FCSTD DOCUMENT  (FreeCAD 0.16R6707 (Git))
Label: Z4
License: All rights reserved
LicenseURL: http://en.wikipedia.org/wiki/All_rights_reserved
objects: Part::FeaturePython×70, Sketcher::SketchObject×60, App::DocumentObjectGroup×43, PartDesign::Pad×34, Part::Feature×24, PartDesign::Pocket×18, Part::Mirroring×11, PartDesign::PolarPattern×8, Part::MultiFuse×6, PartDesign::Revolution×2, Part::Fillet×2, Part::Chamfer×2, PartDesign::Fillet×2, Part::MultiCommon×1, Part::Sphere×1
note: 295 computed .brp shape members not serialized (recipe doc carries the construction recipe); baked Part::Feature solids carry a one-line shape summary decoded from their .brp

FEATURE [Part::Feature] Part__Feature001  label="MoteurD"
  Placement = pos=(-2.4,0,8.5) rot=(-0.57735,-0.57735,0.57735;2.0944rad)
  shape: bbox 27.5 x 17 x 17 mm, 28 faces (baked)
FEATURE [Part::FeaturePython] Clone001  label="MoteurG"  # Draft clone (typed FeaturePython)
  Objects = -> [Part__Feature001]
  Placement = pos=(2.4,0,8.5) rot=(0.57735,-0.57735,0.57735;4.18879rad)
  Scale = (1,1,1)
FEATURE [Part::Feature] Part__Feature014  label="Axe"
  Placement = pos=(0,0,5.5) rot=(0,0,1;0rad)
  shape: bbox 4.5 x 4 x 15.2 mm, 12 faces (baked)
FEATURE [Part::Feature] Part__Feature020  label="Pignon1"
  Placement = pos=(-26.2,0,8.5) rot=(-0.55834,0.613607,-0.55834;2.04087rad)
  shape: bbox 4 x 6.752 x 6.785 mm, 485 faces (baked)
FEATURE [Part::Feature] Part__Feature022  label="Couronne"
  Placement = pos=(0,0,11.5) rot=(0,1,0;3.14159rad)
  shape: bbox 20.79 x 20.8 x 4 mm, 805 faces (baked)
FEATURE [Sketcher::SketchObject] Sketch001  label="JanteBaseA"
  sketch-geometry (6):
    g0: Circle [constr] CenterX=0 CenterY=0 CenterZ=0 NormalX=0 NormalY=0 NormalZ=1 Radius=10
    g1: Circle [constr] CenterX=0 CenterY=0 CenterZ=0 NormalX=0 NormalY=0 NormalZ=1 Radius=9
    g2: Circle [constr] CenterX=0 CenterY=0 CenterZ=0 NormalX=0 NormalY=0 NormalZ=1 Radius=3
    g3: Circle [constr] CenterX=0 CenterY=0 CenterZ=0 NormalX=0 NormalY=0 NormalZ=1 Radius=2.75
    g4: Circle [constr] CenterX=0 CenterY=0 CenterZ=0 NormalX=0 NormalY=0 NormalZ=1 Radius=4
    g5: Circle CenterX=0 CenterY=0 CenterZ=0 NormalX=0 NormalY=0 NormalZ=1 Radius=10.4
  constraints (14):
    c: Coincident(g0,g-1)
    c: Coincident(g1,g-1)
    c: Radius(g1) = 9
    c: Radius(g0) = 10
    c: Coincident(g2,g-1)
    c: Radius(g2) = 3
    c: Coincident(g3,g-1)
    c: Radius(g3) = 2.75
    c: PointOnObject(g4,g-1)
    c: Radius(g4) = 4
    c: PointOnObject(g5,g-1)
    c: Radius(g5) = 10.4
    c: Coincident(g5,g-1)
    c: Coincident(g4,g-1)
FEATURE [PartDesign::Pad] Pad003  label="Extrusion1A"
  Length = 8.5
  Length2 = 100
  Sketch = -> Sketch001
  Type = 0
FEATURE [Sketcher::SketchObject] Sketch018  label="JanteEvidageA"
  Placement = pos=(0,0,0) rot=(1,0,0;3.14159rad)
  Support = -> Pad003 [Face2]
  sketch-geometry (6):
    g0: Circle [constr] CenterX=0 CenterY=0 CenterZ=0 NormalX=0 NormalY=0 NormalZ=1 Radius=10
    g1: Circle CenterX=0 CenterY=0 CenterZ=0 NormalX=0 NormalY=0 NormalZ=1 Radius=9
    g2: Circle [constr] CenterX=0 CenterY=0 CenterZ=0 NormalX=0 NormalY=0 NormalZ=1 Radius=3
    g3: Circle [constr] CenterX=0 CenterY=0 CenterZ=0 NormalX=0 NormalY=0 NormalZ=1 Radius=2.75
    g4: Circle [constr] CenterX=0 CenterY=0 CenterZ=0 NormalX=0 NormalY=0 NormalZ=1 Radius=4
    g5: Circle [constr] CenterX=0 CenterY=0 CenterZ=0 NormalX=0 NormalY=0 NormalZ=1 Radius=10.4
  constraints (14):
    c: Coincident(g0,g-1)
    c: Coincident(g1,g-1)
    c: Radius(g1) = 9
    c: Radius(g0) = 10
    c: Coincident(g2,g-1)
    c: Radius(g2) = 3
    c: Coincident(g3,g-1)
    c: Radius(g3) = 2.75
    c: PointOnObject(g4,g-1)
    c: Radius(g4) = 4
    c: PointOnObject(g5,g-1)
    c: Radius(g5) = 10.4
    c: Coincident(g5,g-1)
    c: Coincident(g4,g-1)
FEATURE [PartDesign::Pocket] Pocket006  label="Evidage1A"
  Length = 7.5
  Sketch = -> Sketch018
  Type = 0
FEATURE [Sketcher::SketchObject] Sketch019  label="JantePercageA"
  Placement = pos=(0,0,7.5) rot=(1,0,0;3.14159rad)
  Support = -> Pocket006 [Face5]
  sketch-geometry (6):
    g0: Circle [constr] CenterX=0 CenterY=0 CenterZ=0 NormalX=0 NormalY=0 NormalZ=1 Radius=10
    g1: Circle [constr] CenterX=0 CenterY=0 CenterZ=0 NormalX=0 NormalY=0 NormalZ=1 Radius=9
    g2: Circle [constr] CenterX=0 CenterY=0 CenterZ=0 NormalX=0 NormalY=0 NormalZ=1 Radius=3
    g3: Circle [constr] CenterX=0 CenterY=0 CenterZ=0 NormalX=0 NormalY=0 NormalZ=1 Radius=2.75
    g4: Circle CenterX=0 CenterY=0 CenterZ=0 NormalX=0 NormalY=0 NormalZ=1 Radius=6
    g5: Circle [constr] CenterX=0 CenterY=0 CenterZ=0 NormalX=0 NormalY=0 NormalZ=1 Radius=10.4
  constraints (14):
    c: Coincident(g0,g-1)
    c: Coincident(g1,g-1)
    c: Radius(g1) = 9
    c: Radius(g0) = 10
    c: Coincident(g2,g-1)
    c: Radius(g2) = 3
    c: Coincident(g3,g-1)
    c: Radius(g3) = 2.75
    c: PointOnObject(g4,g-1)
    c: Radius(g4) = 6
    c: PointOnObject(g5,g-1)
    c: Radius(g5) = 10.4
    c: Coincident(g5,g-1)
    c: Coincident(g4,g-1)
FEATURE [PartDesign::Pocket] Pocket007  label="Percage1A"
  Length = 5
  Sketch = -> Sketch019
  Type = 1
FEATURE [Sketcher::SketchObject] Sketch020  label="JanteBaseB"
  sketch-geometry (6):
    g0: Circle [constr] CenterX=0 CenterY=0 CenterZ=0 NormalX=0 NormalY=0 NormalZ=1 Radius=10
    g1: Circle CenterX=0 CenterY=0 CenterZ=0 NormalX=0 NormalY=0 NormalZ=1 Radius=9
    g2: Circle CenterX=0 CenterY=0 CenterZ=0 NormalX=0 NormalY=0 NormalZ=1 Radius=3.1
    g3: Circle [constr] CenterX=0 CenterY=0 CenterZ=0 NormalX=0 NormalY=0 NormalZ=1 Radius=2.75
    g4: Circle [constr] CenterX=0 CenterY=0 CenterZ=0 NormalX=0 NormalY=0 NormalZ=1 Radius=4
    g5: Circle [constr] CenterX=0 CenterY=0 CenterZ=0 NormalX=0 NormalY=0 NormalZ=1 Radius=10.4
  constraints (14):
    c: Coincident(g0,g-1)
    c: Coincident(g1,g-1)
    c: Radius(g1) = 9
    c: Radius(g0) = 10
    c: Coincident(g2,g-1)
    c: Radius(g2) = 3.1
    c: Coincident(g3,g-1)
    c: Radius(g3) = 2.75
    c: PointOnObject(g4,g-1)
    c: Radius(g4) = 4
    c: PointOnObject(g5,g-1)
    c: Radius(g5) = 10.4
    c: Coincident(g5,g-1)
    c: Coincident(g4,g-1)
FEATURE [PartDesign::Pad] Pad004  label="Extrusion1B"
  Length = 6
  Length2 = 100
  Sketch = -> Sketch020
  Type = 0
FEATURE [Sketcher::SketchObject] Sketch005  label="JanteEvidageB"
  Placement = pos=(0,0,6) rot=(0,0,1;0rad)
  Support = -> Pad004 [Face4]
  sketch-geometry (6):
    g0: Circle [constr] CenterX=0 CenterY=0 CenterZ=0 NormalX=0 NormalY=0 NormalZ=1 Radius=10
    g1: Circle CenterX=0 CenterY=0 CenterZ=0 NormalX=0 NormalY=0 NormalZ=1 Radius=9
    g2: Circle [constr] CenterX=0 CenterY=0 CenterZ=0 NormalX=0 NormalY=0 NormalZ=1 Radius=3
    g3: Circle [constr] CenterX=0 CenterY=0 CenterZ=0 NormalX=0 NormalY=0 NormalZ=1 Radius=2.75
    g4: Circle CenterX=0 CenterY=0 CenterZ=0 NormalX=0 NormalY=0 NormalZ=1 Radius=4.5
    g5: Circle [constr] CenterX=0 CenterY=0 CenterZ=0 NormalX=0 NormalY=0 NormalZ=1 Radius=10.4
  constraints (14):
    c: Coincident(g0,g-1)
    c: Coincident(g1,g-1)
    c: Radius(g1) = 9
    c: Radius(g0) = 10
    c: Coincident(g2,g-1)
    c: Radius(g2) = 3
    c: Coincident(g3,g-1)
    c: Radius(g3) = 2.75
    c: PointOnObject(g4,g-1)
    c: Radius(g4) = 4.5
    c: PointOnObject(g5,g-1)
    c: Radius(g5) = 10.4
    c: Coincident(g5,g-1)
    c: Coincident(g4,g-1)
FEATURE [PartDesign::Pocket] Pocket008  label="Evidage1B"
  Length = 4
  Sketch = -> Sketch005
  Type = 0
FEATURE [Sketcher::SketchObject] Sketch007  label="JanteAjouragesA"
  Placement = pos=(0,0,0) rot=(1,0,0;3.14159rad)
  Support = -> Pocket007 [Face2]
  sketch-geometry (6):
    g0: ArcOfCircle CenterX=0 CenterY=0 CenterZ=0 NormalX=0 NormalY=0 NormalZ=1 Radius=9 StartAngle=1.0472 EndAngle=2.0944
    g1: ArcOfCircle CenterX=-1e-12 CenterY=-1.4e-11 CenterZ=0 NormalX=0 NormalY=0 NormalZ=1 Radius=4.7e-10 StartAngle=1.6983 EndAngle=1.76808
    g2: ArcOfCircle CenterX=-9e-12 CenterY=0 CenterZ=0 NormalX=0 NormalY=0 NormalZ=1 Radius=4.5 StartAngle=0.698132 EndAngle=2.44346
    g3: LineSegment StartX=-4.5 StartY=7.79423 StartZ=0 EndX=-3.4472 EndY=2.89254 EndZ=0
    g4: LineSegment StartX=4.5 StartY=7.79423 StartZ=0 EndX=3.4472 EndY=2.89254 EndZ=0
    g5: LineSegment [constr] StartX=0 StartY=0 StartZ=0 EndX=3.4472 EndY=2.89254 EndZ=0
  constraints (13):
    c: Coincident(g4,g2)
    c: Coincident(g3,g2)
    c: Coincident(g0,g4)
    c: Coincident(g0,g3)
    c: Symmetric(g2,g2,g-2)
    c: Coincident(g5,g-1)
    c: Coincident(g5,g2)
    c: Angle(g5,g-2) = 0.872665
    c: Symmetric(g0,g0,g-2)
    c: Coincident(g2,g-1)
    c: Coincident(g0,g-1)
    c: Radius(g2) = 4.5
    c: Radius(g0) = 9
FEATURE [PartDesign::Pocket] Pocket010  label="Ajourage1A"
  Length = 5
  Sketch = -> Sketch007
  Type = 1
FEATURE [PartDesign::PolarPattern] PolarPattern002  label="Ajourages1A"
  Angle = 360
  Axis = -> Sketch007 [N_Axis]
  Occurrences = 3
  Originals = -> [Pocket010]
FEATURE [Sketcher::SketchObject] Sketch009  label="JanteExtrusionB"
  Placement = pos=(0,0,2) rot=(0,0,1;0rad)
  Support = -> Pocket008 [Face3]
  sketch-geometry (3):
    g0: ArcOfCircle CenterX=-1e-12 CenterY=-1.4e-11 CenterZ=0 NormalX=0 NormalY=0 NormalZ=1 Radius=4.7e-10 StartAngle=1.6983 EndAngle=1.76808
    g1: Circle CenterX=0 CenterY=7.5 CenterZ=0 NormalX=0 NormalY=0 NormalZ=1 Radius=1
    g2: LineSegment [constr] StartX=0 StartY=0 StartZ=0 EndX=0 EndY=7.5 EndZ=0
  constraints (5):
    c: Coincident(g2,g-1)
    c: Coincident(g1,g2)
    c: Distance(g2) = 7.5
    c: Radius(g1) = 1
    c: PointOnObject(g1,g-2)
FEATURE [Sketcher::SketchObject] Sketch022  label="JanteEvidage2A"
  Placement = pos=(0,0,0) rot=(1,0,0;3.14159rad)
  Support = -> PolarPattern002 [Face2]
  sketch-geometry (6):
    g0: Circle CenterX=0 CenterY=0 CenterZ=0 NormalX=0 NormalY=0 NormalZ=1 Radius=10
    g1: Circle [constr] CenterX=0 CenterY=0 CenterZ=0 NormalX=0 NormalY=0 NormalZ=1 Radius=9
    g2: Circle [constr] CenterX=0 CenterY=0 CenterZ=0 NormalX=0 NormalY=0 NormalZ=1 Radius=3
    g3: Circle [constr] CenterX=0 CenterY=0 CenterZ=0 NormalX=0 NormalY=0 NormalZ=1 Radius=2.75
    g4: Circle [constr] CenterX=0 CenterY=0 CenterZ=0 NormalX=0 NormalY=0 NormalZ=1 Radius=4
    g5: Circle CenterX=0 CenterY=0 CenterZ=0 NormalX=0 NormalY=0 NormalZ=1 Radius=10.4
  constraints (14):
    c: Coincident(g0,g-1)
    c: Coincident(g1,g-1)
    c: Radius(g1) = 9
    c: Radius(g0) = 10
    c: Coincident(g2,g-1)
    c: Radius(g2) = 3
    c: Coincident(g3,g-1)
    c: Radius(g3) = 2.75
    c: PointOnObject(g4,g-1)
    c: Radius(g4) = 4
    c: PointOnObject(g5,g-1)
    c: Radius(g5) = 10.4
    c: Coincident(g5,g-1)
    c: Coincident(g4,g-1)
FEATURE [PartDesign::Pocket] Pocket014  label="Evidage2A"
  Length = 7.5
  Sketch = -> Sketch022
  Type = 0
FEATURE [Sketcher::SketchObject] Sketch021  label="JantePercage2A"
  Placement = pos=(0,0,7.5) rot=(1,0,0;3.14159rad)
  Support = -> Pocket014 [Face18]
  sketch-geometry (3):
    g0: ArcOfCircle CenterX=-1e-12 CenterY=-1.4e-11 CenterZ=0 NormalX=0 NormalY=0 NormalZ=1 Radius=4.7e-10 StartAngle=1.6983 EndAngle=1.76808
    g1: Circle CenterX=-6.49519 CenterY=3.75 CenterZ=0 NormalX=0 NormalY=0 NormalZ=1 Radius=1
    g2: LineSegment [constr] StartX=0 StartY=0 StartZ=0 EndX=-6.49519 EndY=3.75 EndZ=0
  constraints (5):
    c: Coincident(g2,g-1)
    c: Angle(g-2,g2) = 1.0472
    c: Coincident(g1,g2)
    c: Distance(g2) = 7.5
    c: Radius(g1) = 1
FEATURE [PartDesign::Pocket] Pocket013  label="Percage2A"
  Length = 5
  Sketch = -> Sketch021
  Type = 1
FEATURE [PartDesign::PolarPattern] PolarPattern005  label="Percages2A"
  Angle = 360
  Axis = -> Sketch021 [N_Axis]
  Occurrences = 3
  Originals = -> [Pocket013]
FEATURE [PartDesign::Pad] Pad005  label="Extrusion2B"
  Length = 1
  Length2 = 100
  Sketch = -> Sketch009
  Type = 0
FEATURE [PartDesign::PolarPattern] PolarPattern006  label="Extrusions2B"
  Angle = 360
  Axis = -> Sketch009 [N_Axis]
  Occurrences = 3
  Originals = -> [Pad005]
FEATURE [Part::MultiCommon] Common  label="UnionA"
  Shapes = -> [Pocket014,PolarPattern005]
FEATURE [App::DocumentObjectGroup] Groupe008  label="JantePartA"
  Group = -> [Pad003,Pocket006,Pocket007,Pocket010,Pocket013,PolarPattern002,Common]
FEATURE [Sketcher::SketchObject] Sketch023  label="JanteEvidage2B"
  Placement = pos=(0,0,11.5) rot=(0,0,1;2.0944rad)
  Support = -> PolarPattern006 [Face23]
  sketch-geometry (1):
    g0: Circle CenterX=0 CenterY=2.6 CenterZ=0 NormalX=0 NormalY=0 NormalZ=1 Radius=0.8
  constraints (3):
    c: Radius(g0) = 0.8
    c: PointOnObject(g0,g-2)
    c: DistanceY(g-1,g0) = 2.6
FEATURE [PartDesign::Pocket] Pocket015  label="Evidage2B"
  Length = 4
  Sketch = -> Sketch023
  Type = 0
FEATURE [PartDesign::PolarPattern] PolarPattern007  label="Evidages2B"
  Angle = 360
  Axis = -> Sketch023 [N_Axis]
  Occurrences = 3
  Originals = -> [Pocket015]
FEATURE [Sketcher::SketchObject] Sketch008  label="JanteAjouragesB"
  Placement = pos=(0,0,0) rot=(1,0,0;3.14159rad)
  Support = -> PolarPattern007 [Face2]
  sketch-geometry (7):
    g0: ArcOfCircle CenterX=0 CenterY=0 CenterZ=0 NormalX=0 NormalY=0 NormalZ=1 Radius=9.5 StartAngle=0.872665 EndAngle=2.26893
    g1: ArcOfCircle CenterX=-1e-12 CenterY=-1.4e-11 CenterZ=0 NormalX=0 NormalY=0 NormalZ=1 Radius=4.7e-10 StartAngle=1.6983 EndAngle=1.76808
    g2: ArcOfCircle CenterX=0 CenterY=0 CenterZ=0 NormalX=0 NormalY=0 NormalZ=1 Radius=4.5 StartAngle=0.872665 EndAngle=2.26893
    g3: LineSegment StartX=-6.10648 StartY=7.27742 StartZ=0 EndX=-2.89254 EndY=3.4472 EndZ=0
    g4: LineSegment StartX=6.10648 StartY=7.27742 StartZ=0 EndX=2.89254 EndY=3.4472 EndZ=0
    g5: LineSegment [constr] StartX=0 StartY=0 StartZ=0 EndX=6.10648 EndY=7.27742 EndZ=0
    g6: LineSegment [constr] StartX=0 StartY=0 StartZ=0 EndX=-6.10648 EndY=7.27742 EndZ=0
  constraints (16):
    c: Coincident(g3,g2)
    c: Coincident(g0,g4)
    c: Coincident(g0,g3)
    c: Symmetric(g0,g0,g-2)
    c: Coincident(g2,g-1)
    c: Coincident(g5,g-1)
    c: Coincident(g5,g0)
    c: Coincident(g0,g-1)
    c: Coincident(g2,g4)
    c: PointOnObject(g2,g5)
    c: Angle(g5,g-2) = 0.698132
    c: Coincident(g6,g-1)
    c: Coincident(g6,g0)
    c: PointOnObject(g2,g6)
    c: Radius(g0) = 9.5
    c: Radius(g2) = 4.5
FEATURE [PartDesign::Pocket] Pocket011  label="Ajourage1B"
  Length = 5
  Sketch = -> Sketch008
  Type = 1
FEATURE [PartDesign::PolarPattern] PolarPattern003  label="Ajourages1B"
  Angle = 360
  Axis = -> Sketch008 [N_Axis]
  Occurrences = 3
  Originals = -> [Pocket011]
FEATURE [App::DocumentObjectGroup] Groupe009  label="JantePartB"
  Group = -> [Pad004,Pocket008,Pad005,PolarPattern006,Pocket015,PolarPattern007,Pocket011,PolarPattern003]
FEATURE [Part::Feature] Part__Feature004  label="Pneu"
  Placement = pos=(0,0,8.5) rot=(0,1,0;3.14159rad)
  shape: bbox 26.52 x 26.52 x 8.5 mm, 8 faces (baked)
FEATURE [Part::FeaturePython] Clone015  label="Pignon2"  # Draft clone (typed FeaturePython)
  Objects = -> [Part__Feature020]
  Placement = pos=(26.2,0,8.5) rot=(-0.594651,-0.541093,0.594651;2.14963rad)
  Scale = (1,1,1)
FEATURE [App::DocumentObjectGroup] Groupe006  label="Pignons"
  Group = -> [Part__Feature020,Clone015]
FEATURE [Part::FeaturePython] Clone016  label="Couronne001"  # Draft clone (typed FeaturePython)
  Objects = -> [Part__Feature022]
  Placement = pos=(-23.5,-12.915,10.15) rot=(0,-1,0;1.5708rad)
  Scale = (1,1,1)
FEATURE [Part::FeaturePython] Clone017  label="Axe001"  # Draft clone (typed FeaturePython)
  Objects = -> [Part__Feature014]
  Placement = pos=(-29.5,-12.915,10.15) rot=(0,1,0;1.5708rad)
  Scale = (1,1,1)
FEATURE [Part::FeaturePython] Clone020  label="Pneu001"  # Draft clone (typed FeaturePython)
  Objects = -> [Part__Feature004]
  Placement = pos=(-26.5,-12.915,10.15) rot=(0,-1,0;1.5708rad)
  Scale = (1,1,1)
FEATURE [Part::FeaturePython] Clone021  label="JantePartA001"  # Draft clone (typed FeaturePython)
  Objects = -> [Common]
  Placement = pos=(-35,-12.915,10.15) rot=(0,1,0;1.5708rad)
  Scale = (1,1,1)
FEATURE [Sketcher::SketchObject] Sketch024
  Placement = pos=(0,0,0) rot=(1,0,0;1.5708rad)
  sketch-geometry (21):
    g0: ArcOfCircle CenterX=-1.21 CenterY=2.96 CenterZ=0 NormalX=0 NormalY=0 NormalZ=1 Radius=0.04 StartAngle=1.5708 EndAngle=3.14159
    g1: LineSegment StartX=-1.25 StartY=2.96 StartZ=0 EndX=-1.25 EndY=2.74 EndZ=0
    g2: LineSegment StartX=-1.21 StartY=2.7 StartZ=0 EndX=-0.993029 EndY=2.7 EndZ=0
    g3: LineSegment [constr] StartX=3 StartY=2.25 StartZ=0 EndX=-3 EndY=2.25 EndZ=0
    g4: ArcOfCircle CenterX=-1.21 CenterY=2.74 CenterZ=0 NormalX=0 NormalY=0 NormalZ=1 Radius=0.04 StartAngle=3.14159 EndAngle=4.71239
    g5: ArcOfCircle CenterX=1.21 CenterY=2.96 CenterZ=0 NormalX=0 NormalY=0 NormalZ=1 Radius=0.04 StartAngle=6.28319 EndAngle=7.85398
    g6: LineSegment StartX=1.25 StartY=2.96 StartZ=0 EndX=1.25 EndY=2.74 EndZ=0
    g7: LineSegment StartX=1.21 StartY=2.7 StartZ=0 EndX=0.993029 EndY=2.7 EndZ=0
    g8: ArcOfCircle CenterX=1.21 CenterY=2.74 CenterZ=0 NormalX=0 NormalY=0 NormalZ=1 Radius=0.04 StartAngle=4.71239 EndAngle=6.28319
    g9: ArcOfCircle CenterX=-1.21 CenterY=1.54 CenterZ=0 NormalX=0 NormalY=0 NormalZ=1 Radius=0.04 StartAngle=3.14159 EndAngle=4.71238
    g10: LineSegment StartX=-1.25 StartY=1.54 StartZ=0 EndX=-1.25 EndY=1.76 EndZ=0
    g11: LineSegment StartX=-1.21 StartY=1.8 StartZ=0 EndX=-0.993029 EndY=1.8 EndZ=0
    g12: ArcOfCircle CenterX=-1.21 CenterY=1.76 CenterZ=0 NormalX=0 NormalY=0 NormalZ=1 Radius=0.04 StartAngle=1.5708 EndAngle=3.14159
    g13: ArcOfCircle CenterX=1.21 CenterY=1.54 CenterZ=0 NormalX=0 NormalY=0 NormalZ=1 Radius=0.04 StartAngle=4.71243 EndAngle=6.28319
    g14: LineSegment StartX=1.25 StartY=1.54 StartZ=0 EndX=1.25 EndY=1.76 EndZ=0
    g15: LineSegment StartX=1.21 StartY=1.8 StartZ=0 EndX=0.993029 EndY=1.8 EndZ=0
    g16: ArcOfCircle CenterX=1.21 CenterY=1.76 CenterZ=0 NormalX=0 NormalY=0 NormalZ=1 Radius=0.04 StartAngle=0 EndAngle=1.5708
    g17: ArcOfCircle CenterX=-0.1 CenterY=2.25 CenterZ=0 NormalX=0 NormalY=0 NormalZ=1 Radius=1 StartAngle=2.67483 EndAngle=3.60836
    g18: ArcOfCircle CenterX=0.1 CenterY=2.25 CenterZ=0 NormalX=0 NormalY=0 NormalZ=1 Radius=1 StartAngle=5.81642 EndAngle=6.74995
    g19: LineSegment StartX=-1.21 StartY=3 StartZ=0 EndX=1.21 EndY=3 EndZ=0
    g20: LineSegment StartX=-1.21 StartY=1.5 StartZ=0 EndX=1.21 EndY=1.5 EndZ=0
  constraints (61):
    c: Radius(g0) = 0.04
    c: Coincident(g1,g0)
    c: Vertical(g1)
    c: Horizontal(g2)
    c: Horizontal(g3)
    c: Tangent(g1,g0)
    c: Tangent(g1,g4) = -1.5708
    c: Tangent(g2,g4) = -1.5708
    c: Radius(g4) = 0.04
    c: Radius(g5) = 0.04
    c: Coincident(g6,g5)
    c: Vertical(g6)
    c: Horizontal(g7)
    c: Tangent(g6,g8) = 1.5708
    c: Tangent(g7,g8) = 1.5708
    c: Radius(g8) = 0.04
    c: Radius(g9) = 0.04
    c: Coincident(g10,g9)
    c: Vertical(g10)
    c: Horizontal(g11)
    c: Tangent(g10,g9)
    c: Tangent(g10,g12) = 1.5708
    c: Tangent(g11,g12) = 1.5708
    c: Radius(g12) = 0.04
    c: Radius(g13) = 0.04
    c: Coincident(g14,g13)
    c: Vertical(g14)
    c: Horizontal(g15)
    c: Tangent(g14,g13)
    c: Tangent(g14,g16) = -1.5708
    c: Tangent(g15,g16) = -1.5708
    c: Radius(g16) = 0.04
    c: DistanceX(g3,g3) = 6
    c: DistanceX(g9,g13) = 2.5
    c: Symmetric(g15,g7,g3)
    c: Symmetric(g11,g2,g3)
    c: Tangent(g5,g6)
    c: Symmetric(g5,g0,g-2)
    c: Symmetric(g13,g9,g-2)
    c: Symmetric(g9,g0,g3)
    c: Symmetric(g3,g3,g-2)
    c: DistanceY(g-1,g9) = 1.5
    c: DistanceY(g-1,g0) = 3
    c: Equal(g1,g6)
    c: Equal(g2,g7)
    c: DistanceY(g7,g5) = 0.3
    c: Coincident(g11,g17)
    c: Coincident(g2,g17)
    c: Coincident(g15,g18)
    c: Coincident(g7,g18)
    c: Radius(g17) = 1
    c: Equal(g18,g17)
    c: DistanceX(g17,g18) = 0.2
    c: Coincident(g19,g0)
    c: Coincident(g19,g5)
    c: Horizontal(g19)
    c: Coincident(g20,g9)
    c: Coincident(g20,g13)
    c: Horizontal(g20)
    c: Tangent(g20,g13)
    c: Tangent(g20,g9)
FEATURE [PartDesign::Revolution] Revolution
  Angle = 360
  Axis = (1,0,0)
  Base = (0,0,0)
  Placement = pos=(0,0,0) rot=(1,0,0;1.5708rad)
  ReferenceAxis = -> Sketch024 [H_Axis]
  Sketch = -> Sketch024
FEATURE [App::DocumentObjectGroup] Groupe021  label="Roulements6x2.5-3"
  Group = -> [Revolution]
FEATURE [Part::FeaturePython] Clone026  label="Roulement1"  # Draft clone (typed FeaturePython)
  Objects = -> [Revolution]
  Placement = pos=(-24.75,-12.915,10.15) rot=(0,0,1;0rad)
  Scale = (1,1,1)
FEATURE [Part::FeaturePython] Clone027  label="Roulement2"  # Draft clone (typed FeaturePython)
  Objects = -> [Revolution]
  Placement = pos=(-28.25,-12.915,10.15) rot=(0,0,1;0rad)
  Scale = (1,1,1)
FEATURE [Part::FeaturePython] Clone028  label="JantePartB001"  # Draft clone (typed FeaturePython)
  Objects = -> [PolarPattern003]
  Placement = pos=(-29.5,-12.915,10.15) rot=(0,1,0;1.5708rad)
  Scale = (1,1,1)
FEATURE [Sketcher::SketchObject] Sketch025
  sketch-geometry (7):
    g0: Circle CenterX=0 CenterY=0 CenterZ=0 NormalX=0 NormalY=0 NormalZ=1 Radius=6.95
    g1: Circle [constr] CenterX=0 CenterY=0 CenterZ=0 NormalX=0 NormalY=0 NormalZ=1 Radius=2
    g2: ArcOfCircle [constr] CenterX=0 CenterY=0 CenterZ=0 NormalX=0 NormalY=0 NormalZ=1 Radius=5.5 StartAngle=0.872667 EndAngle=2.26893
    g3: ArcOfCircle [constr] CenterX=0 CenterY=0 CenterZ=0 NormalX=0 NormalY=0 NormalZ=1 Radius=3 StartAngle=0.872665 EndAngle=2.26893
    g4: LineSegment [constr] StartX=0 StartY=0 StartZ=0 EndX=-6.72606 EndY=8.0158 EndZ=0
    g5: ArcOfCircle [constr] CenterX=-2.73185 CenterY=3.25569 CenterZ=0 NormalX=0 NormalY=0 NormalZ=1 Radius=1.25 StartAngle=2.26893 EndAngle=5.41052
    g6: ArcOfCircle [constr] CenterX=2.73185 CenterY=3.25569 CenterZ=0 NormalX=0 NormalY=0 NormalZ=1 Radius=1.25 StartAngle=4.01426 EndAngle=7.15586
  constraints (19):
    c: Coincident(g0,g-1)
    c: Radius(g0) = 6.95
    c: Coincident(g1,g-1)
    c: Radius(g1) = 2
    c: Coincident(g2,g-1)
    c: Coincident(g3,g-1)
    c: Radius(g3) = 3
    c: Radius(g2) = 5.5
    c: Coincident(g4,g-1)
    c: Angle(g-2,g4) = 0.698132
    c: PointOnObject(g5,g4)
    c: Coincident(g2,g5)
    c: Coincident(g3,g5)
    c: Tangent(g3,g5)
    c: Tangent(g5,g2)
    c: Equal(g6,g5)
    c: Symmetric(g6,g5,g-2)
    c: Coincident(g2,g6)
    c: Coincident(g6,g3)
FEATURE [PartDesign::Pad] Pad006
  Length = 6.4
  Length2 = 100
  Sketch = -> Sketch025
  Type = 0
FEATURE [Sketcher::SketchObject] Sketch027
  Placement = pos=(0,0,6.4) rot=(0,0,1;0rad)
  Support = -> Pad006 [Face3]
  sketch-geometry (1):
    g0: Circle CenterX=0 CenterY=0 CenterZ=0 NormalX=0 NormalY=0 NormalZ=1 Radius=2
  constraints (2):
    c: Coincident(g0,g-1)
    c: Radius(g0) = 2
FEATURE [PartDesign::Pad] Pad007
  Length = 1.5
  Length2 = 100
  Sketch = -> Sketch027
  Type = 0
FEATURE [Sketcher::SketchObject] Sketch028
  Placement = pos=(0,0,0) rot=(1,0,0;3.14159rad)
  Support = -> Pad007 [Face2]
  sketch-geometry (1):
    g0: Circle CenterX=0 CenterY=0 CenterZ=0 NormalX=0 NormalY=0 NormalZ=1 Radius=6.5
  constraints (2):
    c: Coincident(g0,g-1)
    c: Radius(g0) = 6.5
FEATURE [PartDesign::Pocket] Pocket016
  Length = 6
  Sketch = -> Sketch028
  Type = 0
FEATURE [Sketcher::SketchObject] Sketch026
  Placement = pos=(0,0,6.4) rot=(0,0,1;0rad)
  Support = -> Pocket016 [Face3]
  sketch-geometry (7):
    g0: Circle [constr] CenterX=0 CenterY=0 CenterZ=0 NormalX=0 NormalY=0 NormalZ=1 Radius=6.95
    g1: Circle [constr] CenterX=0 CenterY=0 CenterZ=0 NormalX=0 NormalY=0 NormalZ=1 Radius=2
    g2: ArcOfCircle CenterX=0 CenterY=0 CenterZ=0 NormalX=0 NormalY=0 NormalZ=1 Radius=5.5 StartAngle=1.0472 EndAngle=2.0944
    g3: ArcOfCircle CenterX=0 CenterY=0 CenterZ=0 NormalX=0 NormalY=0 NormalZ=1 Radius=3 StartAngle=1.0472 EndAngle=2.0944
    g4: LineSegment [constr] StartX=0 StartY=0 StartZ=0 EndX=-4.6491 EndY=8.05248 EndZ=0
    g5: ArcOfCircle CenterX=-2.125 CenterY=3.68061 CenterZ=0 NormalX=0 NormalY=0 NormalZ=1 Radius=1.25 StartAngle=2.0944 EndAngle=5.23599
    g6: ArcOfCircle CenterX=2.125 CenterY=3.68061 CenterZ=0 NormalX=0 NormalY=0 NormalZ=1 Radius=1.25 StartAngle=4.18878 EndAngle=7.33039
  constraints (19):
    c: Coincident(g0,g-1)
    c: Radius(g0) = 6.95
    c: Coincident(g1,g-1)
    c: Radius(g1) = 2
    c: Coincident(g2,g-1)
    c: Coincident(g3,g-1)
    c: Radius(g3) = 3
    c: Radius(g2) = 5.5
    c: Coincident(g4,g-1)
    c: Angle(g-2,g4) = 0.523599
    c: PointOnObject(g5,g4)
    c: Coincident(g2,g5)
    c: Coincident(g3,g5)
    c: Tangent(g3,g5)
    c: Tangent(g5,g2)
    c: Equal(g6,g5)
    c: Symmetric(g6,g5,g-2)
    c: Coincident(g2,g6)
    c: Coincident(g6,g3)
FEATURE [PartDesign::Pocket] Pocket017
  Length = 5
  Sketch = -> Sketch026
  Type = 1
FEATURE [PartDesign::PolarPattern] PolarPattern008
  Angle = 360
  Axis = -> Sketch026 [N_Axis]
  Occurrences = 3
  Originals = -> [Pocket017]
FEATURE [Sketcher::SketchObject] Sketch029
  Placement = pos=(0,0,7.9) rot=(0,0,1;0rad)
  Support = -> PolarPattern008 [Face19]
  sketch-geometry (1):
    g0: Circle CenterX=0 CenterY=0 CenterZ=0 NormalX=0 NormalY=0 NormalZ=1 Radius=0.75
  constraints (1):
    c: Radius(g0) = 0.75
FEATURE [PartDesign::Pocket] Pocket018
  Length = 5
  Sketch = -> Sketch029
  Type = 1
FEATURE [Sketcher::SketchObject] Sketch006
  sketch-geometry (5):
    g0: Circle [constr] CenterX=0 CenterY=0 CenterZ=0 NormalX=0 NormalY=0 NormalZ=1 Radius=6.5
    g1: LineSegment StartX=0.5 StartY=2.44949 StartZ=0 EndX=0.5 EndY=5.24949 EndZ=0
    g2: LineSegment StartX=0.5 StartY=5.24949 StartZ=0 EndX=-0.5 EndY=5.24949 EndZ=0
    g3: LineSegment StartX=-0.5 StartY=5.24949 StartZ=0 EndX=-0.5 EndY=2.44949 EndZ=0
    g4: ArcOfCircle CenterX=0 CenterY=0 CenterZ=0 NormalX=0 NormalY=0 NormalZ=1 Radius=2.5 StartAngle=1.36944 EndAngle=1.77215
  constraints (14):
    c: Coincident(g0,g-1)
    c: Radius(g0) = 6.5
    c: Coincident(g1,g2)
    c: Coincident(g2,g3)
    c: Horizontal(g2)
    c: Vertical(g1)
    c: Vertical(g3)
    c: Coincident(g4,g-1)
    c: Radius(g4) = 2.5
    c: Symmetric(g4,g4,g-2)
    c: DistanceX(g4,g4) = 1
    c: Coincident(g1,g4)
    c: Coincident(g3,g4)
    c: DistanceY(g1,g1) = 2.8
FEATURE [PartDesign::Pad] Pad008
  Length = 3.5
  Length2 = 100
  Sketch = -> Sketch006
  Type = 0
FEATURE [Sketcher::SketchObject] Sketch030
  sketch-geometry (8):
    g0: Circle [constr] CenterX=0 CenterY=0 CenterZ=0 NormalX=0 NormalY=0 NormalZ=1 Radius=6.5
    g1: LineSegment [constr] StartX=1.25 StartY=2.16506 StartZ=0 EndX=1.25 EndY=5.26506 EndZ=0
    g2: LineSegment StartX=1.25 StartY=5.26506 StartZ=0 EndX=-1.25 EndY=5.26506 EndZ=0
    g3: LineSegment [constr] StartX=-1.25 StartY=5.26506 StartZ=0 EndX=-1.25 EndY=2.16506 EndZ=0
    g4: ArcOfCircle [constr] CenterX=0 CenterY=0 CenterZ=0 NormalX=0 NormalY=0 NormalZ=1 Radius=2.5 StartAngle=1.0472 EndAngle=2.0944
    g5: ArcOfCircle CenterX=0 CenterY=0 CenterZ=0 NormalX=0 NormalY=0 NormalZ=1 Radius=6 StartAngle=1.36093 EndAngle=1.78067
    g6: LineSegment StartX=-1.25 StartY=5.86835 StartZ=0 EndX=-1.25 EndY=5.26506 EndZ=0
    g7: LineSegment StartX=1.25 StartY=5.86835 StartZ=0 EndX=1.25 EndY=5.26506 EndZ=0
  constraints (24):
    c: Coincident(g0,g-1)
    c: Radius(g0) = 6.5
    c: Coincident(g1,g2)
    c: Coincident(g2,g3)
    c: Horizontal(g2)
    c: Vertical(g1)
    c: Vertical(g3)
    c: Coincident(g4,g-1)
    c: Radius(g4) = 2.5
    c: Symmetric(g4,g4,g-2)
    c: DistanceX(g4,g4) = 2.5
    c: Coincident(g1,g4)
    c: Coincident(g3,g4)
    c: DistanceY(g1,g1) = 3.1
    c: Coincident(g5,g-1)
    c: Radius(g5) = 6
    c: Symmetric(g5,g5,g-2)
    c: DistanceX(g5,g5) = 2.5
    c: Coincident(g6,g5)
    c: Coincident(g6,g2)
    c: Vertical(g6)
    c: Coincident(g7,g5)
    c: Coincident(g7,g1)
    c: Vertical(g7)
FEATURE [PartDesign::Pad] Pad009
  Length = 4
  Length2 = 0.5
  Sketch = -> Sketch030
  Type = 4
FEATURE [Part::MultiFuse] Fusion001
  Shapes = -> [Pad008,Pad009]
FEATURE [Part::FeaturePython] Array  # Draft array (typed FeaturePython)
  Angle = 360
  ArrayType = 1
  Axis = (0,0,1)
  Base = -> Fusion001
  Center = (0,0,0)
  Fuse = false
  IntervalAxis = (0,0,0)
  IntervalX = (1,0,0)
  IntervalY = (0,1,0)
  IntervalZ = (0,0,0)
  NumberPolar = 9
  NumberX = 0
  NumberY = 0
  NumberZ = 0
  Placement = pos=(0,0,1) rot=(0,0,1;0rad)
FEATURE [Sketcher::SketchObject] Sketch031
  sketch-geometry (1):
    g0: Circle CenterX=0 CenterY=0 CenterZ=0 NormalX=0 NormalY=0 NormalZ=1 Radius=0.75
  constraints (2):
    c: Coincident(g0,g-1)
    c: Radius(g0) = 0.75
FEATURE [PartDesign::Pad] Pad010
  Length = 8.5
  Length2 = 4.5
  Sketch = -> Sketch031
  Type = 4
FEATURE [Sketcher::SketchObject] Sketch032
  sketch-geometry (2):
    g0: Circle CenterX=0 CenterY=0 CenterZ=0 NormalX=0 NormalY=0 NormalZ=1 Radius=2.5
    g1: Circle CenterX=0 CenterY=0 CenterZ=0 NormalX=0 NormalY=0 NormalZ=1 Radius=1.75
  constraints (4):
    c: Coincident(g0,g-1)
    c: Coincident(g1,g-1)
    c: Radius(g0) = 2.5
    c: Radius(g1) = 1.75
FEATURE [PartDesign::Pad] Pad011
  Length = 5.5
  Length2 = 3.6
  Sketch = -> Sketch032
  Type = 4
FEATURE [Sketcher::SketchObject] Sketch033
  Placement = pos=(0,0,0) rot=(1,0,0;1.5708rad)
  sketch-geometry (25):
    g0: ArcOfCircle CenterX=-0.46 CenterY=1.71 CenterZ=0 NormalX=0 NormalY=0 NormalZ=1 Radius=0.04 StartAngle=1.5708 EndAngle=3.14159
    g1: LineSegment StartX=-0.5 StartY=1.71 StartZ=0 EndX=-0.5 EndY=1.54 EndZ=0
    g2: LineSegment StartX=-0.46 StartY=1.5 StartZ=0 EndX=-0.383013 EndY=1.5 EndZ=0
    g3: ArcOfCircle CenterX=0.05 CenterY=1.25 CenterZ=0 NormalX=0 NormalY=0 NormalZ=1 Radius=0.5 StartAngle=2.61799 EndAngle=3.14159
    g4: LineSegment [constr] StartX=1 StartY=1.25 StartZ=0 EndX=-1 EndY=1.25 EndZ=0
    g5: ArcOfCircle CenterX=-0.46 CenterY=1.54 CenterZ=0 NormalX=0 NormalY=0 NormalZ=1 Radius=0.04 StartAngle=3.14159 EndAngle=4.71239
    g6: LineSegment StartX=-0.46 StartY=1.75 StartZ=0 EndX=0 EndY=1.75 EndZ=0
    g7: ArcOfCircle CenterX=0.46 CenterY=1.71 CenterZ=0 NormalX=0 NormalY=0 NormalZ=1 Radius=0.04 StartAngle=1.25767e-07 EndAngle=1.5708
    g8: LineSegment StartX=0.5 StartY=1.71 StartZ=0 EndX=0.5 EndY=1.54 EndZ=0
    g9: LineSegment StartX=0.46 StartY=1.5 StartZ=0 EndX=0.383013 EndY=1.5 EndZ=0
    g10: ArcOfCircle CenterX=-0.05 CenterY=1.25 CenterZ=0 NormalX=0 NormalY=0 NormalZ=1 Radius=0.5 StartAngle=6e-12 EndAngle=0.523599
    g11: ArcOfCircle CenterX=0.46 CenterY=1.54 CenterZ=0 NormalX=0 NormalY=0 NormalZ=1 Radius=0.04 StartAngle=4.71239 EndAngle=6.28319
    g12: LineSegment StartX=0.46 StartY=1.75 StartZ=0 EndX=0 EndY=1.75 EndZ=0
    g13: ArcOfCircle CenterX=-0.46 CenterY=0.79 CenterZ=0 NormalX=0 NormalY=0 NormalZ=1 Radius=0.04 StartAngle=3.14159 EndAngle=4.71239
    g14: LineSegment StartX=-0.5 StartY=0.79 StartZ=0 EndX=-0.5 EndY=0.96 EndZ=0
    g15: LineSegment StartX=-0.46 StartY=1 StartZ=0 EndX=-0.383013 EndY=1 EndZ=0
    g16: ArcOfCircle CenterX=0.05 CenterY=1.25 CenterZ=0 NormalX=0 NormalY=0 NormalZ=1 Radius=0.5 StartAngle=3.14159 EndAngle=3.66519
    g17: ArcOfCircle CenterX=-0.46 CenterY=0.96 CenterZ=0 NormalX=0 NormalY=0 NormalZ=1 Radius=0.04 StartAngle=1.5708 EndAngle=3.14159
    g18: LineSegment StartX=-0.46 StartY=0.75 StartZ=0 EndX=0 EndY=0.75 EndZ=0
    g19: ArcOfCircle CenterX=0.46 CenterY=0.79 CenterZ=0 NormalX=0 NormalY=0 NormalZ=1 Radius=0.04 StartAngle=4.71239 EndAngle=6.28319
    g20: LineSegment StartX=0.5 StartY=0.79 StartZ=0 EndX=0.5 EndY=0.96 EndZ=0
    g21: LineSegment StartX=0.46 StartY=1 StartZ=0 EndX=0.383013 EndY=1 EndZ=0
    g22: ArcOfCircle CenterX=-0.05 CenterY=1.25 CenterZ=0 NormalX=0 NormalY=0 NormalZ=1 Radius=0.5 StartAngle=5.75959 EndAngle=6.28319
    g23: ArcOfCircle CenterX=0.46 CenterY=0.96 CenterZ=0 NormalX=0 NormalY=0 NormalZ=1 Radius=0.04 StartAngle=0 EndAngle=1.5708
    g24: LineSegment StartX=0.46 StartY=0.75 StartZ=0 EndX=0 EndY=0.75 EndZ=0
  constraints (75):
    c: Radius(g0) = 0.04
    c: Coincident(g1,g0)
    c: Vertical(g1)
    c: Horizontal(g2)
    c: Horizontal(g4)
    c: DistanceY(g-1,g4) = 1.25
    c: Tangent(g1,g0)
    c: Tangent(g1,g5) = -1.5708
    c: Tangent(g2,g5) = -1.5708
    c: Radius(g5) = 0.04
    c: Coincident(g6,g0)
    c: Horizontal(g6)
    c: PointOnObject(g6,g-2)
    c: Tangent(g0,g6)
    c: DistanceX(g0,g6) = 0.5
    c: Radius(g3) = 0.5
    c: Coincident(g2,g3)
    c: PointOnObject(g3,g4)
    c: Perpendicular(g3,g4)
    c: Radius(g7) = 0.04
    c: Coincident(g8,g7)
    c: Vertical(g8)
    c: Horizontal(g9)
    c: Tangent(g8,g11) = 1.5708
    c: Tangent(g9,g11) = 1.5708
    c: Radius(g11) = 0.04
    c: Coincident(g12,g7)
    c: Horizontal(g12)
    c: Tangent(g7,g12)
    c: Radius(g10) = 0.5
    c: Coincident(g9,g10)
    c: Radius(g13) = 0.04
    c: Coincident(g14,g13)
    c: Vertical(g14)
    c: Horizontal(g15)
    c: Tangent(g14,g13)
    c: Tangent(g14,g17) = 1.5708
    c: Tangent(g15,g17) = 1.5708
    c: Radius(g17) = 0.04
    c: Coincident(g18,g13)
    c: Horizontal(g18)
    c: Radius(g16) = 0.5
    c: Coincident(g15,g16)
    c: Radius(g19) = 0.04
    c: Coincident(g20,g19)
    c: Vertical(g20)
    c: Horizontal(g21)
    c: Tangent(g20,g19)
    c: Tangent(g20,g23) = -1.5708
    c: Tangent(g21,g23) = -1.5708
    c: Radius(g23) = 0.04
    c: Coincident(g24,g19)
    c: Horizontal(g24)
    c: Radius(g22) = 0.5
    c: Coincident(g21,g22)
    c: Coincident(g3,g16)
    c: Coincident(g10,g22)
    c: Coincident(g6,g12)
    c: Coincident(g18,g24)
    c: PointOnObject(g10,g4)
    c: DistanceX(g4,g4) = 2
    c: DistanceX(g4,g-1) = 1
    c: DistanceY(g18,g6) = 1
    c: DistanceX(g13,g19) = 1
    c: Symmetric(g21,g9,g4)
    c: Symmetric(g15,g2,g4)
    c: Symmetric(g10,g3,g-2)
    c: DistanceX(g10,g3) = 0.1
    c: DistanceY(g15,g2) = 0.5
    c: DistanceY(g21,g9) = 0.5
    c: DistanceX(g13,g18) = 0.5
    c: PointOnObject(g18,g-2)
    c: DistanceY(g4,g0) = 0.5
    c: DistanceX(g6,g7) = 0.5
    c: Tangent(g7,g8)
FEATURE [PartDesign::Revolution] Revolution001
  Angle = 360
  Axis = (1,0,0)
  Base = (0,0,0)
  Placement = pos=(0,0,0) rot=(1,0,0;1.5708rad)
  ReferenceAxis = -> Sketch033 [H_Axis]
  Sketch = -> Sketch033
FEATURE [Part::FeaturePython] Clone032  label="Roulement003"  # Draft clone (typed FeaturePython)
  Objects = -> [Revolution001]
  Placement = pos=(0,0,-3.7) rot=(0,1,0;1.5708rad)
  Scale = (1,1,1)
FEATURE [Part::FeaturePython] Clone033  label="Roulement004"  # Draft clone (typed FeaturePython)
  Objects = -> [Revolution001]
  Placement = pos=(0,0,5) rot=(0,1,0;1.5708rad)
  Scale = (1,1,1)
FEATURE [App::DocumentObjectGroup] Groupe024  label="Roulements"
  Group = -> [Revolution001,Clone032,Clone033]
FEATURE [Part::Fillet] Fillet
  Base = -> Pad010
  Edges = 2 edges r=0.1: [Edge2,Edge3]
FEATURE [Part::Chamfer] Chamfer
  Base = -> Pocket018
  Edges = 1 edges r=0.4: [Edge3]
FEATURE [App::DocumentObjectGroup] Groupe022  label="Rotor"
  Group = -> [Pad006,Pad007,Pocket016,Pocket017,PolarPattern008,Pocket018,Chamfer]
FEATURE [Sketcher::SketchObject] Sketch012
  Placement = pos=(0,0,-3.6) rot=(1,0,0;3.14159rad)
  Support = -> Pad011 [Face3]
  sketch-geometry (5):
    g0: Circle CenterX=0 CenterY=0 CenterZ=0 NormalX=0 NormalY=0 NormalZ=1 Radius=1.75
    g1: ArcOfCircle CenterX=0 CenterY=0 CenterZ=0 NormalX=0 NormalY=0 NormalZ=1 Radius=5.75 StartAngle=2.08727 EndAngle=4.19591
    g2: ArcOfCircle CenterX=0 CenterY=0 CenterZ=0 NormalX=0 NormalY=0 NormalZ=1 Radius=5.75 StartAngle=5.22886 EndAngle=7.33751
    g3: LineSegment StartX=-2.83945 StartY=5 StartZ=0 EndX=2.83945 EndY=5 EndZ=0
    g4: LineSegment StartX=-2.83945 StartY=-5 StartZ=0 EndX=2.83945 EndY=-5 EndZ=0
  constraints (14):
    c: Coincident(g0,g-1)
    c: Radius(g0) = 1.75
    c: Coincident(g2,g-1)
    c: Coincident(g1,g-1)
    c: Radius(g2) = 5.75
    c: Radius(g1) = 5.75
    c: Horizontal(g3)
    c: Coincident(g2,g3)
    c: Coincident(g1,g3)
    c: Horizontal(g4)
    c: Coincident(g2,g4)
    c: Coincident(g1,g4)
    c: DistanceY(g2,g-1) = 5
    c: DistanceY(g-1,g1) = 5
FEATURE [PartDesign::Pad] Pad012
  Length = 1
  Length2 = 100
  Sketch = -> Sketch012
  Type = 0
FEATURE [Sketcher::SketchObject] Sketch013
  Placement = pos=(0,0,-4.6) rot=(1,0,0;3.14159rad)
  Support = -> Pad012 [Face10]
  sketch-geometry (6):
    g0: Circle [constr] CenterX=-4.25 CenterY=0 CenterZ=0 NormalX=0 NormalY=0 NormalZ=1 Radius=0.7
    g1: ArcOfCircle CenterX=0 CenterY=0 CenterZ=0 NormalX=0 NormalY=0 NormalZ=1 Radius=5 StartAngle=2.15484 EndAngle=2.55755
    g2: ArcOfCircle CenterX=0 CenterY=0 CenterZ=0 NormalX=0 NormalY=0 NormalZ=1 Radius=3 StartAngle=2.15484 EndAngle=2.55755
    g3: ArcOfCircle CenterX=-3.33697 CenterY=2.20559 CenterZ=0 NormalX=0 NormalY=0 NormalZ=1 Radius=1 StartAngle=2.55755 EndAngle=5.69915
    g4: ArcOfCircle CenterX=-2.20559 CenterY=3.33697 CenterZ=0 NormalX=0 NormalY=0 NormalZ=1 Radius=1 StartAngle=5.29643 EndAngle=8.43803
    g5: LineSegment [constr] StartX=0 StartY=0 StartZ=0 EndX=-9.0054 EndY=9.0054 EndZ=0
  constraints (20):
    c: DistanceX(g0,g-1) = 4.25
    c: PointOnObject(g0,g-1)
    c: Radius(g0) = 0.7
    c: Coincident(g1,g-1)
    c: Coincident(g2,g-1)
    c: Radius(g1) = 5
    c: Radius(g2) = 3
    c: Coincident(g5,g-1)
    c: Angle(g-2,g5) = 0.785398
    c: Symmetric(g1,g1,g5)
    c: Symmetric(g2,g2,g5)
    c: Coincident(g4,g1)
    c: Coincident(g2,g4)
    c: Coincident(g1,g3)
    c: Coincident(g2,g3)
    c: Tangent(g1,g4)
    c: Tangent(g4,g2)
    c: Tangent(g2,g3)
    c: Tangent(g3,g1)
    c: Distance(g1,g1) = 2
FEATURE [PartDesign::Pocket] Pocket019
  Length = 5
  Sketch = -> Sketch013
  Type = 1
FEATURE [PartDesign::PolarPattern] PolarPattern009
  Angle = 360
  Axis = -> Sketch013 [N_Axis]
  Occurrences = 4
  Originals = -> [Pocket019]
FEATURE [Sketcher::SketchObject] Sketch034
  Placement = pos=(0,0,-4.6) rot=(1,0,0;3.14159rad)
  Support = -> PolarPattern009 [Face26]
  sketch-geometry (4):
    g0: Circle CenterX=-4.25 CenterY=0 CenterZ=0 NormalX=0 NormalY=0 NormalZ=1 Radius=0.8
    g1: Circle CenterX=4.25 CenterY=0 CenterZ=0 NormalX=0 NormalY=0 NormalZ=1 Radius=0.8
    g2: Circle CenterX=0 CenterY=3.5 CenterZ=0 NormalX=0 NormalY=0 NormalZ=1 Radius=0.8
    g3: Circle CenterX=0 CenterY=-3.5 CenterZ=0 NormalX=0 NormalY=0 NormalZ=1 Radius=0.8
  constraints (10):
    c: DistanceX(g0,g-1) = 4.25
    c: PointOnObject(g0,g-1)
    c: Symmetric(g1,g0,g-2)
    c: PointOnObject(g2,g-2)
    c: Radius(g2) = 0.8
    c: DistanceY(g-1,g2) = 3.5
    c: Symmetric(g3,g2,g-1)
    c: Equal(g3,g2)
    c: Equal(g0,g2)
    c: Equal(g1,g2)
FEATURE [PartDesign::Pocket] Pocket020
  Length = 5
  Sketch = -> Sketch034
  Type = 1
FEATURE [Part::Chamfer] Chamfer001
  Base = -> Pocket020
  Edges = 1 edges r=0.4: [Edge32]
FEATURE [App::DocumentObjectGroup] Groupe023  label="Stator"
  Group = -> [Fusion001,Array,Pad011,Fillet,Pad012,Pocket019,Pocket020,Chamfer001,PolarPattern009]
FEATURE [Part::Fillet] Fillet001
  Base = -> Pad010
  Edges = 2 edges r=0.1: [Edge2,Edge3]
FEATURE [App::DocumentObjectGroup] Groupe025  label="Axe002"
  Group = -> [Pad010,Fillet001]
FEATURE [Part::FeaturePython] Clone002  label="Rotor001"  # Draft clone (typed FeaturePython)
  Objects = -> [Chamfer]
  Placement = pos=(0,-25,7.9) rot=(0,1,0;3.14159rad)
  Scale = (1,1,1)
FEATURE [Part::FeaturePython] Clone003  label="StatorBobine"  # Draft clone (typed FeaturePython)
  Objects = -> [Array]
  Placement = pos=(0,-25,6.9) rot=(0,1,0;3.14159rad)
  Scale = (1,1,1)
FEATURE [Part::FeaturePython] Clone004  label="Stator001"  # Draft clone (typed FeaturePython)
  Objects = -> [Chamfer001]
  Placement = pos=(0,-25,7.9) rot=(0,1,0;3.14159rad)
  Scale = (1,1,1)
FEATURE [Part::FeaturePython] Clone005  label="Roulement001"  # Draft clone (typed FeaturePython)
  Objects = -> [Clone032]
  Placement = pos=(0,-25,11.6) rot=(0,-1,0;1.5708rad)
  Scale = (1,1,1)
FEATURE [Part::FeaturePython] Clone006  label="Roulement002"  # Draft clone (typed FeaturePython)
  Objects = -> [Clone033]
  Placement = pos=(0,-25,2.9) rot=(0,-1,0;1.5708rad)
  Scale = (1,1,1)
FEATURE [Part::FeaturePython] Clone007  label="Axe003"  # Draft clone (typed FeaturePython)
  Objects = -> [Fillet001]
  Placement = pos=(0,-25,7.9) rot=(0,1,0;3.14159rad)
  Scale = (1,1,1)
FEATURE [Sketcher::SketchObject] Sketch038
  sketch-geometry (1):
    g0: Circle CenterX=0 CenterY=0 CenterZ=0 NormalX=0 NormalY=0 NormalZ=1 Radius=16
  constraints (1):
    c: Radius(g0) = 16
FEATURE [PartDesign::Pad] Pad013
  Length = 6
  Length2 = 100
  Sketch = -> Sketch038
  Type = 0
FEATURE [Sketcher::SketchObject] Sketch036
  Placement = pos=(0,0,6) rot=(0,0,1;0rad)
  Support = -> Pad013 [Face3]
  sketch-geometry (1):
    g0: Circle CenterX=0 CenterY=0 CenterZ=0 NormalX=0 NormalY=0 NormalZ=1 Radius=6.875
FEATURE [PartDesign::Pocket] Pocket021
  Length = 5
  Sketch = -> Sketch036
  Type = 1
FEATURE [Sketcher::SketchObject] Sketch037
  Placement = pos=(0,0,6) rot=(0,0,1;0rad)
  Support = -> Pocket021 [Face3]
  sketch-geometry (2):
    g0: Circle CenterX=0 CenterY=0 CenterZ=0 NormalX=0 NormalY=0 NormalZ=1 Radius=7.6
    g1: Circle CenterX=0 CenterY=0 CenterZ=0 NormalX=0 NormalY=0 NormalZ=1 Radius=16
  constraints (2):
    c: Radius(g0) = 7.6
    c: Radius(g1) = 16
FEATURE [PartDesign::Pocket] Pocket022
  Length = 5
  Sketch = -> Sketch037
  Type = 0
FEATURE [Sketcher::SketchObject] Sketch035
  Placement = pos=(0,0,1) rot=(0,0,1;0rad)
  Support = -> Pocket022 [Face3]
  sketch-geometry (7):
    g0: ArcOfCircle CenterX=-4.14536 CenterY=10.2306 CenterZ=0 NormalX=0 NormalY=0 NormalZ=1 Radius=0.239272 StartAngle=2.53685 EndAngle=4.11953
    g1: ArcOfCircle CenterX=-4.11804 CenterY=10.5222 CenterZ=0 NormalX=0 NormalY=0 NormalZ=1 Radius=0.515814 StartAngle=4.39494 EndAngle=5.60571
    g2: ArcOfCircle CenterX=9.58061 CenterY=-0.0553145 CenterZ=0 NormalX=0 NormalY=0 NormalZ=1 Radius=16.7914 StartAngle=1.96626 EndAngle=2.48468
    g3: ArcOfCircle CenterX=9.58058 CenterY=-0.055346 CenterZ=0 NormalX=0 NormalY=0 NormalZ=1 Radius=16.7914 StartAngle=1.93967 EndAngle=1.96626
    g4: ArcOfCircle CenterX=-1.3403e-05 CenterY=-1.54298e-05 CenterZ=0 NormalX=0 NormalY=0 NormalZ=1 Radius=16 StartAngle=1.34858 EndAngle=1.38241
    g5: ArcOfCircle CenterX=1.79587e-05 CenterY=-4.76448e-06 CenterZ=0 NormalX=0 NormalY=0 NormalZ=1 Radius=16 StartAngle=1.38241 EndAngle=1.41662
    g6: ArcOfCircle CenterX=9.58061 CenterY=-0.0553169 CenterZ=0 NormalX=0 NormalY=0 NormalZ=1 Radius=17.3914 StartAngle=1.99282 EndAngle=2.49902
FEATURE [PartDesign::Pad] Pad014
  Length = 7
  Length2 = 100
  Sketch = -> Sketch035
  Type = 0
FEATURE [PartDesign::PolarPattern] PolarPattern010
  Angle = 360
  Axis = -> Sketch035 [N_Axis]
  Occurrences = 10
  Originals = -> [Pad014]
FEATURE [Part::FeaturePython] Clone034  label="ImpellerCW"  # Draft clone (typed FeaturePython)
  Objects = -> [PolarPattern010]
  Placement = pos=(0,-25,9.2) rot=(0,1,0;3.14159rad)
  Scale = (1,1,1)
FEATURE [Part::Mirroring] Part__Mirroring001  label="ImpellerCCW"
  Base = (0,0,0)
  Normal = (0,0,1)
  Placement = pos=(0,50,0) rot=(0,1,0;3.14159rad)
  Source = -> Clone034
FEATURE [Part::FeaturePython] Clone036  label="StatorBobine002"  # Draft clone (typed FeaturePython)
  Objects = -> [Clone003]
  Placement = pos=(0,25,6.9) rot=(0,1,0;3.14159rad)
  Scale = (1,1,1)
FEATURE [Part::FeaturePython] Clone037  label="Roulement005"  # Draft clone (typed FeaturePython)
  Objects = -> [Clone006]
  Placement = pos=(0,25,2.9) rot=(0,-1,0;1.5708rad)
  Scale = (1,1,1)
FEATURE [Part::FeaturePython] Clone038  label="Stator002"  # Draft clone (typed FeaturePython)
  Objects = -> [Clone004]
  Placement = pos=(0,25,7.9) rot=(0,1,0;3.14159rad)
  Scale = (1,1,1)
FEATURE [Part::FeaturePython] Clone039  label="Roulement006"  # Draft clone (typed FeaturePython)
  Objects = -> [Clone005]
  Placement = pos=(0,25,11.6) rot=(0,-1,0;1.5708rad)
  Scale = (1,1,1)
FEATURE [Part::FeaturePython] Clone040  label="Rotor002"  # Draft clone (typed FeaturePython)
  Objects = -> [Clone002]
  Placement = pos=(0,25,7.9) rot=(0,1,0;3.14159rad)
  Scale = (1,1,1)
FEATURE [Part::FeaturePython] Clone041  label="Axe004"  # Draft clone (typed FeaturePython)
  Objects = -> [Clone007]
  Placement = pos=(0,25,7.9) rot=(0,1,0;3.14159rad)
  Scale = (1,1,1)
FEATURE [App::DocumentObjectGroup] Groupe027  label="BrushlessMotor001"
  Group = -> [Clone036,Clone037,Clone038,Clone039,Clone041,Clone040]
FEATURE [App::DocumentObjectGroup] Groupe028  label="BrushlessMotor002"
  Group = -> [Clone007,Clone002,Clone005,Clone004,Clone006,Clone003]
FEATURE [App::DocumentObjectGroup] Groupe026  label="BrushlessMotors"
  Group = -> [Groupe023,Groupe025,Groupe024,Groupe022,Groupe027,Groupe028]
FEATURE [App::DocumentObjectGroup] Groupe029  label="Roue001"
  Group = -> [Clone028,Clone017,Clone021,Clone026,Clone016,Clone027,Clone020]
FEATURE [Part::FeaturePython] Clone049  label="JantePartB003"  # Draft clone (typed FeaturePython)
  Objects = -> [Clone028]
  Placement = pos=(29.5,-12.915,10.15) rot=(0,-1,0;1.5708rad)
  Scale = (1,1,1)
FEATURE [Part::FeaturePython] Clone050  label="Axe006"  # Draft clone (typed FeaturePython)
  Objects = -> [Clone017]
  Placement = pos=(29.5,-12.915,10.15) rot=(0,-1,0;1.5708rad)
  Scale = (1,1,1)
FEATURE [Part::FeaturePython] Clone051  label="JantePartA002"  # Draft clone (typed FeaturePython)
  Objects = -> [Clone021]
  Placement = pos=(35,-12.915,10.15) rot=(0,-1,0;1.5708rad)
  Scale = (1,1,1)
FEATURE [Part::FeaturePython] Clone052  label="Roulement009"  # Draft clone (typed FeaturePython)
  Objects = -> [Clone026]
  Placement = pos=(24.75,-12.915,10.15) rot=(0,1,0;3.14159rad)
  Scale = (1,1,1)
FEATURE [Part::FeaturePython] Clone053  label="Couronne003"  # Draft clone (typed FeaturePython)
  Objects = -> [Clone016]
  Placement = pos=(23.5,-12.915,10.15) rot=(0,1,0;1.5708rad)
  Scale = (1,1,1)
FEATURE [Part::FeaturePython] Clone054  label="Roulement010"  # Draft clone (typed FeaturePython)
  Objects = -> [Clone027]
  Placement = pos=(28.25,-12.915,10.15) rot=(0,1,0;3.14159rad)
  Scale = (1,1,1)
FEATURE [Part::FeaturePython] Clone055  label="Pneu003"  # Draft clone (typed FeaturePython)
  Objects = -> [Clone020]
  Placement = pos=(26.5,-12.915,10.15) rot=(0,1,0;1.5708rad)
  Scale = (1,1,1)
FEATURE [App::DocumentObjectGroup] Groupe031  label="Roue003"
  Group = -> [Clone049,Clone050,Clone051,Clone052,Clone053,Clone054,Clone055]
FEATURE [Part::FeaturePython] Clone056  label="JantePartB004"  # Draft clone (typed FeaturePython)
  Objects = -> [Clone028]
  Placement = pos=(29.5,12.915,10.15) rot=(0,-1,0;1.5708rad)
  Scale = (1,1,1)
FEATURE [Part::FeaturePython] Clone057  label="Axe007"  # Draft clone (typed FeaturePython)
  Objects = -> [Clone017]
  Placement = pos=(29.5,12.915,10.15) rot=(0,-1,0;1.5708rad)
  Scale = (1,1,1)
FEATURE [Part::FeaturePython] Clone058  label="JantePartA003"  # Draft clone (typed FeaturePython)
  Objects = -> [Clone021]
  Placement = pos=(35,12.915,10.15) rot=(0,-1,0;1.5708rad)
  Scale = (1,1,1)
FEATURE [Part::FeaturePython] Clone059  label="Roulement011"  # Draft clone (typed FeaturePython)
  Objects = -> [Clone026]
  Placement = pos=(24.75,12.915,10.15) rot=(0,1,0;3.14159rad)
  Scale = (1,1,1)
FEATURE [Part::FeaturePython] Clone060  label="Couronne004"  # Draft clone (typed FeaturePython)
  Objects = -> [Clone016]
  Placement = pos=(23.5,12.915,10.15) rot=(0,1,0;1.5708rad)
  Scale = (1,1,1)
FEATURE [Part::FeaturePython] Clone061  label="Roulement012"  # Draft clone (typed FeaturePython)
  Objects = -> [Clone027]
  Placement = pos=(28.25,12.915,10.15) rot=(0,1,0;3.14159rad)
  Scale = (1,1,1)
FEATURE [Part::FeaturePython] Clone062  label="Pneu004"  # Draft clone (typed FeaturePython)
  Objects = -> [Clone020]
  Placement = pos=(26.5,12.915,10.15) rot=(0,1,0;1.5708rad)
  Scale = (1,1,1)
FEATURE [App::DocumentObjectGroup] Groupe032  label="Roue004"
  Group = -> [Clone056,Clone057,Clone058,Clone059,Clone060,Clone061,Clone062]
FEATURE [Part::FeaturePython] Clone063  label="JantePartB005"  # Draft clone (typed FeaturePython)
  Objects = -> [Clone028]
  Placement = pos=(-29.5,12.915,10.15) rot=(0,1,0;1.5708rad)
  Scale = (1,1,1)
FEATURE [Part::FeaturePython] Clone064  label="Axe008"  # Draft clone (typed FeaturePython)
  Objects = -> [Clone017]
  Placement = pos=(-29.5,12.915,10.15) rot=(0,1,0;1.5708rad)
  Scale = (1,1,1)
FEATURE [Part::FeaturePython] Clone065  label="JantePartA004"  # Draft clone (typed FeaturePython)
  Objects = -> [Clone021]
  Placement = pos=(-35,12.915,10.15) rot=(0,1,0;1.5708rad)
  Scale = (1,1,1)
FEATURE [Part::FeaturePython] Clone066  label="Roulement013"  # Draft clone (typed FeaturePython)
  Objects = -> [Clone026]
  Placement = pos=(-24.75,12.915,10.15) rot=(0,0,1;0rad)
  Scale = (1,1,1)
FEATURE [Part::FeaturePython] Clone067  label="Couronne005"  # Draft clone (typed FeaturePython)
  Objects = -> [Clone016]
  Placement = pos=(-23.5,12.915,10.15) rot=(0,-1,0;1.5708rad)
  Scale = (1,1,1)
FEATURE [Part::FeaturePython] Clone068  label="Roulement014"  # Draft clone (typed FeaturePython)
  Objects = -> [Clone027]
  Placement = pos=(-28.25,12.915,10.15) rot=(0,0,1;0rad)
  Scale = (1,1,1)
FEATURE [Part::FeaturePython] Clone069  label="Pneu005"  # Draft clone (typed FeaturePython)
  Objects = -> [Clone020]
  Placement = pos=(-26.5,12.915,10.15) rot=(0,-1,0;1.5708rad)
  Scale = (1,1,1)
FEATURE [App::DocumentObjectGroup] Groupe033  label="Roue002"
  Group = -> [Clone063,Clone064,Clone065,Clone066,Clone067,Clone068,Clone069]
FEATURE [App::DocumentObjectGroup] Groupe019  label="Roues"
  Group = -> [Groupe029,Groupe031,Groupe032,Groupe033,Part__Feature022,Groupe008,Groupe009,Part__Feature014,Part__Feature004,Groupe021]
FEATURE [Sketcher::SketchObject] Sketch048
  sketch-geometry (13):
    g0: LineSegment [constr] StartX=-6 StartY=3 StartZ=0 EndX=6 EndY=3 EndZ=0
    g1: LineSegment StartX=-6 StartY=-3 StartZ=0 EndX=-5.97292 EndY=2.3104 EndZ=0
    g2: LineSegment StartX=-5.77208 StartY=2.3104 StartZ=0 EndX=-5.77208 EndY=-2.80435 EndZ=0
    g3: LineSegment StartX=-5.77208 StartY=-2.80435 StartZ=0 EndX=-5.60812 EndY=2.67649 EndZ=0
    g4: ArcOfCircle CenterX=0 CenterY=-45.7703 CenterZ=0 NormalX=0 NormalY=0 NormalZ=1 Radius=48.7703 StartAngle=1.5708 EndAngle=1.68604
    g5: LineSegment StartX=-5.97292 StartY=2.3104 StartZ=0 EndX=-5.77208 EndY=2.3104 EndZ=0
    g6: LineSegment StartX=-6 StartY=-3 StartZ=0 EndX=0 EndY=-3 EndZ=0
    g7: LineSegment StartX=6 StartY=-3 StartZ=0 EndX=5.97292 EndY=2.33656 EndZ=0
    g8: LineSegment StartX=5.82667 StartY=2.33656 StartZ=0 EndX=5.82667 EndY=-2.80435 EndZ=0
    g9: LineSegment StartX=5.82667 StartY=-2.80435 StartZ=0 EndX=5.60812 EndY=2.67649 EndZ=0
    g10: ArcOfCircle CenterX=0 CenterY=-45.7703 CenterZ=0 NormalX=0 NormalY=0 NormalZ=1 Radius=48.7703 StartAngle=1.45555 EndAngle=1.5708
    g11: LineSegment StartX=5.97292 StartY=2.33656 StartZ=0 EndX=5.82667 EndY=2.33656 EndZ=0
    g12: LineSegment StartX=6 StartY=-3 StartZ=0 EndX=0 EndY=-3 EndZ=0
  constraints (24):
    c: Horizontal(g0)
    c: Symmetric(g0,g1,g-1)
    c: DistanceX(g0,g0) = 12
    c: Vertical(g2)
    c: Coincident(g2,g3)
    c: Coincident(g3,g4)
    c: PointOnObject(g4,g-2)
    c: PointOnObject(g4,g0)
    c: Coincident(g5,g1)
    c: Coincident(g5,g2)
    c: Horizontal(g5)
    c: Coincident(g6,g1)
    c: PointOnObject(g6,g-2)
    c: Horizontal(g6)
    c: Vertical(g8)
    c: Coincident(g8,g9)
    c: Coincident(g9,g10)
    c: Coincident(g11,g7)
    c: Coincident(g11,g8)
    c: Horizontal(g11)
    c: Coincident(g12,g7)
    c: Horizontal(g12)
    c: Coincident(g6,g12)
    c: Coincident(g4,g10)
FEATURE [PartDesign::Pad] Pad019
  Length = 36
  Length2 = 100
  Sketch = -> Sketch048
  Type = 0
FEATURE [PartDesign::Fillet] Fillet002
  Base = -> Pad019 [Edge11]
  Radius = 2
FEATURE [PartDesign::Fillet] Fillet003
  Base = -> Fillet002 [Edge33]
  Radius = 1
FEATURE [Sketcher::SketchObject] Sketch049
  Placement = pos=(0,-3,0) rot=(1,0,0;1.5708rad)
  Support = -> Fillet003 [Face15]
  sketch-geometry (2):
    g0: ArcOfCircle CenterX=0 CenterY=61.6009 CenterZ=0 NormalX=0 NormalY=0 NormalZ=1 Radius=26.1277 StartAngle=4.44815 EndAngle=4.97662
    g1: LineSegment StartX=-6.82378 StartY=36.3801 StartZ=0 EndX=6.82378 EndY=36.3801 EndZ=0
  constraints (4):
    c: PointOnObject(g0,g-2)
    c: Coincident(g1,g0)
    c: Coincident(g1,g0)
    c: Horizontal(g1)
FEATURE [PartDesign::Pocket] Pocket028
  Length = 5
  Sketch = -> Sketch049
  Type = 1
FEATURE [Sketcher::SketchObject] Sketch050
  ExternalGeometry = -> [Pocket028]
  Placement = pos=(0,0,0) rot=(1,0,0;3.14159rad)
  Support = -> Pocket028 [Face1]
  sketch-geometry (4):
    g0: LineSegment StartX=-6 StartY=3 StartZ=0 EndX=-5.46926 EndY=2.66404 EndZ=0
    g1: LineSegment StartX=-5.46926 StartY=2.66404 StartZ=0 EndX=5.56052 EndY=2.66404 EndZ=0
    g2: LineSegment StartX=5.56052 StartY=2.66404 StartZ=0 EndX=6 EndY=3 EndZ=0
    g3: LineSegment StartX=-6 StartY=3 StartZ=0 EndX=6 EndY=3 EndZ=0
  constraints (7):
    c: Coincident(g1,g0)
    c: Horizontal(g1)
    c: Coincident(g2,g1)
    c: Coincident(g2,g-4)
    c: Coincident(g0,g-3)
    c: Coincident(g3,g0)
    c: Coincident(g3,g2)
FEATURE [PartDesign::Pad] Pad020
  Length = 4
  Length2 = 100
  Sketch = -> Sketch050
  Type = 0
FEATURE [Sketcher::SketchObject] Sketch051
  Placement = pos=(0,0,-4) rot=(1,0,0;3.14159rad)
  Support = -> Pad020 [Face23]
  sketch-geometry (8):
    g0: LineSegment StartX=-4 StartY=2.66427 StartZ=0 EndX=-2 EndY=2.66427 EndZ=0
    g1: LineSegment StartX=-2 StartY=2.66427 StartZ=0 EndX=-2 EndY=2.56427 EndZ=0
    g2: LineSegment StartX=-2 StartY=2.56427 StartZ=0 EndX=-4 EndY=2.56427 EndZ=0
    g3: LineSegment StartX=-4 StartY=2.56427 StartZ=0 EndX=-4 EndY=2.66427 EndZ=0
    g4: LineSegment StartX=2 StartY=2.66427 StartZ=0 EndX=4 EndY=2.66427 EndZ=0
    g5: LineSegment StartX=4 StartY=2.66427 StartZ=0 EndX=4 EndY=2.56427 EndZ=0
    g6: LineSegment StartX=4 StartY=2.56427 StartZ=0 EndX=2 EndY=2.56427 EndZ=0
    g7: LineSegment StartX=2 StartY=2.56427 StartZ=0 EndX=2 EndY=2.66427 EndZ=0
  constraints (22):
    c: Coincident(g0,g1)
    c: Coincident(g1,g2)
    c: Coincident(g2,g3)
    c: Coincident(g3,g0)
    c: Horizontal(g0)
    c: Horizontal(g2)
    c: Vertical(g1)
    c: Vertical(g3)
    c: Coincident(g4,g5)
    c: Coincident(g5,g6)
    c: Coincident(g6,g7)
    c: Coincident(g7,g4)
    c: Horizontal(g4)
    c: Horizontal(g6)
    c: Vertical(g5)
    c: Vertical(g7)
    c: DistanceX(g4,g4) = 2
    c: DistanceX(g0,g0) = 2
    c: DistanceY(g1,g1) = 0.1
    c: DistanceY(g7,g7) = 0.1
    c: DistanceX(g0,g4) = 4
    c: Symmetric(g0,g4,g-2)
FEATURE [PartDesign::Pad] Pad021
  Length = 3
  Length2 = 100
  Sketch = -> Sketch051
  Type = 0
FEATURE [Part::FeaturePython] Clone080  label="Batt1"  # Draft clone (typed FeaturePython)
  Objects = -> [Pad021]
  Placement = pos=(-15,-24.5,17) rot=(0.57735,-0.57735,0.57735;4.18879rad)
  Scale = (1,1,1)
FEATURE [Part::FeaturePython] Clone081  label="Batt2"  # Draft clone (typed FeaturePython)
  Objects = -> [Pad021]
  Placement = pos=(-15,-12.4,17) rot=(0.57735,-0.57735,0.57735;4.18879rad)
  Scale = (1,1,1)
FEATURE [Part::FeaturePython] Clone082  label="Batt3"  # Draft clone (typed FeaturePython)
  Objects = -> [Pad021]
  Placement = pos=(-15,21.9,17) rot=(0.57735,-0.57735,0.57735;4.18879rad)
  Scale = (1,1,1)
FEATURE [App::DocumentObjectGroup] Groupe038  label="Batteries"
  Group = -> [Pad019,Fillet002,Fillet003,Pocket028,Pad020,Pad021,Clone080,Clone081,Clone082]
FEATURE [Sketcher::SketchObject] Sketch076
  sketch-geometry (10):
    g0: ArcOfCircle CenterX=-21.0607 CenterY=36.4393 CenterZ=0 NormalX=0 NormalY=0 NormalZ=1 Radius=0.5 StartAngle=5.49779 EndAngle=7.06858
    g1: LineSegment StartX=-20.7071 StartY=36.7929 StartZ=0 EndX=-23.5355 EndY=39.6213 EndZ=0
    g2: ArcOfCircle CenterX=-23.182 CenterY=39.9749 CenterZ=0 NormalX=0 NormalY=0 NormalZ=1 Radius=0.5 StartAngle=2.35619 EndAngle=3.92699
    g3: ArcOfCircle CenterX=-21.0391 CenterY=40.6604 CenterZ=0 NormalX=0 NormalY=0 NormalZ=1 Radius=2.5184 StartAngle=1.43858 EndAngle=3.27381
    g4: ArcOfCircle CenterX=-20.3536 CenterY=42.8033 CenterZ=0 NormalX=0 NormalY=0 NormalZ=1 Radius=0.5 StartAngle=0.785398 EndAngle=2.35619
    g5: LineSegment StartX=-20 StartY=43.1569 StartZ=0 EndX=-17.1716 EndY=40.3284 EndZ=0
    g6: ArcOfCircle CenterX=-16.818 CenterY=40.682 CenterZ=0 NormalX=0 NormalY=0 NormalZ=1 Radius=0.5 StartAngle=3.92699 EndAngle=5.49779
    g7: LineSegment StartX=-16.4645 StartY=40.3284 StartZ=0 EndX=-16.1109 EndY=39.9749 EndZ=0
    g8: LineSegment StartX=-16.1109 StartY=39.9749 StartZ=0 EndX=-20.3536 EndY=35.7322 EndZ=0
    g9: LineSegment StartX=-20.3536 StartY=35.7322 StartZ=0 EndX=-20.7071 EndY=36.0858 EndZ=0
FEATURE [Sketcher::SketchObject] Sketch074
  sketch-geometry (10):
    g0: LineSegment StartX=-6.96447 StartY=49.8284 StartZ=0 EndX=-6.61091 EndY=49.4749 EndZ=0
    g1: LineSegment StartX=-6.61091 StartY=49.4749 StartZ=0 EndX=-10.8536 EndY=45.2322 EndZ=0
    g2: LineSegment StartX=-10.8536 StartY=45.2322 StartZ=0 EndX=-11.2071 EndY=45.5858 EndZ=0
    g3: ArcOfCircle CenterX=-11.5607 CenterY=45.9393 CenterZ=0 NormalX=0 NormalY=0 NormalZ=1 Radius=0.5 StartAngle=5.49779 EndAngle=7.06858
    g4: LineSegment StartX=-11.2071 StartY=46.2929 StartZ=0 EndX=-14.0355 EndY=49.1213 EndZ=0
    g5: ArcOfCircle CenterX=-13.682 CenterY=49.4749 CenterZ=0 NormalX=0 NormalY=0 NormalZ=1 Radius=0.5 StartAngle=2.35619 EndAngle=3.92699
    g6: ArcOfCircle CenterX=-11.5391 CenterY=50.1604 CenterZ=0 NormalX=0 NormalY=0 NormalZ=1 Radius=2.5184 StartAngle=1.43858 EndAngle=3.27381
    g7: ArcOfCircle CenterX=-10.8536 CenterY=52.3033 CenterZ=0 NormalX=0 NormalY=0 NormalZ=1 Radius=0.5 StartAngle=0.785398 EndAngle=2.35619
    g8: LineSegment StartX=-10.5 StartY=52.6569 StartZ=0 EndX=-7.67157 EndY=49.8284 EndZ=0
    g9: ArcOfCircle CenterX=-7.31802 CenterY=50.182 CenterZ=0 NormalX=0 NormalY=0 NormalZ=1 Radius=0.5 StartAngle=3.92699 EndAngle=5.49779
FEATURE [Sketcher::SketchObject] Sketch073
  sketch-geometry (10):
    g0: LineSegment StartX=-26.9387 StartY=30.8567 StartZ=0 EndX=-26.8864 EndY=30.3594 EndZ=0
    g1: LineSegment StartX=-26.8864 StartY=30.3594 StartZ=0 EndX=-32.8536 EndY=29.7322 EndZ=0
    g2: LineSegment StartX=-32.8536 StartY=29.7322 StartZ=0 EndX=-32.9058 EndY=30.2295 EndZ=0
    g3: ArcOfCircle CenterX=-32.9581 CenterY=30.7268 CenterZ=0 NormalX=0 NormalY=0 NormalZ=1 Radius=0.5 StartAngle=4.81711 EndAngle=6.3879
    g4: LineSegment StartX=-32.4608 StartY=30.779 StartZ=0 EndX=-32.8789 EndY=34.7571 EndZ=0
    g5: ArcOfCircle CenterX=-32.3817 CenterY=34.8094 CenterZ=0 NormalX=0 NormalY=0 NormalZ=1 Radius=0.5 StartAngle=1.67552 EndAngle=3.24631
    g6: ArcOfCircle CenterX=-30.2849 CenterY=33.9936 CenterZ=0 NormalX=0 NormalY=0 NormalZ=1 Radius=2.5184 StartAngle=0.757899 EndAngle=2.59313
    g7: ArcOfCircle CenterX=-28.4036 CenterY=35.2275 CenterZ=0 NormalX=0 NormalY=0 NormalZ=1 Radius=0.5 StartAngle=0.104719 EndAngle=1.67552
    g8: LineSegment StartX=-27.9063 StartY=35.2797 StartZ=0 EndX=-27.4882 EndY=31.3017 EndZ=0
    g9: ArcOfCircle CenterX=-26.991 CenterY=31.3539 CenterZ=0 NormalX=0 NormalY=0 NormalZ=1 Radius=0.5 StartAngle=3.24631 EndAngle=4.81711
FEATURE [Sketcher::SketchObject] Sketch077
  sketch-geometry (10):
    g0: ArcOfCircle CenterX=-15.3317 CenterY=41.9401 CenterZ=0 NormalX=0 NormalY=0 NormalZ=1 Radius=0.5 StartAngle=6.07375 EndAngle=7.64454
    g1: LineSegment StartX=-15.2277 StartY=42.4292 StartZ=0 EndX=-19.1403 EndY=43.2609 EndZ=0
    g2: ArcOfCircle CenterX=-19.0364 CenterY=43.7499 CenterZ=0 NormalX=0 NormalY=0 NormalZ=1 Radius=0.5 StartAngle=2.93215 EndAngle=4.50295
    g3: ArcOfCircle CenterX=-17.6126 CenterY=45.492 CenterZ=0 NormalX=0 NormalY=0 NormalZ=1 Radius=2.5184 StartAngle=2.01454 EndAngle=3.84977
    g4: ArcOfCircle CenterX=-18.2047 CenterY=47.6625 CenterZ=0 NormalX=0 NormalY=0 NormalZ=1 Radius=0.5 StartAngle=1.36136 EndAngle=2.93215
    g5: LineSegment StartX=-18.1008 StartY=48.1516 StartZ=0 EndX=-14.1882 EndY=47.32 EndZ=0
    g6: ArcOfCircle CenterX=-14.0842 CenterY=47.809 CenterZ=0 NormalX=0 NormalY=0 NormalZ=1 Radius=0.5 StartAngle=4.50295 EndAngle=6.07374
    g7: LineSegment StartX=-13.5952 StartY=47.7051 StartZ=0 EndX=-13.1061 EndY=47.6011 EndZ=0
    g8: LineSegment StartX=-13.1061 StartY=47.6011 StartZ=0 EndX=-14.3536 EndY=41.7322 EndZ=0
    g9: LineSegment StartX=-14.3536 StartY=41.7322 StartZ=0 EndX=-14.8426 EndY=41.8362 EndZ=0
FEATURE [App::DocumentObjectGroup] Z4_V1_2  label="Plan_orientation"
  Group = -> [Sketch076,Sketch074,Sketch073,Sketch077]
FEATURE [Sketcher::SketchObject] Sketch078  label="PCB45_plan"
  Placement = pos=(0,0,1) rot=(0,0,1;0rad)
  sketch-geometry (8):
    g0: LineSegment StartX=-20.1421 StartY=35.3579 StartZ=0 EndX=-6 EndY=49.5 EndZ=0
    g1: LineSegment StartX=-6 StartY=49.5 StartZ=0 EndX=-5.29289 EndY=48.7929 EndZ=0
    g2: LineSegment StartX=-5.29289 StartY=48.7929 StartZ=0 EndX=-19.435 EndY=34.6508 EndZ=0
    g3: LineSegment StartX=-19.435 StartY=34.6508 StartZ=0 EndX=-20.1421 EndY=35.3579 EndZ=0
    g4: LineSegment [constr] StartX=-33.8407 StartY=27.9602 StartZ=0 EndX=-23.8955 EndY=29.0055 EndZ=0
    g5: LineSegment [constr] StartX=-24 StartY=30 StartZ=0 EndX=-23.8955 EndY=29.0055 EndZ=0
    g6: LineSegment [constr] StartX=-24 StartY=30 StartZ=0 EndX=-33.9452 EndY=28.9547 EndZ=0
    g7: LineSegment [constr] StartX=-33.9452 StartY=28.9547 StartZ=0 EndX=-33.8407 EndY=27.9602 EndZ=0
  constraints (24):
    c: Angle(g-2,g0) = 2.35619
    c: Coincident(g0,g1)
    c: Perpendicular(g0,g1)
    c: Coincident(g1,g2)
    c: Parallel(g2,g0)
    c: Distance(g1) = 1
    c: Distance(g2) = 20
    c: Coincident(g2,g3)
    c: Coincident(g0,g3)
    c: Perpendicular(g0,g3)
    c: DistanceX(g0,g-1) = 6
    c: DistanceY(g-1,g0) = 49.5
    c: Angle(g4,g-2) = 1.46608
    c: Coincident(g4,g5)
    c: Coincident(g5,g6)
    c: Parallel(g6,g4)
    c: Perpendicular(g4,g5)
    c: Distance(g5) = 1
    c: Coincident(g6,g7)
    c: Coincident(g4,g7)
    c: Perpendicular(g4,g7)
    c: Distance(g4) = 10
    c: DistanceX(g5,g-1) = 24
    c: DistanceY(g-1,g5) = 30
FEATURE [Sketcher::SketchObject] Sketch079
  sketch-geometry (1):
    g0: Circle CenterX=0 CenterY=0 CenterZ=0 NormalX=0 NormalY=0 NormalZ=1 Radius=2.38
  constraints (2):
    c: Radius(g0) = 2.38
    c: Coincident(g0,g-1)
FEATURE [PartDesign::Pad] Pad023
  Length = 4.85
  Length2 = 100
  Sketch = -> Sketch079
  Type = 0
FEATURE [Sketcher::SketchObject] Sketch080
  Placement = pos=(0,0,0) rot=(1,0,0;3.14159rad)
  sketch-geometry (1):
    g0: Circle CenterX=0 CenterY=0 CenterZ=0 NormalX=0 NormalY=0 NormalZ=1 Radius=2.92
  constraints (2):
    c: Coincident(g0,g-1)
    c: Radius(g0) = 2.92
FEATURE [PartDesign::Pad] Pad024
  Length = 0.5
  Length2 = 0.26
  Placement = pos=(0,0,0) rot=(1,0,0;3.14159rad)
  Sketch = -> Sketch080
  Type = 4
FEATURE [Part::Sphere] Sphere  label="Sphère"
  Angle1 = -90
  Angle2 = 90
  Angle3 = 360
  Placement = pos=(0,0,3.86) rot=(0,0,1;0rad)
  Radius = 2.25
FEATURE [Part::MultiFuse] Fusion002
  Shapes = -> [Pad023,Pad024]
FEATURE [Part::MultiFuse] Fusion003
  Shapes = -> [Fusion002,Sphere]
FEATURE [Part::FeaturePython] Clone085  label="Clone of Fusion003"  # Draft clone (typed FeaturePython)
  Objects = -> [Fusion003]
  Placement = pos=(-9,47.6,12.38) rot=(-0.678598,0.281085,0.678598;2.59356rad)
  Scale = (1,1,1)
FEATURE [Part::FeaturePython] Clone086  label="Clone of Fusion004"  # Draft clone (typed FeaturePython)
  Objects = -> [Fusion003]
  Placement = pos=(-18.5,38.1,12.38) rot=(-0.357407,-0.862856,-0.357407;1.71777rad)
  Scale = (1,1,1)
FEATURE [Part::FeaturePython] Clone087  label="Clone of Fusion005"  # Draft clone (typed FeaturePython)
  Objects = -> [Fusion003]
  Placement = pos=(-13.9,44.6,12.38) rot=(-0.112485,-0.987266,-0.112485;1.58361rad)
  Scale = (1,1,1)
FEATURE [Part::FeaturePython] Clone088  label="Clone of Fusion006"  # Draft clone (typed FeaturePython)
  Objects = -> [Fusion003]
  Placement = pos=(-29.9,30.2,12.38) rot=(-0.556117,-0.617631,-0.556117;2.03504rad)
  Scale = (1,1,1)
FEATURE [Sketcher::SketchObject] Sketch082  label="PCB6_plan"
  Placement = pos=(0,0,1) rot=(0,0,1;0rad)
  sketch-geometry (8):
    g0: LineSegment [constr] StartX=-20.1421 StartY=35.3579 StartZ=0 EndX=-6 EndY=49.5 EndZ=0
    g1: LineSegment [constr] StartX=-6 StartY=49.5 StartZ=0 EndX=-5.29289 EndY=48.7929 EndZ=0
    g2: LineSegment [constr] StartX=-5.29289 StartY=48.7929 StartZ=0 EndX=-19.435 EndY=34.6508 EndZ=0
    g3: LineSegment [constr] StartX=-19.435 StartY=34.6508 StartZ=0 EndX=-20.1421 EndY=35.3579 EndZ=0
    g4: LineSegment StartX=-33.8407 StartY=27.9602 StartZ=0 EndX=-23.8955 EndY=29.0055 EndZ=0
    g5: LineSegment StartX=-24 StartY=30 StartZ=0 EndX=-23.8955 EndY=29.0055 EndZ=0
    g6: LineSegment StartX=-24 StartY=30 StartZ=0 EndX=-33.9452 EndY=28.9547 EndZ=0
    g7: LineSegment StartX=-33.9452 StartY=28.9547 StartZ=0 EndX=-33.8407 EndY=27.9602 EndZ=0
  constraints (24):
    c: Angle(g-2,g0) = 2.35619
    c: Coincident(g0,g1)
    c: Perpendicular(g0,g1)
    c: Coincident(g1,g2)
    c: Parallel(g2,g0)
    c: Distance(g1) = 1
    c: Distance(g2) = 20
    c: Coincident(g2,g3)
    c: Coincident(g0,g3)
    c: Perpendicular(g0,g3)
    c: DistanceX(g0,g-1) = 6
    c: DistanceY(g-1,g0) = 49.5
    c: Angle(g4,g-2) = 1.46608
    c: Coincident(g4,g5)
    c: Coincident(g5,g6)
    c: Parallel(g6,g4)
    c: Perpendicular(g4,g5)
    c: Distance(g5) = 1
    c: Coincident(g6,g7)
    c: Coincident(g4,g7)
    c: Perpendicular(g4,g7)
    c: Distance(g4) = 10
    c: DistanceX(g5,g-1) = 24
    c: DistanceY(g-1,g5) = 30
FEATURE [Part::Mirroring] Part__Mirroring002  label="Clone of Fusion003 (Mirror #3)"
  Base = (0,0,0)
  Normal = (1,0,0)
  Source = -> Clone085
FEATURE [Part::Mirroring] Part__Mirroring003  label="Clone of Fusion004 (Mirror #4)"
  Base = (0,0,0)
  Normal = (1,0,0)
  Source = -> Clone086
FEATURE [Part::Mirroring] Part__Mirroring004  label="Clone of Fusion005 (Mirror #5)"
  Base = (0,0,0)
  Normal = (1,0,0)
  Source = -> Clone087
FEATURE [Part::Mirroring] Part__Mirroring005  label="Clone of Fusion006 (Mirror #6)"
  Base = (0,0,0)
  Normal = (1,0,0)
  Source = -> Clone088
FEATURE [App::DocumentObjectGroup] Groupe039  label="DiodesLazer"
  Group = -> [Fusion003,Clone085,Clone086,Clone087,Clone088,Part__Mirroring002,Part__Mirroring003,Part__Mirroring004,Part__Mirroring005,Z4_V1_2]
FEATURE [Sketcher::SketchObject] Sketch132
  Placement = pos=(0,-28,21.1) rot=(0,0,1;3.14159rad)
  sketch-geometry (4):
    g0: LineSegment StartX=-16.9 StartY=9.5 StartZ=0 EndX=16.9 EndY=9.5 EndZ=0
    g1: LineSegment StartX=16.9 StartY=9.5 StartZ=0 EndX=16.9 EndY=-24.5 EndZ=0
    g2: LineSegment StartX=16.9 StartY=-24.5 StartZ=0 EndX=-16.9 EndY=-24.5 EndZ=0
    g3: LineSegment StartX=-16.9 StartY=-24.5 StartZ=0 EndX=-16.9 EndY=9.5 EndZ=0
  constraints (12):
    c: Coincident(g0,g1)
    c: Coincident(g1,g2)
    c: Coincident(g2,g3)
    c: Coincident(g3,g0)
    c: Horizontal(g0)
    c: Horizontal(g2)
    c: Vertical(g1)
    c: Vertical(g3)
    c: Symmetric(g0,g0,g-2)
    c: DistanceX(g0,g0) = 33.8
    c: DistanceY(g3,g3) = 34
    c: DistanceY(g-1,g0) = 9.5
FEATURE [PartDesign::Pad] Pad031
  Length = 1.6
  Length2 = 100
  Placement = pos=(0,-28,21.1) rot=(0,0,1;3.14159rad)
  Sketch = -> Sketch132
  Type = 0
FEATURE [Sketcher::SketchObject] Sketch133
  Placement = pos=(0,-28,22.7) rot=(0,0,1;3.14159rad)
  Support = -> Pad031 [Face6]
  sketch-geometry (4):
    g0: LineSegment StartX=-16.5 StartY=7 StartZ=0 EndX=16.5 EndY=7 EndZ=0
    g1: LineSegment StartX=16.5 StartY=7 StartZ=0 EndX=16.5 EndY=-24 EndZ=0
    g2: LineSegment StartX=16.5 StartY=-24 StartZ=0 EndX=-16.5 EndY=-24 EndZ=0
    g3: LineSegment StartX=-16.5 StartY=-24 StartZ=0 EndX=-16.5 EndY=7 EndZ=0
  constraints (12):
    c: Coincident(g0,g1)
    c: Coincident(g1,g2)
    c: Coincident(g2,g3)
    c: Coincident(g3,g0)
    c: Horizontal(g0)
    c: Horizontal(g2)
    c: Vertical(g1)
    c: Vertical(g3)
    c: Symmetric(g0,g0,g-2)
    c: DistanceX(g2,g2) = 33
    c: DistanceY(g1,g1) = 31
    c: DistanceY(g-1,g0) = 7
FEATURE [PartDesign::Pad] Pad001  label="Pad003"
  Length = 0.2
  Length2 = 100
  Placement = pos=(0,-28,21.1) rot=(0,0,1;3.14159rad)
  Sketch = -> Sketch133
  Type = 0
FEATURE [Sketcher::SketchObject] Sketch002
  ExternalGeometry = -> [Pad001]
  Placement = pos=(-16.9,-28,21.1) rot=(-0.57735,0.57735,0.57735;4.18879rad)
  Support = -> Pad001 [Face3]
  sketch-geometry (4):
    g0: LineSegment StartX=9.5 StartY=0 StartZ=0 EndX=7.5 EndY=0 EndZ=0
    g1: LineSegment StartX=7.5 StartY=0 StartZ=0 EndX=7.5 EndY=0.5 EndZ=0
    g2: LineSegment StartX=7.5 StartY=0.5 StartZ=0 EndX=9.5 EndY=0.5 EndZ=0
    g3: LineSegment StartX=9.5 StartY=0.5 StartZ=0 EndX=9.5 EndY=0 EndZ=0
  constraints (11):
    c: Coincident(g0,g1)
    c: Coincident(g1,g2)
    c: Coincident(g2,g3)
    c: Coincident(g3,g0)
    c: Horizontal(g0)
    c: Horizontal(g2)
    c: Vertical(g1)
    c: Vertical(g3)
    c: Coincident(g0,g-4)
    c: DistanceX(g2,g2) = 2
    c: DistanceY(g1,g1) = 0.5
FEATURE [PartDesign::Pocket] Pocket034
  Length = 5
  Placement = pos=(0,-28,21.1) rot=(0,0,1;3.14159rad)
  Sketch = -> Sketch002
  Type = 1
FEATURE [Sketcher::SketchObject] Sketch003
  Placement = pos=(0,-28,21) rot=(-0.707107,0,0.707107;3.14159rad)
  sketch-geometry (8):
    g0: LineSegment StartX=-0.44 StartY=7.5 StartZ=0 EndX=-0.44 EndY=10.5 EndZ=0
    g1: LineSegment StartX=-0.44 StartY=7.5 StartZ=0 EndX=-0.5 EndY=7.5 EndZ=0
    g2: LineSegment StartX=-0.5 StartY=7.5 StartZ=0 EndX=-0.5 EndY=10.5 EndZ=0
    g3: ArcOfCircle CenterX=1.03 CenterY=10.5 CenterZ=0 NormalX=0 NormalY=0 NormalZ=1 Radius=1.47 StartAngle=1.05758e-05 EndAngle=3.14159
    g4: ArcOfCircle CenterX=1.03 CenterY=10.5 CenterZ=0 NormalX=0 NormalY=0 NormalZ=1 Radius=1.53 StartAngle=6.28318 EndAngle=9.42478
    g5: LineSegment StartX=2.5 StartY=10.5 StartZ=0 EndX=2.5 EndY=2.50002 EndZ=0
    g6: LineSegment StartX=2.56 StartY=10.5 StartZ=0 EndX=2.56 EndY=2.50002 EndZ=0
    g7: LineSegment StartX=2.5 StartY=2.50002 StartZ=0 EndX=2.56 EndY=2.50002 EndZ=0
  constraints (25):
    c: Vertical(g0)
    c: DistanceY(g-1,g0) = 7.5
    c: Coincident(g1,g0)
    c: Vertical(g2)
    c: Coincident(g1,g2)
    c: Horizontal(g1)
    c: DistanceX(g0) = -0.44
    c: DistanceX(g1,g1) = 0.06
    c: Equal(g2,g0)
    c: DistanceY(g2,g2) = 3
    c: Coincident(g4,g3)
    c: Coincident(g3,g0)
    c: Tangent(g3,g0)
    c: Coincident(g4,g2)
    c: DistanceX(g0,g3) = 2.94
    c: Coincident(g5,g3)
    c: Vertical(g5)
    c: DistanceY(g5,g5) = 8
    c: Tangent(g5,g3)
    c: Vertical(g6)
    c: Coincident(g4,g6)
    c: Tangent(g4,g6)
    c: Coincident(g7,g5)
    c: Horizontal(g7)
    c: Coincident(g6,g7)
FEATURE [PartDesign::Pad] Pad032  label="Pad004"
  Length = 14
  Length2 = 14
  Placement = pos=(0,-28,21) rot=(-0.707107,0,0.707107;3.14159rad)
  Sketch = -> Sketch003
  Type = 4
FEATURE [Sketcher::SketchObject] Sketch004
  ExternalGeometry = -> [Pad032]
  Placement = pos=(0,-28,18.44) rot=(-0.707107,0.707107,0;3.14159rad)
  Support = -> Pad032 [Face5]
  sketch-geometry (8):
    g0: LineSegment StartX=2.50002 StartY=7.75 StartZ=0 EndX=4.50002 EndY=7.75 EndZ=0
    g1: LineSegment StartX=4.50002 StartY=-7.75 StartZ=0 EndX=2.50002 EndY=-7.75 EndZ=0
    g2: LineSegment StartX=4.50002 StartY=7.75 StartZ=0 EndX=7.50002 EndY=14 EndZ=0
    g3: LineSegment StartX=2.50002 StartY=14 StartZ=0 EndX=2.50002 EndY=7.75 EndZ=0
    g4: LineSegment StartX=2.50002 StartY=14 StartZ=0 EndX=7.50002 EndY=14 EndZ=0
    g5: LineSegment StartX=2.50002 StartY=-7.75 StartZ=0 EndX=2.50002 EndY=-14 EndZ=0
    g6: LineSegment StartX=4.50002 StartY=-7.75 StartZ=0 EndX=7.50002 EndY=-14 EndZ=0
    g7: LineSegment StartX=7.50002 StartY=-14 StartZ=0 EndX=2.50002 EndY=-14 EndZ=0
  constraints (20):
    c: Horizontal(g0)
    c: Horizontal(g1)
    c: Symmetric(g1,g0,g-1)
    c: Equal(g0,g1)
    c: DistanceX(g0,g0) = 2
    c: DistanceY(g1,g0) = 15.5
    c: Coincident(g3,g0)
    c: Coincident(g4,g2)
    c: Horizontal(g4)
    c: Coincident(g5,g1)
    c: Coincident(g6,g1)
    c: Coincident(g7,g6)
    c: Coincident(g7,g5)
    c: Coincident(g0,g2)
    c: Coincident(g3,g4)
    c: Coincident(g5,g-3)
    c: PointOnObject(g1,g-3)
    c: DistanceX(g7,g7) = 5
    c: Coincident(g3,g-3)
    c: Equal(g4,g7)
FEATURE [PartDesign::Pocket] Pocket001
  Length = 0
  Placement = pos=(0,-28,21) rot=(-0.707107,0,0.707107;3.14159rad)
  Sketch = -> Sketch004
  Type = 2
FEATURE [Part::Feature] Part__Feature024  label="Conn"
  Placement = pos=(0,-4,20) rot=(-1,0,0;1.5708rad)
  shape: bbox 21.6 x 6.6 x 2.05 mm, 1015 faces (baked)
FEATURE [App::DocumentObjectGroup] Groupe  label="Ecran"
  Group = -> [Pad031,Pad001,Pad032,Part__Feature024,Pocket034,Pocket001]
FEATURE [Part::Feature] Part__Feature  label="690157000672"
  shape: bbox 10.65 x 5 x 7 mm, 128 faces (baked)
FEATURE [Part::Feature] Part__Feature025  label="690157000672_Cover"
  Placement = pos=(0,0,-1.55) rot=(0,0,1;0rad)
  shape: bbox 11.05 x 5 x 5.15 mm, 84 faces (baked)
FEATURE [Part::Feature] Part__Feature026  label="Pin"
  Placement = pos=(-3.175,-0.75,0.4) rot=(0,0,1;0rad)
  shape: bbox 2 x 0.4 x 4.95 mm, 36 faces (baked)
FEATURE [Part::Feature] Part__Feature027  label="Pin001"
  Placement = pos=(-1.905,0.75,0.4) rot=(0,0,1;0rad)
  shape: bbox 2 x 0.4 x 4.95 mm, 36 faces (baked)
FEATURE [Part::Feature] Part__Feature028  label="Pin002"
  Placement = pos=(-0.635,-0.75,0.4) rot=(0,0,1;0rad)
  shape: bbox 2 x 0.4 x 4.95 mm, 36 faces (baked)
FEATURE [Part::Feature] Part__Feature029  label="Pin003"
  Placement = pos=(0.635,0.75,0.4) rot=(0,0,1;0rad)
  shape: bbox 2 x 0.4 x 4.95 mm, 36 faces (baked)
FEATURE [Part::Feature] Part__Feature030  label="Pin004"
  Placement = pos=(1.905,-0.75,0.4) rot=(0,0,1;0rad)
  shape: bbox 2 x 0.4 x 4.95 mm, 36 faces (baked)
FEATURE [Part::Feature] Part__Feature031  label="Pin005"
  Placement = pos=(3.175,0.75,0.4) rot=(0,0,1;0rad)
  shape: bbox 2 x 0.4 x 4.95 mm, 36 faces (baked)
FEATURE [Part::MultiFuse] Fusion004
  Placement = pos=(0,0,0) rot=(0,0.707107,0.707107;3.14159rad)
  Shapes = -> [Part__Feature,Part__Feature029,Part__Feature028,Part__Feature031,Part__Feature026,Part__Feature025,Part__Feature030,Part__Feature027]
FEATURE [Part::Feature] Part__Feature032  label="Geh\X2\00E4\X0\use"
  shape: bbox 9.62 x 5 x 5 mm, 208 faces (baked)
FEATURE [Part::Feature] Part__Feature033  label="Pin006"
  Placement = pos=(-3.175,0,1) rot=(0,0,1;3.14159rad)
  shape: bbox 0.55 x 7.9 x 5 mm, 56 faces (baked)
FEATURE [Part::Feature] Part__Feature034  label="Pin007"
  Placement = pos=(-0.635,0,1) rot=(0,0,1;3.14159rad)
  shape: bbox 0.55 x 7.9 x 5 mm, 56 faces (baked)
FEATURE [Part::Feature] Part__Feature035  label="Pin008"
  Placement = pos=(1.905,0,1) rot=(0,0,1;3.14159rad)
  shape: bbox 0.55 x 7.9 x 5 mm, 56 faces (baked)
FEATURE [Part::Feature] Part__Feature036  label="Pin_2"
  Placement = pos=(3.175,0,1) rot=(0,0,1;0rad)
  shape: bbox 0.55 x 7.9 x 5 mm, 61 faces (baked)
FEATURE [Part::Feature] Part__Feature037  label="Pin_003"
  Placement = pos=(0.635,0,1) rot=(0,0,1;0rad)
  shape: bbox 0.55 x 7.9 x 5 mm, 61 faces (baked)
FEATURE [Part::Feature] Part__Feature038  label="Pin_004"
  Placement = pos=(-1.905,0,1) rot=(0,0,1;0rad)
  shape: bbox 0.55 x 7.9 x 5 mm, 61 faces (baked)
FEATURE [Part::MultiFuse] Fusion005
  Placement = pos=(0,5.2,0) rot=(1,0,0;1.5708rad)
  Shapes = -> [Part__Feature032,Part__Feature038,Part__Feature037,Part__Feature036,Part__Feature035,Part__Feature034,Part__Feature033]
FEATURE [Part::FeaturePython] Clone094  label="WurthMaleG"  # Draft clone (typed FeaturePython)
  Objects = -> [Fusion004]
  Placement = pos=(-13.5,8,16.7) rot=(0,0.707107,0.707107;3.14159rad)
  Scale = (1,1,1)
FEATURE [Part::FeaturePython] Clone095  label="WurthEmbG"  # Draft clone (typed FeaturePython)
  Objects = -> [Fusion005]
  Placement = pos=(-13.5,13.2,16.7) rot=(1,0,0;1.5708rad)
  Scale = (1,1,1)
FEATURE [App::DocumentObjectGroup] Groupe045  label="Moteurs"
  Group = -> [Part__Feature001,Clone001]
FEATURE [App::DocumentObjectGroup] Groupe003  label="Motorisation"
  Group = -> [Groupe006,Groupe045]
FEATURE [Part::FeaturePython] Clone096  label="WurthEmbD"  # Draft clone (typed FeaturePython)
  Objects = -> [Clone095]
  Placement = pos=(13.5,13.2,16.7) rot=(1,0,0;1.5708rad)
  Scale = (1,1,1)
FEATURE [Part::FeaturePython] Clone097  label="WurthMaleD"  # Draft clone (typed FeaturePython)
  Objects = -> [Clone094]
  Placement = pos=(13.5,8,16.7) rot=(0,0.707107,0.707107;3.14159rad)
  Scale = (1,1,1)
FEATURE [Part::Feature] BBL_103_G_E
  Placement = pos=(-14.04,31.5,15.27) rot=(0,-0.707107,0.707107;3.14159rad)
  shape: bbox 7.62 x 2.438 x 7.62 mm, 52 faces, 0 solids (baked)
FEATURE [Part::Feature] SL_103_G_11
  Placement = pos=(-14.04,31.5,17.7592) rot=(0,-0.707107,0.707107;3.14159rad)
  shape: bbox 7.849 x 2.54 x 6.096 mm, 76 faces, 0 solids (baked)
FEATURE [Part::MultiFuse] Fusion  label="STM"
  Placement = pos=(2.97056,29.0294,21) rot=(-0.281085,0.678598,0.678598;3.68962rad)
FEATURE [Part::FeaturePython] Clone099  label="Clone of SL_103_G_11"  # Draft clone (typed FeaturePython)
  Objects = -> [SL_103_G_11]
  Placement = pos=(-14,-35.5,17.7592) rot=(0,-0.707107,0.707107;3.14159rad)
  Scale = (1,1,1)
FEATURE [Part::FeaturePython] Clone100  label="Clone of BBL_103_G_E"  # Draft clone (typed FeaturePython)
  Objects = -> [BBL_103_G_E]
  Placement = pos=(-14,-35.5,15.27) rot=(0,-0.707107,0.707107;3.14159rad)
  Scale = (1,1,1)
FEATURE [App::DocumentObjectGroup] Groupe046  label="Samtec"
  Group = -> [BBL_103_G_E,SL_103_G_11,Clone099,Clone100]
FEATURE [App::DocumentObjectGroup] Groupe049  label="STM32"
  Group = -> [Fusion]
FEATURE [App::DocumentObjectGroup] Groupe048  label="Composants"
  Group = -> [Groupe,Groupe049]
FEATURE [Part::Feature] Part__Feature040  label="User Library-Vis FS"
  shape: bbox 3.5 x 3 x 3.5 mm, 16 faces (baked)
FEATURE [Part::FeaturePython] Clone109  label="Clone of User Library-Vis FS001"  # Draft clone (typed FeaturePython)
  Objects = -> [Part__Feature040]
  Placement = pos=(0,21.5,13.9766) rot=(-1,0,0;1.5708rad)
  Scale = (1,1,1)
FEATURE [Part::FeaturePython] Clone110  label="Clone of User Library-Vis FS002"  # Draft clone (typed FeaturePython)
  Objects = -> [Part__Feature040]
  Placement = pos=(-4.25,25,13.9766) rot=(-1,0,0;1.5708rad)
  Scale = (1,1,1)
FEATURE [Part::FeaturePython] Clone111  label="Clone of User Library-Vis FS003"  # Draft clone (typed FeaturePython)
  Objects = -> [Part__Feature040]
  Placement = pos=(4.25,25,13.9766) rot=(-1,0,0;1.5708rad)
  Scale = (1,1,1)
FEATURE [Part::FeaturePython] Clone112  label="Clone of User Library-Vis FS004"  # Draft clone (typed FeaturePython)
  Objects = -> [Part__Feature040]
  Placement = pos=(0,28.5,13.9766) rot=(-1,0,0;1.5708rad)
  Scale = (1,1,1)
FEATURE [Part::FeaturePython] Clone119  label="Clone of Fusion009"  # WARN: FeaturePython — macro-defined, semantics opaque (R4)
  Placement = pos=(-4.25,-25,-10.1) rot=(0,0,1;0rad)
  Scale = (1,1,1)
FEATURE [App::DocumentObjectGroup] Impeller_5  label="Impeller_5.0.0"
  Group = -> [Pad013,Pocket021,Pocket022,Pad014,PolarPattern010,Clone034,Part__Mirroring001,Clone119]
FEATURE [Part::Mirroring] Part__Mirroring  label="Clone of User Library-Vis FS001 (Mirror #8)"
  Base = (0,0,0)
  Normal = (0,1,0)
  Source = -> Clone109
FEATURE [Part::Mirroring] Part__Mirroring008  label="Clone of User Library-Vis FS002 (Mirror #9)"
  Base = (0,0,0)
  Normal = (0,1,0)
  Source = -> Clone110
FEATURE [Part::Mirroring] Part__Mirroring009  label="Clone of User Library-Vis FS003 (Mirror #10)"
  Base = (0,0,0)
  Normal = (0,1,0)
  Source = -> Clone111
FEATURE [Part::Mirroring] Part__Mirroring010  label="Clone of User Library-Vis FS004 (Mirror #11)"
  Base = (0,0,0)
  Normal = (0,1,0)
  Source = -> Clone112
FEATURE [App::DocumentObjectGroup] Groupe051  label="Vis001"
  Group = -> [Part__Feature040,Clone109,Clone110,Clone111,Clone112,Part__Mirroring,Part__Mirroring008,Part__Mirroring009,Part__Mirroring010]
FEATURE [Sketcher::SketchObject] Sketch246
  Placement = pos=(0,0,9) rot=(0,0,1;0rad)
  sketch-geometry (48):
    g0: LineSegment StartX=0 StartY=54 StartZ=0 EndX=-10 EndY=54 EndZ=0
    g1: ArcOfCircle CenterX=-10 CenterY=44 CenterZ=0 NormalX=0 NormalY=0 NormalZ=1 Radius=10 StartAngle=1.5708 EndAngle=1.91693
    g2: ArcOfCircle CenterX=-10 CenterY=44 CenterZ=0 NormalX=0 NormalY=0 NormalZ=1 Radius=10 StartAngle=1.91693 EndAngle=2.12897
    g3: ArcOfCircle CenterX=-10 CenterY=44 CenterZ=0 NormalX=0 NormalY=0 NormalZ=1 Radius=10 StartAngle=2.12897 EndAngle=2.35619
    g4: LineSegment StartX=-17.0711 StartY=51.0711 StartZ=0 EndX=-20.8998 EndY=47.2423 EndZ=0
    g5: LineSegment StartX=-20.8998 StartY=47.2423 StartZ=0 EndX=-22.5674 EndY=45.5747 EndZ=0
    g6: LineSegment StartX=-22.5674 StartY=45.5747 StartZ=0 EndX=-23.564 EndY=44.5782 EndZ=0
    g7: LineSegment StartX=-23.564 StartY=44.5782 StartZ=0 EndX=-24.9782 EndY=43.164 EndZ=0
    g8: LineSegment StartX=-24.9782 StartY=43.164 StartZ=0 EndX=-29.755 EndY=38.3872 EndZ=0
    g9: LineSegment StartX=-29.755 StartY=38.3872 StartZ=0 EndX=-31.5747 EndY=36.5674 EndZ=0
    g10: LineSegment StartX=-31.5747 StartY=36.5674 StartZ=0 EndX=-33.8388 EndY=34.3033 EndZ=0
    g11: ArcOfCircle CenterX=-31.0355 CenterY=31.5 CenterZ=0 NormalX=0 NormalY=0 NormalZ=1 Radius=3.96447 StartAngle=2.35619 EndAngle=3.14159
    g12: LineSegment StartX=-35 StartY=31.5 StartZ=0 EndX=-35 EndY=30 EndZ=0
    g13: ArcOfCircle CenterX=-31 CenterY=30 CenterZ=0 NormalX=0 NormalY=0 NormalZ=1 Radius=4 StartAngle=3.14159 EndAngle=3.43027
    g14: LineSegment StartX=-34.8345 StartY=28.8612 StartZ=0 EndX=-33.9452 EndY=28.9547 EndZ=0
    g15: LineSegment StartX=-33.9452 StartY=28.9547 StartZ=0 EndX=-32.3011 EndY=29.1275 EndZ=0
    g16: LineSegment StartX=-32.3011 StartY=29.1275 StartZ=0 EndX=-27.3284 EndY=29.6502 EndZ=0
    g17: LineSegment StartX=-27.3284 StartY=29.6502 StartZ=0 EndX=-25.6762 EndY=29.8238 EndZ=0
    g18: LineSegment StartX=-25.6762 StartY=29.8238 StartZ=0 EndX=-20.1421 EndY=35.3579 EndZ=0
    g19: LineSegment StartX=-20.1421 StartY=35.3579 StartZ=0 EndX=-19.7178 EndY=35.7822 EndZ=0
    g20: LineSegment StartX=-19.7178 StartY=35.7822 StartZ=0 EndX=-16.1822 EndY=39.3178 EndZ=0
    g21: LineSegment StartX=-16.1822 StartY=39.3178 StartZ=0 EndX=-6.68224 EndY=48.8178 EndZ=0
    g22: LineSegment StartX=-6.68224 StartY=48.8178 StartZ=0 EndX=-6 EndY=49.5 EndZ=0
    g23: LineSegment StartX=-6 StartY=49.5 StartZ=0 EndX=0 EndY=49.5 EndZ=0
    g24: LineSegment StartX=0 StartY=49.5 StartZ=0 EndX=6 EndY=49.5 EndZ=0
    g25: LineSegment StartX=6 StartY=49.5 StartZ=0 EndX=6.68224 EndY=48.8178 EndZ=0
    g26: LineSegment StartX=6.68224 StartY=48.8178 StartZ=0 EndX=16.1822 EndY=39.3178 EndZ=0
    g27: LineSegment StartX=16.1822 StartY=39.3178 StartZ=0 EndX=19.7178 EndY=35.7822 EndZ=0
    g28: LineSegment StartX=19.7178 StartY=35.7822 StartZ=0 EndX=20.1421 EndY=35.3579 EndZ=0
    g29: LineSegment StartX=20.1421 StartY=35.3579 StartZ=0 EndX=25.6762 EndY=29.8238 EndZ=0
    g30: LineSegment StartX=25.6762 StartY=29.8238 StartZ=0 EndX=27.3284 EndY=29.6502 EndZ=0
    g31: LineSegment StartX=27.3284 StartY=29.6502 StartZ=0 EndX=32.3011 EndY=29.1275 EndZ=0
    g32: LineSegment StartX=32.3011 StartY=29.1275 StartZ=0 EndX=33.9452 EndY=28.9547 EndZ=0
    g33: LineSegment StartX=33.9452 StartY=28.9547 StartZ=0 EndX=34.8345 EndY=28.8612 EndZ=0
    g34: ArcOfCircle CenterX=31 CenterY=30 CenterZ=0 NormalX=0 NormalY=0 NormalZ=1 Radius=4 StartAngle=5.9945 EndAngle=6.28318
    g35: LineSegment StartX=35 StartY=30 StartZ=0 EndX=35 EndY=31.5 EndZ=0
    g36: ArcOfCircle CenterX=31.0355 CenterY=31.5 CenterZ=0 NormalX=0 NormalY=0 NormalZ=1 Radius=3.96447 StartAngle=2.02129e-07 EndAngle=0.785398
    g37: LineSegment StartX=33.8388 StartY=34.3033 StartZ=0 EndX=31.5747 EndY=36.5674 EndZ=0
    g38: LineSegment StartX=31.5747 StartY=36.5674 StartZ=0 EndX=29.755 EndY=38.3872 EndZ=0
    g39: LineSegment StartX=29.755 StartY=38.3872 StartZ=0 EndX=24.9782 EndY=43.164 EndZ=0
    g40: LineSegment StartX=24.9782 StartY=43.164 StartZ=0 EndX=23.564 EndY=44.5782 EndZ=0
    g41: LineSegment StartX=23.564 StartY=44.5782 StartZ=0 EndX=22.5674 EndY=45.5747 EndZ=0
    g42: LineSegment StartX=22.5674 StartY=45.5747 StartZ=0 EndX=20.8998 EndY=47.2423 EndZ=0
    g43: LineSegment StartX=20.8998 StartY=47.2423 StartZ=0 EndX=17.0711 EndY=51.0711 EndZ=0
    g44: ArcOfCircle CenterX=10 CenterY=44 CenterZ=0 NormalX=0 NormalY=0 NormalZ=1 Radius=10 StartAngle=0.785398 EndAngle=1.01262
    g45: ArcOfCircle CenterX=10 CenterY=44 CenterZ=0 NormalX=0 NormalY=0 NormalZ=1 Radius=10 StartAngle=1.01262 EndAngle=1.22466
    g46: ArcOfCircle CenterX=10 CenterY=44 CenterZ=0 NormalX=0 NormalY=0 NormalZ=1 Radius=10 StartAngle=1.22466 EndAngle=1.5708
    g47: LineSegment StartX=10 StartY=54 StartZ=0 EndX=0 EndY=54 EndZ=0
FEATURE [PartDesign::Pad] Pad
  Length = 1
  Length2 = 100
  Placement = pos=(0,0,9) rot=(0,0,1;0rad)
  Sketch = -> Sketch246
  Type = 0
FEATURE [Sketcher::SketchObject] Sketch249
  Placement = pos=(0,0,10) rot=(0,0,1;0rad)
  Support = -> Pad [Face50]
  sketch-geometry (171):
    g0: LineSegment StartX=-14.4624 StartY=42.1641 StartZ=0 EndX=-14.4174 EndY=42.3589 EndZ=0
    g1: LineSegment StartX=-14.4174 StartY=42.3589 StartZ=0 EndX=-19.2892 EndY=43.4837 EndZ=0
    g2: LineSegment StartX=-19.2892 StartY=43.4837 StartZ=0 EndX=-19.2253 EndY=43.7609 EndZ=0
    g3: ArcOfCircle CenterX=-17.7975 CenterY=45.4998 CenterZ=0 NormalX=0 NormalY=0 NormalZ=1 Radius=2.25 StartAngle=3.37526 EndAngle=4.02494
    g4: LineSegment StartX=-19.9863 StartY=44.9788 StartZ=0 EndX=-22.5674 EndY=45.5747 EndZ=0
    g5: LineSegment StartX=-22.5674 StartY=45.5747 StartZ=0 EndX=-23.564 EndY=44.5782 EndZ=0
    g6: LineSegment StartX=-23.564 StartY=44.5782 StartZ=0 EndX=-22.0465 EndY=43.0608 EndZ=0
    g7: ArcOfCircle CenterX=-21.3284 CenterY=40.9284 CenterZ=0 NormalX=0 NormalY=0 NormalZ=1 Radius=2.25 StartAngle=1.24595 EndAngle=1.89564
    g8: LineSegment StartX=-20.6103 StartY=43.0608 StartZ=0 EndX=-20.4092 EndY=43.2619 EndZ=0
    g9: LineSegment StartX=-20.4092 StartY=43.2619 StartZ=0 EndX=-16.8737 EndY=39.7263 EndZ=0
    g10: LineSegment StartX=-16.8737 StartY=39.7263 StartZ=0 EndX=-16.7322 EndY=39.8678 EndZ=0
    g11: LineSegment StartX=-16.7322 StartY=39.8678 StartZ=0 EndX=-16.3787 EndY=39.5142 EndZ=0
    g12: LineSegment StartX=-16.3787 StartY=39.5142 StartZ=0 EndX=-16.1822 EndY=39.3178 EndZ=0
    g13: LineSegment StartX=-16.1822 StartY=39.3178 StartZ=0 EndX=-13.5472 EndY=41.9528 EndZ=0
    g14: LineSegment StartX=-13.5472 StartY=41.9528 StartZ=0 EndX=-13.9752 EndY=42.0516 EndZ=0
    g15: LineSegment StartX=-13.9752 StartY=42.0516 StartZ=0 EndX=-14.4624 EndY=42.1641 EndZ=0
    g16: LineSegment StartX=-23.6619 StartY=40.0092 StartZ=0 EndX=-23.4608 EndY=40.2103 EndZ=0
    g17: ArcOfCircle CenterX=-21.3284 CenterY=40.9284 CenterZ=0 NormalX=0 NormalY=0 NormalZ=1 Radius=2.25 StartAngle=2.81675 EndAngle=3.46643
    g18: LineSegment StartX=-23.4608 StartY=41.6465 StartZ=0 EndX=-24.9782 EndY=43.164 EndZ=0
    g19: LineSegment StartX=-24.9782 StartY=43.164 StartZ=0 EndX=-29.755 EndY=38.3872 EndZ=0
    g20: LineSegment StartX=-29.755 StartY=38.3872 StartZ=0 EndX=-29.5343 EndY=36.2871 EndZ=0
    g21: ArcOfCircle CenterX=-30.3181 CenterY=34.1781 CenterZ=0 NormalX=0 NormalY=0 NormalZ=1 Radius=2.25 StartAngle=0.56527 EndAngle=1.21496
    g22: LineSegment StartX=-28.4181 StartY=35.3833 StartZ=0 EndX=-28.1352 EndY=35.413 EndZ=0
    g23: LineSegment StartX=-28.1352 StartY=35.413 StartZ=0 EndX=-27.6126 EndY=30.4404 EndZ=0
    g24: LineSegment StartX=-27.6126 StartY=30.4404 StartZ=0 EndX=-27.4137 EndY=30.4613 EndZ=0
    g25: LineSegment StartX=-27.4137 StartY=30.4613 StartZ=0 EndX=-27.3614 EndY=29.964 EndZ=0
    g26: LineSegment StartX=-27.3614 StartY=29.964 StartZ=0 EndX=-27.3284 EndY=29.6502 EndZ=0
    g27: LineSegment StartX=-27.3284 StartY=29.6502 StartZ=0 EndX=-25.6762 EndY=29.8238 EndZ=0
    g28: LineSegment StartX=-25.6762 StartY=29.8238 StartZ=0 EndX=-20.1421 EndY=35.3579 EndZ=0
    g29: LineSegment StartX=-20.1421 StartY=35.3579 StartZ=0 EndX=-19.7178 EndY=35.7822 EndZ=0
    g30: LineSegment StartX=-19.7178 StartY=35.7822 StartZ=0 EndX=-19.9142 EndY=35.9787 EndZ=0
    g31: LineSegment StartX=-19.9142 StartY=35.9787 StartZ=0 EndX=-20.2678 EndY=36.3322 EndZ=0
    g32: LineSegment StartX=-20.2678 StartY=36.3322 StartZ=0 EndX=-20.1263 EndY=36.4737 EndZ=0
    g33: LineSegment StartX=-20.1263 StartY=36.4737 StartZ=0 EndX=-23.6619 EndY=40.0092 EndZ=0
    g34: LineSegment StartX=-12.8504 StartY=46.9234 StartZ=0 EndX=-13.3376 EndY=47.0359 EndZ=0
    g35: LineSegment StartX=-13.3376 StartY=47.0359 StartZ=0 EndX=-13.3826 EndY=46.8411 EndZ=0
    g36: LineSegment StartX=-13.3826 StartY=46.8411 StartZ=0 EndX=-18.2545 EndY=47.9658 EndZ=0
    g37: LineSegment StartX=-18.2545 StartY=47.9658 StartZ=0 EndX=-18.3184 EndY=47.6887 EndZ=0
    g38: ArcOfCircle CenterX=-17.7975 CenterY=45.4998 CenterZ=0 NormalX=0 NormalY=0 NormalZ=1 Radius=2.25 StartAngle=1.80446 EndAngle=2.45415
    g39: LineSegment StartX=-19.5364 StartY=46.9276 StartZ=0 EndX=-20.8998 EndY=47.2423 EndZ=0
    g40: LineSegment StartX=-20.8998 StartY=47.2423 StartZ=0 EndX=-17.0711 EndY=51.0711 EndZ=0
    g41: ArcOfCircle CenterX=-10 CenterY=44 CenterZ=0 NormalX=0 NormalY=0 NormalZ=1 Radius=10 StartAngle=2.12897 EndAngle=2.35619
    g42: LineSegment StartX=-15.2964 StartY=52.4822 StartZ=0 EndX=-13.9607 EndY=51.1466 EndZ=0
    g43: ArcOfCircle CenterX=-11.8284 CenterY=50.4284 CenterZ=0 NormalX=0 NormalY=0 NormalZ=1 Radius=2.25 StartAngle=2.81675 EndAngle=3.46643
    g44: LineSegment StartX=-13.9607 StartY=49.7103 StartZ=0 EndX=-14.1619 EndY=49.5092 EndZ=0
    g45: LineSegment StartX=-14.1619 StartY=49.5092 StartZ=0 EndX=-11.1936 EndY=46.5409 EndZ=0
    g46: LineSegment StartX=-11.1936 StartY=46.5409 StartZ=0 EndX=-11.3889 EndY=46.586 EndZ=0
    g47: LineSegment StartX=-11.3889 StartY=46.586 StartZ=0 EndX=-11.8761 EndY=46.6985 EndZ=0
    g48: LineSegment StartX=-11.8761 StartY=46.6985 StartZ=0 EndX=-12.3633 EndY=46.811 EndZ=0
    g49: LineSegment StartX=-12.3633 StartY=46.811 StartZ=0 EndX=-12.8504 EndY=46.9234 EndZ=0
    g50: LineSegment StartX=-32.3863 StartY=29.9387 StartZ=0 EndX=-32.1874 EndY=29.9596 EndZ=0
    g51: LineSegment StartX=-32.1874 StartY=29.9596 StartZ=0 EndX=-32.71 EndY=34.9322 EndZ=0
    g52: LineSegment StartX=-32.71 StartY=34.9322 StartZ=0 EndX=-32.4271 EndY=34.9619 EndZ=0
    g53: ArcOfCircle CenterX=-30.3181 CenterY=34.1781 CenterZ=0 NormalX=0 NormalY=0 NormalZ=1 Radius=2.25 StartAngle=2.13607 EndAngle=2.78575
    g54: LineSegment StartX=-31.5233 StartY=36.0781 StartZ=0 EndX=-31.5747 EndY=36.5674 EndZ=0
    g55: LineSegment StartX=-31.5747 StartY=36.5674 StartZ=0 EndX=-33.8388 EndY=34.3033 EndZ=0
    g56: ArcOfCircle CenterX=-31.0355 CenterY=31.5 CenterZ=0 NormalX=0 NormalY=0 NormalZ=1 Radius=3.96447 StartAngle=2.35619 EndAngle=3.14159
    g57: LineSegment StartX=-35 StartY=31.5 StartZ=0 EndX=-35 EndY=30 EndZ=0
    g58: ArcOfCircle CenterX=-31 CenterY=30 CenterZ=0 NormalX=0 NormalY=0 NormalZ=1 Radius=4 StartAngle=3.14159 EndAngle=3.43027
    g59: LineSegment StartX=-34.8345 StartY=28.8612 StartZ=0 EndX=-33.9452 EndY=28.9547 EndZ=0
    g60: LineSegment StartX=-33.9452 StartY=28.9547 StartZ=0 EndX=-32.3011 EndY=29.1275 EndZ=0
    g61: LineSegment StartX=-32.3011 StartY=29.1275 StartZ=0 EndX=-32.334 EndY=29.4414 EndZ=0
    g62: LineSegment StartX=-32.334 StartY=29.4414 StartZ=0 EndX=-32.3863 EndY=29.9387 EndZ=0
    g63: LineSegment StartX=14.4624 StartY=42.1641 StartZ=0 EndX=14.4174 EndY=42.3589 EndZ=0
    g64: LineSegment StartX=14.4174 StartY=42.3589 StartZ=0 EndX=19.2892 EndY=43.4837 EndZ=0
    g65: LineSegment StartX=19.2892 StartY=43.4837 StartZ=0 EndX=19.2253 EndY=43.7609 EndZ=0
    g66: ArcOfCircle CenterX=17.7975 CenterY=45.4998 CenterZ=0 NormalX=0 NormalY=0 NormalZ=1 Radius=2.25 StartAngle=5.39984 EndAngle=6.04952
    g67: LineSegment StartX=19.9863 StartY=44.9788 StartZ=0 EndX=22.5674 EndY=45.5747 EndZ=0
    g68: LineSegment StartX=22.5674 StartY=45.5747 StartZ=0 EndX=23.564 EndY=44.5782 EndZ=0
    g69: LineSegment StartX=23.564 StartY=44.5782 StartZ=0 EndX=22.0465 EndY=43.0608 EndZ=0
    g70: ArcOfCircle CenterX=21.3284 CenterY=40.9284 CenterZ=0 NormalX=0 NormalY=0 NormalZ=1 Radius=2.25 StartAngle=1.24595 EndAngle=1.89564
    g71: LineSegment StartX=20.6103 StartY=43.0608 StartZ=0 EndX=20.4092 EndY=43.2619 EndZ=0
    g72: LineSegment StartX=20.4092 StartY=43.2619 StartZ=0 EndX=16.8737 EndY=39.7263 EndZ=0
    g73: LineSegment StartX=16.8737 StartY=39.7263 StartZ=0 EndX=16.7322 EndY=39.8678 EndZ=0
    g74: LineSegment StartX=16.7322 StartY=39.8678 StartZ=0 EndX=16.3787 EndY=39.5142 EndZ=0
    g75: LineSegment StartX=16.3787 StartY=39.5142 StartZ=0 EndX=16.1822 EndY=39.3178 EndZ=0
    g76: LineSegment StartX=16.1822 StartY=39.3178 StartZ=0 EndX=13.5472 EndY=41.9528 EndZ=0
    g77: LineSegment StartX=13.5472 StartY=41.9528 StartZ=0 EndX=13.9752 EndY=42.0516 EndZ=0
    g78: LineSegment StartX=13.9752 StartY=42.0516 StartZ=0 EndX=14.4624 EndY=42.1641 EndZ=0
    g79: LineSegment StartX=23.6619 StartY=40.0092 StartZ=0 EndX=23.4608 EndY=40.2103 EndZ=0
    g80: ArcOfCircle CenterX=21.3284 CenterY=40.9284 CenterZ=0 NormalX=0 NormalY=0 NormalZ=1 Radius=2.25 StartAngle=5.95834 EndAngle=6.60803
    g81: LineSegment StartX=23.4608 StartY=41.6465 StartZ=0 EndX=24.9782 EndY=43.164 EndZ=0
    g82: LineSegment StartX=24.9782 StartY=43.164 StartZ=0 EndX=29.755 EndY=38.3872 EndZ=0
    g83: LineSegment StartX=29.755 StartY=38.3872 StartZ=0 EndX=29.5343 EndY=36.2871 EndZ=0
    g84: ArcOfCircle CenterX=30.3181 CenterY=34.1781 CenterZ=0 NormalX=0 NormalY=0 NormalZ=1 Radius=2.25 StartAngle=1.92663 EndAngle=2.57632
    g85: LineSegment StartX=28.4181 StartY=35.3833 StartZ=0 EndX=28.1352 EndY=35.413 EndZ=0
    g86: LineSegment StartX=28.1352 StartY=35.413 StartZ=0 EndX=27.6126 EndY=30.4404 EndZ=0
    g87: LineSegment StartX=27.6126 StartY=30.4404 StartZ=0 EndX=27.4137 EndY=30.4613 EndZ=0
    g88: LineSegment StartX=27.4137 StartY=30.4613 StartZ=0 EndX=27.3614 EndY=29.964 EndZ=0
    g89: LineSegment StartX=27.3614 StartY=29.964 StartZ=0 EndX=27.3284 EndY=29.6502 EndZ=0
    g90: LineSegment StartX=27.3284 StartY=29.6502 StartZ=0 EndX=25.6762 EndY=29.8238 EndZ=0
    g91: LineSegment StartX=25.6762 StartY=29.8238 StartZ=0 EndX=20.1421 EndY=35.3579 EndZ=0
    g92: LineSegment StartX=20.1421 StartY=35.3579 StartZ=0 EndX=19.7178 EndY=35.7822 EndZ=0
    g93: LineSegment StartX=19.7178 StartY=35.7822 StartZ=0 EndX=19.9142 EndY=35.9787 EndZ=0
    g94: LineSegment StartX=19.9142 StartY=35.9787 StartZ=0 EndX=20.2678 EndY=36.3322 EndZ=0
    g95: LineSegment StartX=20.2678 StartY=36.3322 StartZ=0 EndX=20.1263 EndY=36.4737 EndZ=0
    g96: LineSegment StartX=20.1263 StartY=36.4737 StartZ=0 EndX=23.6619 EndY=40.0092 EndZ=0
    g97: LineSegment StartX=12.8504 StartY=46.9234 StartZ=0 EndX=13.3376 EndY=47.0359 EndZ=0
    g98: LineSegment StartX=13.3376 StartY=47.0359 StartZ=0 EndX=13.3826 EndY=46.8411 EndZ=0
    g99: LineSegment StartX=13.3826 StartY=46.8411 StartZ=0 EndX=18.2545 EndY=47.9658 EndZ=0
    g100: LineSegment StartX=18.2545 StartY=47.9658 StartZ=0 EndX=18.3184 EndY=47.6887 EndZ=0
    g101: ArcOfCircle CenterX=17.7975 CenterY=45.4998 CenterZ=0 NormalX=0 NormalY=0 NormalZ=1 Radius=2.25 StartAngle=0.687445 EndAngle=1.33714
    g102: LineSegment StartX=19.5364 StartY=46.9276 StartZ=0 EndX=20.8998 EndY=47.2423 EndZ=0
    g103: LineSegment StartX=20.8998 StartY=47.2423 StartZ=0 EndX=17.0711 EndY=51.0711 EndZ=0
    g104: ArcOfCircle CenterX=10 CenterY=44 CenterZ=0 NormalX=0 NormalY=0 NormalZ=1 Radius=10 StartAngle=0.785398 EndAngle=1.01262
    g105: LineSegment StartX=15.2964 StartY=52.4822 StartZ=0 EndX=13.9607 EndY=51.1466 EndZ=0
    g106: ArcOfCircle CenterX=11.8284 CenterY=50.4284 CenterZ=0 NormalX=0 NormalY=0 NormalZ=1 Radius=2.25 StartAngle=5.95835 EndAngle=6.60803
    g107: LineSegment StartX=13.9607 StartY=49.7103 StartZ=0 EndX=14.1619 EndY=49.5092 EndZ=0
    g108: LineSegment StartX=14.1619 StartY=49.5092 StartZ=0 EndX=11.1936 EndY=46.5409 EndZ=0
    g109: LineSegment StartX=11.1936 StartY=46.5409 StartZ=0 EndX=11.3889 EndY=46.586 EndZ=0
    g110: LineSegment StartX=11.3889 StartY=46.586 StartZ=0 EndX=11.8761 EndY=46.6985 EndZ=0
    g111: LineSegment StartX=11.8761 StartY=46.6985 StartZ=0 EndX=12.3633 EndY=46.811 EndZ=0
    g112: LineSegment StartX=12.3633 StartY=46.811 StartZ=0 EndX=12.8504 EndY=46.9234 EndZ=0
    g113: LineSegment StartX=32.3863 StartY=29.9387 StartZ=0 EndX=32.1874 EndY=29.9596 EndZ=0
    g114: LineSegment StartX=32.1874 StartY=29.9596 StartZ=0 EndX=32.71 EndY=34.9322 EndZ=0
    g115: LineSegment StartX=32.71 StartY=34.9322 StartZ=0 EndX=32.4271 EndY=34.9619 EndZ=0
    g116: ArcOfCircle CenterX=30.3181 CenterY=34.1781 CenterZ=0 NormalX=0 NormalY=0 NormalZ=1 Radius=2.25 StartAngle=0.355838 EndAngle=1.00552
    g117: LineSegment StartX=31.5233 StartY=36.0781 StartZ=0 EndX=31.5747 EndY=36.5674 EndZ=0
    g118: LineSegment StartX=31.5747 StartY=36.5674 StartZ=0 EndX=33.8388 EndY=34.3033 EndZ=0
    g119: ArcOfCircle CenterX=31.0355 CenterY=31.5 CenterZ=0 NormalX=0 NormalY=0 NormalZ=1 Radius=3.96447 StartAngle=2.02129e-07 EndAngle=0.785398
    g120: LineSegment StartX=35 StartY=31.5 StartZ=0 EndX=35 EndY=30 EndZ=0
    g121: ArcOfCircle CenterX=31 CenterY=30 CenterZ=0 NormalX=0 NormalY=0 NormalZ=1 Radius=4 StartAngle=5.9945 EndAngle=6.28318
    g122: LineSegment StartX=34.8345 StartY=28.8612 StartZ=0 EndX=33.9452 EndY=28.9547 EndZ=0
    g123: LineSegment StartX=33.9452 StartY=28.9547 StartZ=0 EndX=32.3011 EndY=29.1275 EndZ=0
    g124: LineSegment StartX=32.3011 StartY=29.1275 StartZ=0 EndX=32.334 EndY=29.4414 EndZ=0
    g125: LineSegment StartX=32.334 StartY=29.4414 StartZ=0 EndX=32.3863 EndY=29.9387 EndZ=0
    g126: ArcOfCircle CenterX=-21.3284 CenterY=40.9284 CenterZ=0 NormalX=0 NormalY=0 NormalZ=1 Radius=3.75 StartAngle=3.13786 EndAngle=3.24174
    g127: LineSegment StartX=-25.0784 StartY=40.9424 StartZ=0 EndX=-28.1884 EndY=37.8324 EndZ=0
    g128: LineSegment StartX=-28.1884 StartY=37.8324 StartZ=0 EndX=-28.124 EndY=37.2192 EndZ=0
    g129: ArcOfCircle CenterX=-30.3181 CenterY=34.1781 CenterZ=0 NormalX=0 NormalY=0 NormalZ=1 Radius=3.75 StartAngle=0.789965 EndAngle=0.945787
    g130: ArcOfCircle CenterX=-28.1352 CenterY=35.413 CenterZ=0 NormalX=0 NormalY=0 NormalZ=1 Radius=1.5 StartAngle=0.104716 EndAngle=1.26146
    g131: LineSegment StartX=-26.6434 StartY=35.5698 StartZ=0 EndX=-26.2067 EndY=31.4146 EndZ=0
    g132: LineSegment StartX=-26.2067 StartY=31.4146 StartZ=0 EndX=-21.7081 EndY=35.9133 EndZ=0
    g133: ArcOfCircle CenterX=-20.2678 CenterY=36.3322 CenterZ=0 NormalX=0 NormalY=0 NormalZ=1 Radius=1.49997 StartAngle=3.40467 EndAngle=3.42467
    g134: LineSegment StartX=-21.7162 StartY=35.9421 StartZ=0 EndX=-24.7225 EndY=38.9485 EndZ=0
    g135: ArcOfCircle CenterX=-23.6619 CenterY=40.0092 CenterZ=0 NormalX=0 NormalY=0 NormalZ=1 Radius=1.5 StartAngle=2.77024 EndAngle=3.92699
    g136: ArcOfCircle CenterX=21.3284 CenterY=40.9284 CenterZ=0 NormalX=0 NormalY=0 NormalZ=1 Radius=3.75 StartAngle=6.18304 EndAngle=6.28691
    g137: LineSegment StartX=25.0784 StartY=40.9424 StartZ=0 EndX=28.1884 EndY=37.8324 EndZ=0
    g138: LineSegment StartX=28.1884 StartY=37.8324 StartZ=0 EndX=28.124 EndY=37.2192 EndZ=0
    g139: ArcOfCircle CenterX=30.3181 CenterY=34.1781 CenterZ=0 NormalX=0 NormalY=0 NormalZ=1 Radius=3.75 StartAngle=2.19581 EndAngle=2.35163
    g140: ArcOfCircle CenterX=28.1352 CenterY=35.413 CenterZ=0 NormalX=0 NormalY=0 NormalZ=1 Radius=1.5 StartAngle=1.88013 EndAngle=3.03688
    g141: LineSegment StartX=26.6434 StartY=35.5698 StartZ=0 EndX=26.2067 EndY=31.4146 EndZ=0
    g142: LineSegment StartX=26.2067 StartY=31.4146 StartZ=0 EndX=21.7081 EndY=35.9133 EndZ=0
    g143: ArcOfCircle CenterX=20.2678 CenterY=36.3322 CenterZ=0 NormalX=0 NormalY=0 NormalZ=1 Radius=1.49997 StartAngle=6.0001 EndAngle=6.02011
    g144: LineSegment StartX=21.7162 StartY=35.9421 StartZ=0 EndX=24.7225 EndY=38.9485 EndZ=0
    g145: ArcOfCircle CenterX=23.6619 CenterY=40.0092 CenterZ=0 NormalX=0 NormalY=0 NormalZ=1 Radius=1.5 StartAngle=5.49779 EndAngle=6.65454
    g146: LineSegment StartX=7.23223 StartY=49.3678 StartZ=0 EndX=6.87867 EndY=49.0142 EndZ=0
    g147: LineSegment StartX=6.87867 StartY=49.0142 StartZ=0 EndX=6.68224 EndY=48.8178 EndZ=0
    g148: LineSegment StartX=6.68224 StartY=48.8178 StartZ=0 EndX=5.64645 EndY=49.8536 EndZ=0
    g149: LineSegment StartX=5.64645 StartY=49.8536 StartZ=0 EndX=8.29289 EndY=52.5 EndZ=0
    g150: LineSegment StartX=8.29289 StartY=52.5 StartZ=0 EndX=-8.29289 EndY=52.5 EndZ=0
    g151: LineSegment StartX=-8.29289 StartY=52.5 StartZ=0 EndX=-5.64645 EndY=49.8536 EndZ=0
    g152: LineSegment StartX=-5.64645 StartY=49.8536 StartZ=0 EndX=-6.68224 EndY=48.8178 EndZ=0
    g153: LineSegment StartX=-6.68224 StartY=48.8178 StartZ=0 EndX=-6.87867 EndY=49.0142 EndZ=0
    g154: LineSegment StartX=-6.87867 StartY=49.0142 StartZ=0 EndX=-7.23223 EndY=49.3678 EndZ=0
    g155: LineSegment StartX=-7.23223 StartY=49.3678 StartZ=0 EndX=-7.37365 EndY=49.2263 EndZ=0
    g156: LineSegment StartX=-7.37365 StartY=49.2263 StartZ=0 EndX=-10.9092 EndY=52.7619 EndZ=0
    g157: LineSegment StartX=-10.9092 StartY=52.7619 StartZ=0 EndX=-11.1103 EndY=52.5608 EndZ=0
    g158: ArcOfCircle CenterX=-11.8284 CenterY=50.4284 CenterZ=0 NormalX=0 NormalY=0 NormalZ=1 Radius=2.25 StartAngle=1.24595 EndAngle=1.89564
    g159: LineSegment StartX=-12.5465 StartY=52.5608 StartZ=0 EndX=-13.3927 EndY=53.4069 EndZ=0
    g160: ArcOfCircle CenterX=-10 CenterY=44 CenterZ=0 NormalX=0 NormalY=0 NormalZ=1 Radius=10 StartAngle=1.5708 EndAngle=1.91693
    g161: LineSegment StartX=-10 StartY=54 StartZ=0 EndX=0 EndY=54 EndZ=0
    g162: LineSegment StartX=0 StartY=54 StartZ=0 EndX=10 EndY=54 EndZ=0
    g163: ArcOfCircle CenterX=10 CenterY=44 CenterZ=0 NormalX=0 NormalY=0 NormalZ=1 Radius=10 StartAngle=1.22466 EndAngle=1.5708
    g164: LineSegment StartX=13.3927 StartY=53.4069 StartZ=0 EndX=12.5465 EndY=52.5608 EndZ=0
    g165: ArcOfCircle CenterX=11.8284 CenterY=50.4284 CenterZ=0 NormalX=0 NormalY=0 NormalZ=1 Radius=2.25 StartAngle=1.24595 EndAngle=1.89564
    g166: LineSegment StartX=11.1103 StartY=52.5608 StartZ=0 EndX=10.9092 EndY=52.7619 EndZ=0
    g167: LineSegment StartX=10.9092 StartY=52.7619 StartZ=0 EndX=7.37365 EndY=49.2263 EndZ=0
    g168: LineSegment StartX=7.37365 StartY=49.2263 StartZ=0 EndX=7.23223 EndY=49.3678 EndZ=0
    g169: Circle CenterX=-16 CenterY=49.5 CenterZ=0 NormalX=0 NormalY=0 NormalZ=1 Radius=0.75
    g170: Circle CenterX=16 CenterY=49.5 CenterZ=0 NormalX=0 NormalY=0 NormalZ=1 Radius=0.75
FEATURE [PartDesign::Pad] Pad039
  Length = 5
  Length2 = 100
  Placement = pos=(0,0,9) rot=(0,0,1;0rad)
  Sketch = -> Sketch249
  Type = 0
FEATURE [Sketcher::SketchObject] Sketch251
  Placement = pos=(0,0,15) rot=(0,0,1;0rad)
  Support = -> Pad039 [Face91]
  sketch-geometry (48):
    g0: LineSegment StartX=0 StartY=54 StartZ=0 EndX=-10 EndY=54 EndZ=0
    g1: ArcOfCircle CenterX=-10 CenterY=44 CenterZ=0 NormalX=0 NormalY=0 NormalZ=1 Radius=10 StartAngle=1.5708 EndAngle=1.91693
    g2: ArcOfCircle CenterX=-10 CenterY=44 CenterZ=0 NormalX=0 NormalY=0 NormalZ=1 Radius=10 StartAngle=1.91693 EndAngle=2.12897
    g3: ArcOfCircle CenterX=-10 CenterY=44 CenterZ=0 NormalX=0 NormalY=0 NormalZ=1 Radius=10 StartAngle=2.12897 EndAngle=2.35619
    g4: LineSegment StartX=-17.0711 StartY=51.0711 StartZ=0 EndX=-20.8998 EndY=47.2423 EndZ=0
    g5: LineSegment StartX=-20.8998 StartY=47.2423 StartZ=0 EndX=-22.5674 EndY=45.5747 EndZ=0
    g6: LineSegment StartX=-22.5674 StartY=45.5747 StartZ=0 EndX=-23.564 EndY=44.5782 EndZ=0
    g7: LineSegment StartX=-23.564 StartY=44.5782 StartZ=0 EndX=-24.9782 EndY=43.164 EndZ=0
    g8: LineSegment StartX=-24.9782 StartY=43.164 StartZ=0 EndX=-29.755 EndY=38.3872 EndZ=0
    g9: LineSegment StartX=-29.755 StartY=38.3872 StartZ=0 EndX=-31.5747 EndY=36.5674 EndZ=0
    g10: LineSegment StartX=-31.5747 StartY=36.5674 StartZ=0 EndX=-33.8388 EndY=34.3033 EndZ=0
    g11: ArcOfCircle CenterX=-31.0355 CenterY=31.5 CenterZ=0 NormalX=0 NormalY=0 NormalZ=1 Radius=3.96447 StartAngle=2.35619 EndAngle=3.14159
    g12: LineSegment StartX=-35 StartY=31.5 StartZ=0 EndX=-35 EndY=30 EndZ=0
    g13: ArcOfCircle CenterX=-31 CenterY=30 CenterZ=0 NormalX=0 NormalY=0 NormalZ=1 Radius=4 StartAngle=3.14159 EndAngle=3.43027
    g14: LineSegment StartX=-34.8345 StartY=28.8612 StartZ=0 EndX=-33.9452 EndY=28.9547 EndZ=0
    g15: LineSegment StartX=-33.9452 StartY=28.9547 StartZ=0 EndX=-32.3011 EndY=29.1275 EndZ=0
    g16: LineSegment StartX=-32.3011 StartY=29.1275 StartZ=0 EndX=-27.3284 EndY=29.6502 EndZ=0
    g17: LineSegment StartX=-27.3284 StartY=29.6502 StartZ=0 EndX=-25.6762 EndY=29.8238 EndZ=0
    g18: LineSegment StartX=-25.6762 StartY=29.8238 StartZ=0 EndX=-20.1421 EndY=35.3579 EndZ=0
    g19: LineSegment StartX=-20.1421 StartY=35.3579 StartZ=0 EndX=-19.7178 EndY=35.7822 EndZ=0
    g20: LineSegment StartX=-19.7178 StartY=35.7822 StartZ=0 EndX=-16.1822 EndY=39.3178 EndZ=0
    g21: LineSegment StartX=-16.1822 StartY=39.3178 StartZ=0 EndX=-6.68224 EndY=48.8178 EndZ=0
    g22: LineSegment StartX=-6.68224 StartY=48.8178 StartZ=0 EndX=-6 EndY=49.5 EndZ=0
    g23: LineSegment StartX=-6 StartY=49.5 StartZ=0 EndX=0 EndY=49.5 EndZ=0
    g24: LineSegment StartX=0 StartY=49.5 StartZ=0 EndX=6 EndY=49.5 EndZ=0
    g25: LineSegment StartX=6 StartY=49.5 StartZ=0 EndX=6.68224 EndY=48.8178 EndZ=0
    g26: LineSegment StartX=6.68224 StartY=48.8178 StartZ=0 EndX=16.1822 EndY=39.3178 EndZ=0
    g27: LineSegment StartX=16.1822 StartY=39.3178 StartZ=0 EndX=19.7178 EndY=35.7822 EndZ=0
    g28: LineSegment StartX=19.7178 StartY=35.7822 StartZ=0 EndX=20.1421 EndY=35.3579 EndZ=0
    g29: LineSegment StartX=20.1421 StartY=35.3579 StartZ=0 EndX=25.6762 EndY=29.8238 EndZ=0
    g30: LineSegment StartX=25.6762 StartY=29.8238 StartZ=0 EndX=27.3284 EndY=29.6502 EndZ=0
    g31: LineSegment StartX=27.3284 StartY=29.6502 StartZ=0 EndX=32.3011 EndY=29.1275 EndZ=0
    g32: LineSegment StartX=32.3011 StartY=29.1275 StartZ=0 EndX=33.9452 EndY=28.9547 EndZ=0
    g33: LineSegment StartX=33.9452 StartY=28.9547 StartZ=0 EndX=34.8345 EndY=28.8612 EndZ=0
    g34: ArcOfCircle CenterX=31 CenterY=30 CenterZ=0 NormalX=0 NormalY=0 NormalZ=1 Radius=4 StartAngle=5.9945 EndAngle=6.28318
    g35: LineSegment StartX=35 StartY=30 StartZ=0 EndX=35 EndY=31.5 EndZ=0
    g36: ArcOfCircle CenterX=31.0355 CenterY=31.5 CenterZ=0 NormalX=0 NormalY=0 NormalZ=1 Radius=3.96447 StartAngle=2.02129e-07 EndAngle=0.785398
    g37: LineSegment StartX=33.8388 StartY=34.3033 StartZ=0 EndX=31.5747 EndY=36.5674 EndZ=0
    g38: LineSegment StartX=31.5747 StartY=36.5674 StartZ=0 EndX=29.755 EndY=38.3872 EndZ=0
    g39: LineSegment StartX=29.755 StartY=38.3872 StartZ=0 EndX=24.9782 EndY=43.164 EndZ=0
    g40: LineSegment StartX=24.9782 StartY=43.164 StartZ=0 EndX=23.564 EndY=44.5782 EndZ=0
    g41: LineSegment StartX=23.564 StartY=44.5782 StartZ=0 EndX=22.5674 EndY=45.5747 EndZ=0
    g42: LineSegment StartX=22.5674 StartY=45.5747 StartZ=0 EndX=20.8998 EndY=47.2423 EndZ=0
    g43: LineSegment StartX=20.8998 StartY=47.2423 StartZ=0 EndX=17.0711 EndY=51.0711 EndZ=0
    g44: ArcOfCircle CenterX=10 CenterY=44 CenterZ=0 NormalX=0 NormalY=0 NormalZ=1 Radius=10 StartAngle=0.785398 EndAngle=1.01262
    g45: ArcOfCircle CenterX=10 CenterY=44 CenterZ=0 NormalX=0 NormalY=0 NormalZ=1 Radius=10 StartAngle=1.01262 EndAngle=1.22466
    g46: ArcOfCircle CenterX=10 CenterY=44 CenterZ=0 NormalX=0 NormalY=0 NormalZ=1 Radius=10 StartAngle=1.22466 EndAngle=1.5708
    g47: LineSegment StartX=10 StartY=54 StartZ=0 EndX=0 EndY=54 EndZ=0
FEATURE [PartDesign::Pad] Pad040
  Length = 1
  Length2 = 100
  Placement = pos=(0,0,9) rot=(0,0,1;0rad)
  Sketch = -> Sketch251
  Type = 0
FEATURE [Sketcher::SketchObject] Sketch250
  Placement = pos=(0,0,16) rot=(0,0,1;0rad)
  Support = -> Pad040 [Face241]
  sketch-geometry (65):
    g0: LineSegment StartX=-27.6126 StartY=30.4404 StartZ=0 EndX=-27.3284 EndY=29.6502 EndZ=0
    g1: LineSegment StartX=-27.3284 StartY=29.6502 StartZ=0 EndX=-26.0356 EndY=29.7861 EndZ=0
    g2: LineSegment StartX=-26.0356 StartY=29.7861 StartZ=0 EndX=-26.1208 EndY=30.5972 EndZ=0
    g3: LineSegment StartX=-26.1208 StartY=30.5972 StartZ=0 EndX=-26.6434 EndY=35.5698 EndZ=0
    g4: LineSegment StartX=-26.6434 StartY=35.5698 StartZ=0 EndX=-27.0056 EndY=39.0153 EndZ=0
    g5: LineSegment StartX=-27.0056 StartY=39.0153 StartZ=0 EndX=-23.9175 EndY=42.1033 EndZ=0
    g6: LineSegment StartX=-23.9175 StartY=42.1033 StartZ=0 EndX=-23.5222 EndY=42.4986 EndZ=0
    g7: LineSegment StartX=-23.5222 StartY=42.4986 StartZ=0 EndX=-15.2247 EndY=40.2753 EndZ=0
    g8: LineSegment StartX=-15.2247 StartY=40.2753 StartZ=0 EndX=-14 EndY=41.5 EndZ=0
    g9: LineSegment StartX=-14 StartY=41.5 StartZ=0 EndX=-23.9705 EndY=44.1716 EndZ=0
    g10: LineSegment StartX=-23.9705 StartY=44.1716 StartZ=0 EndX=-24.9782 EndY=43.164 EndZ=0
    g11: LineSegment StartX=-24.9782 StartY=43.164 StartZ=0 EndX=-28.5721 EndY=39.57 EndZ=0
    g12: LineSegment StartX=-28.5721 StartY=39.57 StartZ=0 EndX=-28.1352 EndY=35.413 EndZ=0
    g13: LineSegment StartX=-28.1352 StartY=35.413 StartZ=0 EndX=-27.6126 EndY=30.4404 EndZ=0
    g14: LineSegment StartX=-32.1021 StartY=29.1484 StartZ=0 EndX=-32.3011 EndY=29.1275 EndZ=0
    g15: LineSegment StartX=-32.3011 StartY=29.1275 StartZ=0 EndX=-33.9452 EndY=28.9547 EndZ=0
    g16: LineSegment StartX=-33.9452 StartY=28.9547 StartZ=0 EndX=-34.8345 EndY=28.8612 EndZ=0
    g17: ArcOfCircle CenterX=-31 CenterY=30 CenterZ=0 NormalX=0 NormalY=0 NormalZ=1 Radius=4 StartAngle=3.14159 EndAngle=3.43027
    g18: LineSegment StartX=-35 StartY=30 StartZ=0 EndX=-35 EndY=31.5 EndZ=0
    g19: ArcOfCircle CenterX=-31.0355 CenterY=31.5 CenterZ=0 NormalX=0 NormalY=0 NormalZ=1 Radius=3.96447 StartAngle=2.35619 EndAngle=3.14159
    g20: LineSegment StartX=-33.8388 StartY=34.3033 StartZ=0 EndX=-32.7576 EndY=35.3846 EndZ=0
    g21: LineSegment StartX=-32.7576 StartY=35.3846 StartZ=0 EndX=-32.71 EndY=34.9322 EndZ=0
    g22: LineSegment StartX=-32.71 StartY=34.9322 StartZ=0 EndX=-32.1874 EndY=29.9596 EndZ=0
    g23: LineSegment StartX=-32.1874 StartY=29.9596 StartZ=0 EndX=-32.1021 EndY=29.1484 EndZ=0
    g24: ArcOfCircle CenterX=10 CenterY=44 CenterZ=0 NormalX=0 NormalY=0 NormalZ=1 Radius=10 StartAngle=1.11654 EndAngle=1.22466
    g25: LineSegment StartX=14.3879 StartY=52.9859 StartZ=0 EndX=11.8787 EndY=43.6213 EndZ=0
    g26: LineSegment StartX=11.8787 StartY=43.6213 StartZ=0 EndX=10.6539 EndY=44.8461 EndZ=0
    g27: LineSegment StartX=10.6539 StartY=44.8461 StartZ=0 EndX=12.596 EndY=52.0939 EndZ=0
    g28: ArcOfCircle CenterX=10 CenterY=44 CenterZ=0 NormalX=0 NormalY=0 NormalZ=1 Radius=8.5 StartAngle=1.26043 EndAngle=1.5708
    g29: LineSegment StartX=10 StartY=52.5 StartZ=0 EndX=0 EndY=52.5 EndZ=0
    g30: LineSegment StartX=0 StartY=52.5 StartZ=0 EndX=-10 EndY=52.5 EndZ=0
    g31: ArcOfCircle CenterX=-10 CenterY=44 CenterZ=0 NormalX=0 NormalY=0 NormalZ=1 Radius=8.5 StartAngle=1.5708 EndAngle=1.88116
    g32: LineSegment StartX=-12.596 StartY=52.0939 StartZ=0 EndX=-10.6539 EndY=44.8461 EndZ=0
    g33: LineSegment StartX=-10.6539 StartY=44.8461 StartZ=0 EndX=-11.8787 EndY=43.6213 EndZ=0
    g34: LineSegment StartX=-11.8787 StartY=43.6213 StartZ=0 EndX=-14.3879 EndY=52.9859 EndZ=0
    g35: ArcOfCircle CenterX=-10 CenterY=44 CenterZ=0 NormalX=0 NormalY=0 NormalZ=1 Radius=10 StartAngle=1.91693 EndAngle=2.02505
    g36: ArcOfCircle CenterX=-10 CenterY=44 CenterZ=0 NormalX=0 NormalY=0 NormalZ=1 Radius=10 StartAngle=1.5708 EndAngle=1.91693
    g37: LineSegment StartX=-10 StartY=54 StartZ=0 EndX=0 EndY=54 EndZ=0
    g38: LineSegment StartX=0 StartY=54 StartZ=0 EndX=10 EndY=54 EndZ=0
    g39: ArcOfCircle CenterX=10 CenterY=44 CenterZ=0 NormalX=0 NormalY=0 NormalZ=1 Radius=10 StartAngle=1.22466 EndAngle=1.5708
    g40: LineSegment StartX=32.71 StartY=34.9322 StartZ=0 EndX=32.1874 EndY=29.9596 EndZ=0
    g41: LineSegment StartX=32.1874 StartY=29.9596 StartZ=0 EndX=32.1021 EndY=29.1484 EndZ=0
    g42: LineSegment StartX=32.1021 StartY=29.1484 StartZ=0 EndX=32.3011 EndY=29.1275 EndZ=0
    g43: LineSegment StartX=32.3011 StartY=29.1275 StartZ=0 EndX=33.9452 EndY=28.9547 EndZ=0
    g44: LineSegment StartX=33.9452 StartY=28.9547 StartZ=0 EndX=34.8345 EndY=28.8612 EndZ=0
    g45: ArcOfCircle CenterX=31 CenterY=30 CenterZ=0 NormalX=0 NormalY=0 NormalZ=1 Radius=4 StartAngle=5.9945 EndAngle=6.28318
    g46: LineSegment StartX=35 StartY=30 StartZ=0 EndX=35 EndY=31.5 EndZ=0
    g47: ArcOfCircle CenterX=31.0355 CenterY=31.5 CenterZ=0 NormalX=0 NormalY=0 NormalZ=1 Radius=3.96447 StartAngle=2.02129e-07 EndAngle=0.785398
    g48: LineSegment StartX=33.8388 StartY=34.3033 StartZ=0 EndX=32.7576 EndY=35.3846 EndZ=0
    g49: LineSegment StartX=32.7576 StartY=35.3846 StartZ=0 EndX=32.71 EndY=34.9322 EndZ=0
    g50: LineSegment StartX=27.5273 StartY=29.6293 StartZ=0 EndX=27.3284 EndY=29.6502 EndZ=0
    g51: LineSegment StartX=27.3284 StartY=29.6502 StartZ=0 EndX=26.0356 EndY=29.7861 EndZ=0
    g52: LineSegment StartX=26.0356 StartY=29.7861 StartZ=0 EndX=26.1208 EndY=30.5972 EndZ=0
    g53: LineSegment StartX=26.1208 StartY=30.5972 StartZ=0 EndX=26.6434 EndY=35.5698 EndZ=0
    g54: LineSegment StartX=26.6434 StartY=35.5698 StartZ=0 EndX=27.0056 EndY=39.0153 EndZ=0
    g55: LineSegment StartX=27.0056 StartY=39.0153 StartZ=0 EndX=23.9175 EndY=42.1033 EndZ=0
    g56: LineSegment StartX=23.9175 StartY=42.1033 StartZ=0 EndX=23.5222 EndY=42.4986 EndZ=0
    g57: LineSegment StartX=23.5222 StartY=42.4986 StartZ=0 EndX=15.2247 EndY=40.2753 EndZ=0
    g58: LineSegment StartX=15.2247 StartY=40.2753 StartZ=0 EndX=14 EndY=41.5 EndZ=0
    g59: LineSegment StartX=14 StartY=41.5 StartZ=0 EndX=23.9705 EndY=44.1716 EndZ=0
    g60: LineSegment StartX=23.9705 StartY=44.1716 StartZ=0 EndX=24.9782 EndY=43.164 EndZ=0
    g61: LineSegment StartX=24.9782 StartY=43.164 StartZ=0 EndX=28.5721 EndY=39.57 EndZ=0
    g62: LineSegment StartX=28.5721 StartY=39.57 StartZ=0 EndX=28.1352 EndY=35.413 EndZ=0
    g63: LineSegment StartX=28.1352 StartY=35.413 StartZ=0 EndX=27.6126 EndY=30.4404 EndZ=0
    g64: LineSegment StartX=27.6126 StartY=30.4404 StartZ=0 EndX=27.5273 EndY=29.6293 EndZ=0
  constraints (14):
    c: Coincident(g0,g1)
    c: Coincident(g1,g2)
    c: Coincident(g2,g3)
    c: Coincident(g3,g4)
    c: Coincident(g4,g5)
    c: Coincident(g5,g6)
    c: Coincident(g6,g7)
    c: Coincident(g7,g8)
    c: Coincident(g8,g9)
    c: Coincident(g9,g10)
    c: Coincident(g10,g11)
    c: Coincident(g11,g12)
    c: Coincident(g12,g13)
    c: Coincident(g13,g0)
FEATURE [PartDesign::Pad] Pad041
  Length = 4
  Length2 = 100
  Placement = pos=(0,0,9) rot=(0,0,1;0rad)
  Sketch = -> Sketch250
  Type = 0
FEATURE [App::DocumentObjectGroup] Groupe054  label="Caches"
  Group = -> [Pad,Pad039,Pad040,Pad041]
FEATURE [Sketcher::SketchObject] Sketch264
  sketch-geometry (70):
    g0: ArcOfCircle CenterX=-11.5 CenterY=13.5 CenterZ=0 NormalX=0 NormalY=0 NormalZ=1 Radius=0.75 StartAngle=3.332e-08 EndAngle=2.0944
    g1: ArcOfCircle CenterX=-11.5 CenterY=13.5 CenterZ=0 NormalX=0 NormalY=0 NormalZ=1 Radius=0.75 StartAngle=2.09439 EndAngle=2.41186
    g2: LineSegment StartX=-12.059 StartY=14 StartZ=0 EndX=-13.941 EndY=14 EndZ=0
    g3: ArcOfCircle CenterX=-14.5 CenterY=13.5 CenterZ=0 NormalX=0 NormalY=0 NormalZ=1 Radius=0.75 StartAngle=0.729728 EndAngle=2.0944
    g4: ArcOfCircle CenterX=-14.5 CenterY=13.5 CenterZ=0 NormalX=0 NormalY=0 NormalZ=1 Radius=0.75 StartAngle=2.0944 EndAngle=3.14159
    g5: LineSegment StartX=-15.25 StartY=13.5 StartZ=0 EndX=-15.25 EndY=13 EndZ=0
    g6: ArcOfCircle CenterX=-14.5 CenterY=13 CenterZ=0 NormalX=0 NormalY=0 NormalZ=1 Radius=0.75 StartAngle=3.14159 EndAngle=4.18879
    g7: ArcOfCircle CenterX=-14.5 CenterY=13 CenterZ=0 NormalX=0 NormalY=0 NormalZ=1 Radius=0.75 StartAngle=4.18879 EndAngle=5.55346
    g8: LineSegment StartX=-13.941 StartY=12.5 StartZ=0 EndX=-12.059 EndY=12.5 EndZ=0
    g9: ArcOfCircle CenterX=-11.5 CenterY=13 CenterZ=0 NormalX=0 NormalY=0 NormalZ=1 Radius=0.75 StartAngle=3.87132 EndAngle=4.18879
    g10: ArcOfCircle CenterX=-11.5 CenterY=13 CenterZ=0 NormalX=0 NormalY=0 NormalZ=1 Radius=0.75 StartAngle=4.18879 EndAngle=6.28319
    g11: LineSegment StartX=-10.75 StartY=13 StartZ=0 EndX=-10.75 EndY=13.5 EndZ=0
    g12: ArcOfCircle CenterX=11.5 CenterY=13.5 CenterZ=0 NormalX=0 NormalY=0 NormalZ=1 Radius=0.75 StartAngle=1.0472 EndAngle=3.14159
    g13: ArcOfCircle CenterX=11.5 CenterY=13.5 CenterZ=0 NormalX=0 NormalY=0 NormalZ=1 Radius=0.75 StartAngle=0.729728 EndAngle=1.0472
    g14: LineSegment StartX=12.059 StartY=14 StartZ=0 EndX=13.941 EndY=14 EndZ=0
    g15: ArcOfCircle CenterX=14.5 CenterY=13.5 CenterZ=0 NormalX=0 NormalY=0 NormalZ=1 Radius=0.75 StartAngle=1.0472 EndAngle=2.41186
    g16: ArcOfCircle CenterX=14.5 CenterY=13.5 CenterZ=0 NormalX=0 NormalY=0 NormalZ=1 Radius=0.75 StartAngle=3.332e-08 EndAngle=1.0472
    g17: LineSegment StartX=15.25 StartY=13.5 StartZ=0 EndX=15.25 EndY=13 EndZ=0
    g18: ArcOfCircle CenterX=14.5 CenterY=13 CenterZ=0 NormalX=0 NormalY=0 NormalZ=1 Radius=0.75 StartAngle=5.23599 EndAngle=6.28319
    g19: ArcOfCircle CenterX=14.5 CenterY=13 CenterZ=0 NormalX=0 NormalY=0 NormalZ=1 Radius=0.75 StartAngle=3.87132 EndAngle=5.23599
    g20: LineSegment StartX=13.941 StartY=12.5 StartZ=0 EndX=12.059 EndY=12.5 EndZ=0
    g21: ArcOfCircle CenterX=11.5 CenterY=13 CenterZ=0 NormalX=0 NormalY=0 NormalZ=1 Radius=0.75 StartAngle=5.23599 EndAngle=5.55346
    g22: ArcOfCircle CenterX=11.5 CenterY=13 CenterZ=0 NormalX=0 NormalY=0 NormalZ=1 Radius=0.75 StartAngle=3.14159 EndAngle=5.23599
    g23: LineSegment StartX=10.75 StartY=13 StartZ=0 EndX=10.75 EndY=13.5 EndZ=0
    g24: ArcOfCircle CenterX=2.32505e-07 CenterY=8.5 CenterZ=0 NormalX=0 NormalY=0 NormalZ=1 Radius=6.5 StartAngle=4.18879 EndAngle=4.71239
    g25: ArcOfCircle CenterX=-7.1937e-08 CenterY=8.5 CenterZ=0 NormalX=0 NormalY=0 NormalZ=1 Radius=6.5 StartAngle=2.0944 EndAngle=4.18879
    g26: ArcOfCircle CenterX=2.32505e-07 CenterY=8.5 CenterZ=0 NormalX=0 NormalY=0 NormalZ=1 Radius=6.5 StartAngle=1.5708 EndAngle=2.0944
    g27: ArcOfCircle CenterX=-2.32505e-07 CenterY=8.5 CenterZ=0 NormalX=0 NormalY=0 NormalZ=1 Radius=6.5 StartAngle=1.0472 EndAngle=1.5708
    g28: ArcOfCircle CenterX=7.1937e-08 CenterY=8.5 CenterZ=0 NormalX=0 NormalY=0 NormalZ=1 Radius=6.5 StartAngle=5.23599 EndAngle=7.33038
    g29: ArcOfCircle CenterX=-2.32505e-07 CenterY=8.5 CenterZ=0 NormalX=0 NormalY=0 NormalZ=1 Radius=6.5 StartAngle=4.71239 EndAngle=5.23599
    g30: ArcOfCircle CenterX=9.4 CenterY=7.5 CenterZ=0 NormalX=0 NormalY=0 NormalZ=1 Radius=1.8 StartAngle=2.1058 EndAngle=2.64906
    g31: ArcOfCircle CenterX=9.4 CenterY=7.5 CenterZ=0 NormalX=0 NormalY=0 NormalZ=1 Radius=1.8 StartAngle=0.861724 EndAngle=2.1058
    g32: LineSegment StartX=10.572 StartY=8.86614 StartZ=0 EndX=11.2872 EndY=8.25258 EndZ=0
    g33: ArcOfCircle CenterX=12.915 CenterY=10.15 CenterZ=0 NormalX=0 NormalY=0 NormalZ=1 Radius=2.5 StartAngle=4.00332 EndAngle=5.88142
    g34: LineSegment StartX=15.216 StartY=9.17239 StartZ=0 EndX=16.3806 EndY=11.9134 EndZ=0
    g35: ArcOfCircle CenterX=15 CenterY=12.5 CenterZ=0 NormalX=0 NormalY=0 NormalZ=1 Radius=1.5 StartAngle=5.88142 EndAngle=6.28318
    g36: LineSegment StartX=16.5 StartY=12.5 StartZ=0 EndX=16.5 EndY=14 EndZ=0
    g37: ArcOfCircle CenterX=15 CenterY=14 CenterZ=0 NormalX=0 NormalY=0 NormalZ=1 Radius=1.5 StartAngle=0 EndAngle=1.5708
    g38: LineSegment StartX=15 StartY=15.5 StartZ=0 EndX=11 EndY=15.5 EndZ=0
    g39: ArcOfCircle CenterX=11 CenterY=14 CenterZ=0 NormalX=0 NormalY=0 NormalZ=1 Radius=1.5 StartAngle=1.5708 EndAngle=1.99057
    g40: LineSegment StartX=10.3887 StartY=15.3698 StartZ=0 EndX=7.61134 EndY=14.1302 EndZ=0
    g41: ArcOfCircle CenterX=7 CenterY=15.5 CenterZ=0 NormalX=0 NormalY=0 NormalZ=1 Radius=1.5 StartAngle=4.71239 EndAngle=5.13217
    g42: LineSegment StartX=7 StartY=14 StartZ=0 EndX=6.73074 EndY=14 EndZ=0
    g43: ArcOfCircle CenterX=6.77944 CenterY=14.6579 CenterZ=0 NormalX=0 NormalY=0 NormalZ=1 Radius=0.659716 StartAngle=3.93391 EndAngle=4.6385
    g44: ArcOfCircle CenterX=1.11659e-06 CenterY=8.5 CenterZ=0 NormalX=0 NormalY=0 NormalZ=1 Radius=8.5 StartAngle=0.733133 EndAngle=1.0472
    g45: ArcOfCircle CenterX=1.26577e-07 CenterY=8.5 CenterZ=0 NormalX=0 NormalY=0 NormalZ=1 Radius=8.5 StartAngle=1.0472 EndAngle=1.5708
    g46: ArcOfCircle CenterX=-1.26577e-07 CenterY=8.5 CenterZ=0 NormalX=0 NormalY=0 NormalZ=1 Radius=8.5 StartAngle=1.5708 EndAngle=2.0944
    g47: ArcOfCircle CenterX=-1.11659e-06 CenterY=8.5 CenterZ=0 NormalX=0 NormalY=0 NormalZ=1 Radius=8.5 StartAngle=2.0944 EndAngle=2.40846
    g48: ArcOfCircle CenterX=-6.77944 CenterY=14.6579 CenterZ=0 NormalX=0 NormalY=0 NormalZ=1 Radius=0.659716 StartAngle=4.78628 EndAngle=5.49087
    g49: LineSegment StartX=-6.73074 StartY=14 StartZ=0 EndX=-7 EndY=14 EndZ=0
    g50: ArcOfCircle CenterX=-7 CenterY=15.5 CenterZ=0 NormalX=0 NormalY=0 NormalZ=1 Radius=1.5 StartAngle=4.29261 EndAngle=4.71239
    g51: LineSegment StartX=-7.61134 StartY=14.1302 StartZ=0 EndX=-10.3887 EndY=15.3698 EndZ=0
    g52: ArcOfCircle CenterX=-11 CenterY=14 CenterZ=0 NormalX=0 NormalY=0 NormalZ=1 Radius=1.5 StartAngle=1.15102 EndAngle=1.5708
    g53: LineSegment StartX=-11 StartY=15.5 StartZ=0 EndX=-15 EndY=15.5 EndZ=0
    g54: ArcOfCircle CenterX=-15 CenterY=14 CenterZ=0 NormalX=0 NormalY=0 NormalZ=1 Radius=1.5 StartAngle=1.5708 EndAngle=3.14159
    g55: LineSegment StartX=-16.5 StartY=14 StartZ=0 EndX=-16.5 EndY=12.5 EndZ=0
    g56: ArcOfCircle CenterX=-15 CenterY=12.5 CenterZ=0 NormalX=0 NormalY=0 NormalZ=1 Radius=1.5 StartAngle=3.14159 EndAngle=3.54336
    g57: LineSegment StartX=-16.3806 StartY=11.9134 StartZ=0 EndX=-15.216 EndY=9.17239 EndZ=0
    g58: ArcOfCircle CenterX=-12.915 CenterY=10.15 CenterZ=0 NormalX=0 NormalY=0 NormalZ=1 Radius=2.5 StartAngle=3.54336 EndAngle=5.42146
    g59: LineSegment StartX=-11.2872 StartY=8.25258 StartZ=0 EndX=-10.572 EndY=8.86614 EndZ=0
    g60: ArcOfCircle CenterX=-9.4 CenterY=7.5 CenterZ=0 NormalX=0 NormalY=0 NormalZ=1 Radius=1.8 StartAngle=1.0358 EndAngle=2.27987
    g61: ArcOfCircle CenterX=-9.4 CenterY=7.5 CenterZ=0 NormalX=0 NormalY=0 NormalZ=1 Radius=1.8 StartAngle=0.49253 EndAngle=1.0358
    g62: LineSegment StartX=-7.81395 StartY=8.35114 StartZ=0 EndX=-7.15588 EndY=6.25426 EndZ=0
    g63: ArcOfCircle CenterX=8.8031e-07 CenterY=8.5 CenterZ=0 NormalX=0 NormalY=0 NormalZ=1 Radius=7.5 StartAngle=3.44569 EndAngle=4.18879
    g64: ArcOfCircle CenterX=-8.80049e-07 CenterY=8.5 CenterZ=0 NormalX=0 NormalY=0 NormalZ=1 Radius=7.5 StartAngle=4.18879 EndAngle=4.71239
    g65: ArcOfCircle CenterX=8.80049e-07 CenterY=8.5 CenterZ=0 NormalX=0 NormalY=0 NormalZ=1 Radius=7.5 StartAngle=4.71239 EndAngle=5.23599
    g66: ArcOfCircle CenterX=-9.7099e-08 CenterY=8.5 CenterZ=0 NormalX=0 NormalY=0 NormalZ=1 Radius=7.5 StartAngle=5.23599 EndAngle=5.97909
    g67: LineSegment StartX=7.15588 StartY=6.25426 StartZ=0 EndX=7.81395 EndY=8.35114 EndZ=0
    g68: Circle CenterX=-12.915 CenterY=10.15 CenterZ=0 NormalX=0 NormalY=0 NormalZ=1 Radius=1
    g69: Circle CenterX=12.915 CenterY=10.15 CenterZ=0 NormalX=0 NormalY=0 NormalZ=1 Radius=1
FEATURE [PartDesign::Pad] Pad029
  Length = 1.5
  Length2 = 100
  Sketch = -> Sketch264
  Type = 0
FEATURE [App::DocumentObjectGroup] entretoises_externes
  Group = -> [Pad029]
FEATURE [Part::FeaturePython] Clone130  label="Clone of Pad030"  # Draft clone (typed FeaturePython)
  Objects = -> [Pad029]
  Placement = pos=(21,0,0) rot=(0.57735,0.57735,0.57735;2.0944rad)
  Scale = (1,1,1)
FEATURE [Part::FeaturePython] Clone131  label="Clone of Pad031"  # Draft clone (typed FeaturePython)
  Objects = -> [Pad029]
  Placement = pos=(-22.5,0,0) rot=(0.57735,0.57735,0.57735;2.0944rad)
  Scale = (1,1,1)
FEATURE [App::DocumentObjectGroup] Groupe055  label="Wurth"
  Group = -> [Fusion004,Fusion005,Clone094,Clone095,Clone096,Clone097]
FEATURE [App::DocumentObjectGroup] Groupe044  label="Connecteurs"
  Group = -> [Groupe055,Groupe046]
FEATURE [Sketcher::SketchObject] Sketch
  Placement = pos=(0,0,20) rot=(0,0,1;0rad)
  sketch-geometry (143):
    g0: LineSegment StartX=-5.29289 StartY=48.7929 StartZ=0 EndX=-9.53553 EndY=45.9645 EndZ=0
    g1: LineSegment StartX=-9.53553 StartY=45.9645 StartZ=0 EndX=-8.82843 EndY=45.2574 EndZ=0
    g2: LineSegment StartX=-8.82843 StartY=45.2574 StartZ=0 EndX=-5.29289 EndY=48.7929 EndZ=0
    g3: LineSegment StartX=32.4534 StartY=29.1115 StartZ=0 EndX=32.3489 EndY=28.117 EndZ=0
    g4: LineSegment StartX=32.3489 StartY=28.117 StartZ=0 EndX=24.3927 EndY=28.9532 EndZ=0
    g5: LineSegment StartX=24.3927 StartY=28.9532 StartZ=0 EndX=24.4973 EndY=29.9477 EndZ=0
    g6: LineSegment StartX=24.4973 StartY=29.9477 StartZ=0 EndX=32.4534 EndY=29.1115 EndZ=0
    g7: LineSegment StartX=-32.4534 StartY=29.1115 StartZ=0 EndX=-32.3489 EndY=28.117 EndZ=0
    g8: LineSegment StartX=-32.3489 StartY=28.117 StartZ=0 EndX=-24.3927 EndY=28.9532 EndZ=0
    g9: LineSegment StartX=-24.3927 StartY=28.9532 StartZ=0 EndX=-24.4973 EndY=29.9477 EndZ=0
    g10: LineSegment StartX=-24.4973 StartY=29.9477 StartZ=0 EndX=-32.4534 EndY=29.1115 EndZ=0
    g11: LineSegment StartX=-19.435 StartY=34.6508 StartZ=0 EndX=-13.7782 EndY=40.3076 EndZ=0
    g12: LineSegment StartX=-13.7782 StartY=40.3076 StartZ=0 EndX=-14.4853 EndY=41.0147 EndZ=0
    g13: LineSegment StartX=-14.4853 StartY=41.0147 StartZ=0 EndX=-20.1421 EndY=35.3579 EndZ=0
    g14: LineSegment StartX=-20.1421 StartY=35.3579 StartZ=0 EndX=-19.435 EndY=34.6508 EndZ=0
    g15: LineSegment StartX=19.435 StartY=34.6508 StartZ=0 EndX=13.7782 EndY=40.3076 EndZ=0
    g16: LineSegment StartX=13.7782 StartY=40.3076 StartZ=0 EndX=14.4853 EndY=41.0147 EndZ=0
    g17: LineSegment StartX=14.4853 StartY=41.0147 StartZ=0 EndX=20.1421 EndY=35.3579 EndZ=0
    g18: LineSegment StartX=20.1421 StartY=35.3579 StartZ=0 EndX=19.435 EndY=34.6508 EndZ=0
    g19: LineSegment StartX=5.29289 StartY=48.7929 StartZ=0 EndX=6 EndY=49.5 EndZ=0
    g20: LineSegment StartX=6 StartY=49.5 StartZ=0 EndX=9.53553 EndY=45.9645 EndZ=0
    g21: LineSegment StartX=9.53553 StartY=45.9645 StartZ=0 EndX=8.82843 EndY=45.2574 EndZ=0
    g22: LineSegment StartX=8.82843 StartY=45.2574 StartZ=0 EndX=5.29289 EndY=48.7929 EndZ=0
    g23: ArcOfCircle CenterX=-31.0355 CenterY=31.5 CenterZ=0 NormalX=0 NormalY=0 NormalZ=1 Radius=3.96447 StartAngle=2.35619 EndAngle=3.14159
    g24: LineSegment StartX=-35 StartY=31.5 StartZ=0 EndX=-35 EndY=30 EndZ=0
    g25: ArcOfCircle CenterX=-31 CenterY=30 CenterZ=0 NormalX=0 NormalY=0 NormalZ=1 Radius=4 StartAngle=3.14159 EndAngle=3.92699
    g26: LineSegment StartX=-33.8284 StartY=27.1716 StartZ=0 EndX=-32.2426 EndY=25.5858 EndZ=0
    g27: ArcOfCircle CenterX=-26 CenterY=31.8284 CenterZ=0 NormalX=0 NormalY=0 NormalZ=1 Radius=8.82842 StartAngle=3.92699 EndAngle=4.71239
    g28: ArcOfCircle CenterX=-26 CenterY=20 CenterZ=0 NormalX=0 NormalY=0 NormalZ=1 Radius=3 StartAngle=2.9802e-08 EndAngle=1.5708
    g29: LineSegment StartX=-23 StartY=20 StartZ=0 EndX=-23 EndY=-20 EndZ=0
    g30: ArcOfCircle CenterX=-27 CenterY=-20 CenterZ=0 NormalX=0 NormalY=0 NormalZ=1 Radius=4 StartAngle=5.04269 EndAngle=6.28319
    g31: ArcOfCircle CenterX=-24.6 CenterY=-27 CenterZ=0 NormalX=0 NormalY=0 NormalZ=1 Radius=3.4 StartAngle=1.90109 EndAngle=3.14159
    g32: LineSegment StartX=-28 StartY=-27 StartZ=0 EndX=-28 EndY=-28 EndZ=0
    g33: ArcOfCircle CenterX=-20 CenterY=-28 CenterZ=0 NormalX=0 NormalY=0 NormalZ=1 Radius=8 StartAngle=3.14159 EndAngle=4.24064
    g34: LineSegment StartX=-23.6355 StartY=-35.1262 StartZ=0 EndX=-9.27219 EndY=-42.4539 EndZ=0
    g35: ArcOfCircle CenterX=-6.99997 CenterY=-38 CenterZ=0 NormalX=0 NormalY=0 NormalZ=1 Radius=5 StartAngle=4.24064 EndAngle=4.71239
    g36: LineSegment StartX=-6.99997 StartY=-43 StartZ=0 EndX=0 EndY=-43 EndZ=0
    g37: LineSegment StartX=0 StartY=-43 StartZ=0 EndX=7 EndY=-43 EndZ=0
    g38: ArcOfCircle CenterX=7 CenterY=-38 CenterZ=0 NormalX=0 NormalY=0 NormalZ=1 Radius=5 StartAngle=4.71239 EndAngle=5.18413
    g39: LineSegment StartX=9.2722 StartY=-42.4539 StartZ=0 EndX=23.6355 EndY=-35.1262 EndZ=0
    g40: ArcOfCircle CenterX=20 CenterY=-28 CenterZ=0 NormalX=0 NormalY=0 NormalZ=1 Radius=8 StartAngle=5.18414 EndAngle=6.28319
    g41: LineSegment StartX=28 StartY=-28 StartZ=0 EndX=28 EndY=-27 EndZ=0
    g42: ArcOfCircle CenterX=24.6 CenterY=-27 CenterZ=0 NormalX=0 NormalY=0 NormalZ=1 Radius=3.4 StartAngle=6.28319 EndAngle=7.52368
    g43: ArcOfCircle CenterX=27 CenterY=-20 CenterZ=0 NormalX=0 NormalY=0 NormalZ=1 Radius=4 StartAngle=3.14159 EndAngle=4.38209
    g44: LineSegment StartX=23 StartY=-20 StartZ=0 EndX=23 EndY=20 EndZ=0
    g45: ArcOfCircle CenterX=26 CenterY=20 CenterZ=0 NormalX=0 NormalY=0 NormalZ=1 Radius=3 StartAngle=1.5708 EndAngle=3.14159
    g46: ArcOfCircle CenterX=26 CenterY=31.8284 CenterZ=0 NormalX=0 NormalY=0 NormalZ=1 Radius=8.82842 StartAngle=4.71239 EndAngle=5.49779
    g47: LineSegment StartX=32.2426 StartY=25.5858 StartZ=0 EndX=33.8284 EndY=27.1716 EndZ=0
    g48: ArcOfCircle CenterX=31 CenterY=30 CenterZ=0 NormalX=0 NormalY=0 NormalZ=1 Radius=4 StartAngle=5.49779 EndAngle=6.28319
    g49: LineSegment StartX=35 StartY=30 StartZ=0 EndX=35 EndY=31.5 EndZ=0
    g50: ArcOfCircle CenterX=31.0355 CenterY=31.5 CenterZ=0 NormalX=0 NormalY=0 NormalZ=1 Radius=3.96447 StartAngle=3.9425e-08 EndAngle=0.785398
    g51: LineSegment StartX=33.8388 StartY=34.3033 StartZ=0 EndX=17.0711 EndY=51.0711 EndZ=0
    g52: ArcOfCircle CenterX=10 CenterY=44 CenterZ=0 NormalX=0 NormalY=0 NormalZ=1 Radius=10 StartAngle=0.785398 EndAngle=1.5708
    g53: LineSegment StartX=10 StartY=54 StartZ=0 EndX=0 EndY=54 EndZ=0
    g54: LineSegment StartX=0 StartY=54 StartZ=0 EndX=-10 EndY=54 EndZ=0
    g55: ArcOfCircle CenterX=-10 CenterY=44 CenterZ=0 NormalX=0 NormalY=0 NormalZ=1 Radius=10 StartAngle=1.5708 EndAngle=2.35619
    g56: LineSegment StartX=-17.0711 StartY=51.0711 StartZ=0 EndX=-33.8388 EndY=34.3033 EndZ=0
    g57: ArcOfCircle CenterX=-19.855 CenterY=30.645 CenterZ=0 NormalX=0 NormalY=0 NormalZ=1 Radius=0.502046 StartAngle=5.49779 EndAngle=8.63938
    g58: LineSegment StartX=-20.21 StartY=31 StartZ=0 EndX=-20.29 EndY=31 EndZ=0
    g59: ArcOfCircle CenterX=-20.645 CenterY=30.645 CenterZ=0 NormalX=0 NormalY=0 NormalZ=1 Radius=0.502046 StartAngle=0.785398 EndAngle=3.92699
    g60: LineSegment StartX=-21 StartY=30.29 StartZ=0 EndX=-21 EndY=28.71 EndZ=0
    g61: ArcOfCircle CenterX=-20.645 CenterY=28.355 CenterZ=0 NormalX=0 NormalY=0 NormalZ=1 Radius=0.502046 StartAngle=2.35619 EndAngle=5.49779
    g62: LineSegment StartX=-20.29 StartY=28 StartZ=0 EndX=-20.21 EndY=28 EndZ=0
    g63: ArcOfCircle CenterX=-19.855 CenterY=28.355 CenterZ=0 NormalX=0 NormalY=0 NormalZ=1 Radius=0.502046 StartAngle=3.92699 EndAngle=7.06858
    g64: LineSegment StartX=-19.5 StartY=28.71 StartZ=0 EndX=-19.5 EndY=30.29 EndZ=0
    g65: ArcOfCircle CenterX=-19.855 CenterY=1.145 CenterZ=0 NormalX=0 NormalY=0 NormalZ=1 Radius=0.502046 StartAngle=5.49779 EndAngle=8.63938
    g66: LineSegment StartX=-20.21 StartY=1.5 StartZ=0 EndX=-20.29 EndY=1.5 EndZ=0
    g67: ArcOfCircle CenterX=-20.645 CenterY=1.145 CenterZ=0 NormalX=0 NormalY=0 NormalZ=1 Radius=0.502046 StartAngle=0.785398 EndAngle=3.92699
    g68: LineSegment StartX=-21 StartY=0.79 StartZ=0 EndX=-21 EndY=-0.79 EndZ=0
    g69: ArcOfCircle CenterX=-20.645 CenterY=-1.145 CenterZ=0 NormalX=0 NormalY=0 NormalZ=1 Radius=0.502046 StartAngle=2.35619 EndAngle=5.49779
    g70: LineSegment StartX=-20.29 StartY=-1.5 StartZ=0 EndX=-20.21 EndY=-1.5 EndZ=0
    g71: ArcOfCircle CenterX=-19.855 CenterY=-1.145 CenterZ=0 NormalX=0 NormalY=0 NormalZ=1 Radius=0.502046 StartAngle=3.92699 EndAngle=7.06858
    g72: LineSegment StartX=-19.5 StartY=-0.79 StartZ=0 EndX=-19.5 EndY=0.79 EndZ=0
    g73: ArcOfCircle CenterX=-19.855 CenterY=-30.855 CenterZ=0 NormalX=0 NormalY=0 NormalZ=1 Radius=0.502046 StartAngle=5.49779 EndAngle=8.63938
    g74: LineSegment StartX=-20.21 StartY=-30.5 StartZ=0 EndX=-20.29 EndY=-30.5 EndZ=0
    g75: ArcOfCircle CenterX=-20.645 CenterY=-30.855 CenterZ=0 NormalX=0 NormalY=0 NormalZ=1 Radius=0.502046 StartAngle=0.785398 EndAngle=3.92699
    g76: LineSegment StartX=-21 StartY=-31.21 StartZ=0 EndX=-21 EndY=-32.79 EndZ=0
    g77: ArcOfCircle CenterX=-20.645 CenterY=-33.145 CenterZ=0 NormalX=0 NormalY=0 NormalZ=1 Radius=0.502046 StartAngle=2.35619 EndAngle=5.49779
    g78: LineSegment StartX=-20.29 StartY=-33.5 StartZ=0 EndX=-20.21 EndY=-33.5 EndZ=0
    g79: ArcOfCircle CenterX=-19.855 CenterY=-33.145 CenterZ=0 NormalX=0 NormalY=0 NormalZ=1 Radius=0.502046 StartAngle=3.92699 EndAngle=7.06858
    g80: LineSegment StartX=-19.5 StartY=-32.79 StartZ=0 EndX=-19.5 EndY=-31.21 EndZ=0
    g81: ArcOfCircle CenterX=19.855 CenterY=30.645 CenterZ=0 NormalX=0 NormalY=0 NormalZ=1 Radius=0.502046 StartAngle=0.785398 EndAngle=3.92699
    g82: LineSegment StartX=20.21 StartY=31 StartZ=0 EndX=20.29 EndY=31 EndZ=0
    g83: ArcOfCircle CenterX=20.645 CenterY=30.645 CenterZ=0 NormalX=0 NormalY=0 NormalZ=1 Radius=0.502046 StartAngle=5.49779 EndAngle=8.63938
    g84: LineSegment StartX=21 StartY=30.29 StartZ=0 EndX=21 EndY=28.71 EndZ=0
    g85: ArcOfCircle CenterX=20.645 CenterY=28.355 CenterZ=0 NormalX=0 NormalY=0 NormalZ=1 Radius=0.502046 StartAngle=3.92699 EndAngle=7.06858
    g86: LineSegment StartX=20.29 StartY=28 StartZ=0 EndX=20.21 EndY=28 EndZ=0
    g87: ArcOfCircle CenterX=19.855 CenterY=28.355 CenterZ=0 NormalX=0 NormalY=0 NormalZ=1 Radius=0.502046 StartAngle=2.35619 EndAngle=5.49779
    g88: LineSegment StartX=19.5 StartY=28.71 StartZ=0 EndX=19.5 EndY=30.29 EndZ=0
    g89: ArcOfCircle CenterX=19.855 CenterY=1.145 CenterZ=0 NormalX=0 NormalY=0 NormalZ=1 Radius=0.502046 StartAngle=0.785398 EndAngle=3.92699
    g90: LineSegment StartX=20.21 StartY=1.5 StartZ=0 EndX=20.29 EndY=1.5 EndZ=0
    g91: ArcOfCircle CenterX=20.645 CenterY=1.145 CenterZ=0 NormalX=0 NormalY=0 NormalZ=1 Radius=0.502046 StartAngle=5.49779 EndAngle=8.63938
    g92: LineSegment StartX=21 StartY=0.79 StartZ=0 EndX=21 EndY=-0.79 EndZ=0
    g93: ArcOfCircle CenterX=20.645 CenterY=-1.145 CenterZ=0 NormalX=0 NormalY=0 NormalZ=1 Radius=0.502046 StartAngle=3.92699 EndAngle=7.06858
    g94: LineSegment StartX=20.29 StartY=-1.5 StartZ=0 EndX=20.21 EndY=-1.5 EndZ=0
    g95: ArcOfCircle CenterX=19.855 CenterY=-1.145 CenterZ=0 NormalX=0 NormalY=0 NormalZ=1 Radius=0.502046 StartAngle=2.35619 EndAngle=5.49779
    g96: LineSegment StartX=19.5 StartY=-0.79 StartZ=0 EndX=19.5 EndY=0.79 EndZ=0
    g97: ArcOfCircle CenterX=19.855 CenterY=-30.855 CenterZ=0 NormalX=0 NormalY=0 NormalZ=1 Radius=0.502046 StartAngle=0.785398 EndAngle=3.92699
    g98: LineSegment StartX=20.21 StartY=-30.5 StartZ=0 EndX=20.29 EndY=-30.5 EndZ=0
    g99: ArcOfCircle CenterX=20.645 CenterY=-30.855 CenterZ=0 NormalX=0 NormalY=0 NormalZ=1 Radius=0.502046 StartAngle=5.49779 EndAngle=8.63938
    g100: LineSegment StartX=21 StartY=-31.21 StartZ=0 EndX=21 EndY=-32.79 EndZ=0
    g101: ArcOfCircle CenterX=20.645 CenterY=-33.145 CenterZ=0 NormalX=0 NormalY=0 NormalZ=1 Radius=0.502046 StartAngle=3.92699 EndAngle=7.06858
    g102: LineSegment StartX=20.29 StartY=-33.5 StartZ=0 EndX=20.21 EndY=-33.5 EndZ=0
    g103: ArcOfCircle CenterX=19.855 CenterY=-33.145 CenterZ=0 NormalX=0 NormalY=0 NormalZ=1 Radius=0.502046 StartAngle=2.35619 EndAngle=5.49779
    g104: LineSegment StartX=19.5 StartY=-32.79 StartZ=0 EndX=19.5 EndY=-31.21 EndZ=0
    g105: LineSegment StartX=-13.5 StartY=-34 StartZ=0 EndX=13.5 EndY=-34 EndZ=0
    g106: LineSegment StartX=13.5 StartY=-34 StartZ=0 EndX=13.5 EndY=-14 EndZ=0
    g107: LineSegment StartX=13.5 StartY=-14 StartZ=0 EndX=-13.5 EndY=-14 EndZ=0
    g108: LineSegment StartX=-13.5 StartY=-14 StartZ=0 EndX=-13.5 EndY=-34 EndZ=0
    g109: ArcOfCircle CenterX=-9 CenterY=8.5 CenterZ=0 NormalX=0 NormalY=0 NormalZ=1 Radius=1 StartAngle=0 EndAngle=1.5708
    g110: LineSegment StartX=-9 StartY=9.5 StartZ=0 EndX=-18 EndY=9.5 EndZ=0
    g111: ArcOfCircle CenterX=-18 CenterY=8.5 CenterZ=0 NormalX=0 NormalY=0 NormalZ=1 Radius=1 StartAngle=1.5708 EndAngle=3.14159
    g112: LineSegment StartX=-19 StartY=8.5 StartZ=0 EndX=-19 EndY=5.5 EndZ=0
    g113: ArcOfCircle CenterX=-18 CenterY=5.5 CenterZ=0 NormalX=0 NormalY=0 NormalZ=1 Radius=1 StartAngle=3.14159 EndAngle=4.71239
    g114: LineSegment StartX=-18 StartY=4.5 StartZ=0 EndX=-9 EndY=4.5 EndZ=0
    g115: ArcOfCircle CenterX=-9 CenterY=5.5 CenterZ=0 NormalX=0 NormalY=0 NormalZ=1 Radius=1 StartAngle=4.71239 EndAngle=6.28319
    g116: LineSegment StartX=-8 StartY=5.5 StartZ=0 EndX=-8 EndY=8.5 EndZ=0
    g117: ArcOfCircle CenterX=18 CenterY=5.5 CenterZ=0 NormalX=0 NormalY=0 NormalZ=1 Radius=1 StartAngle=4.71239 EndAngle=6.28319
    g118: LineSegment StartX=18 StartY=4.5 StartZ=0 EndX=9 EndY=4.5 EndZ=0
    g119: ArcOfCircle CenterX=9 CenterY=5.5 CenterZ=0 NormalX=0 NormalY=0 NormalZ=1 Radius=1 StartAngle=3.14159 EndAngle=4.71239
    g120: LineSegment StartX=8 StartY=5.5 StartZ=0 EndX=8 EndY=8.5 EndZ=0
    g121: ArcOfCircle CenterX=9 CenterY=8.5 CenterZ=0 NormalX=0 NormalY=0 NormalZ=1 Radius=1 StartAngle=1.5708 EndAngle=3.14159
    g122: LineSegment StartX=9 StartY=9.5 StartZ=0 EndX=18 EndY=9.5 EndZ=0
    g123: ArcOfCircle CenterX=18 CenterY=8.5 CenterZ=0 NormalX=0 NormalY=0 NormalZ=1 Radius=1 StartAngle=0 EndAngle=1.5708
    g124: LineSegment StartX=19 StartY=8.5 StartZ=0 EndX=19 EndY=5.5 EndZ=0
    g125: Circle CenterX=12.99 CenterY=13.55 CenterZ=0 NormalX=0 NormalY=0 NormalZ=1 Radius=0.4
    g126: Circle CenterX=14.01 CenterY=11.01 CenterZ=0 NormalX=0 NormalY=0 NormalZ=1 Radius=0.4
    g127: Circle CenterX=-11.5 CenterY=31.5 CenterZ=0 NormalX=0 NormalY=0 NormalZ=1 Radius=0.4
    g128: Circle CenterX=10.45 CenterY=13.55 CenterZ=0 NormalX=0 NormalY=0 NormalZ=1 Radius=0.4
    g129: Circle CenterX=11.47 CenterY=11.01 CenterZ=0 NormalX=0 NormalY=0 NormalZ=1 Radius=0.4
    g130: Circle CenterX=16.55 CenterY=11.01 CenterZ=0 NormalX=0 NormalY=0 NormalZ=1 Radius=0.4
    g131: Circle CenterX=15.53 CenterY=13.55 CenterZ=0 NormalX=0 NormalY=0 NormalZ=1 Radius=0.4
    g132: Circle CenterX=-10.45 CenterY=11.01 CenterZ=0 NormalX=0 NormalY=0 NormalZ=1 Radius=0.4
    g133: Circle CenterX=-15.53 CenterY=11.01 CenterZ=0 NormalX=0 NormalY=0 NormalZ=1 Radius=0.4
    g134: Circle CenterX=-16.55 CenterY=13.55 CenterZ=0 NormalX=0 NormalY=0 NormalZ=1 Radius=0.4
    g135: Circle CenterX=-12.99 CenterY=11.01 CenterZ=0 NormalX=0 NormalY=0 NormalZ=1 Radius=0.4
    g136: Circle CenterX=-11.47 CenterY=13.55 CenterZ=0 NormalX=0 NormalY=0 NormalZ=1 Radius=0.4
    g137: Circle CenterX=-14.01 CenterY=13.55 CenterZ=0 NormalX=0 NormalY=0 NormalZ=1 Radius=0.4
    g138: Circle CenterX=-16.54 CenterY=-35.5 CenterZ=0 NormalX=0 NormalY=0 NormalZ=1 Radius=0.4
    g139: Circle CenterX=-14 CenterY=-35.5 CenterZ=0 NormalX=0 NormalY=0 NormalZ=1 Radius=0.4
    g140: Circle CenterX=-11.46 CenterY=-35.5 CenterZ=0 NormalX=0 NormalY=0 NormalZ=1 Radius=0.4
    g141: Circle CenterX=-14.04 CenterY=31.5 CenterZ=0 NormalX=0 NormalY=0 NormalZ=1 Radius=0.4
    g142: Circle CenterX=-16.58 CenterY=31.5 CenterZ=0 NormalX=0 NormalY=0 NormalZ=1 Radius=0.4
  constraints (3):
    c: Coincident(g0,g1)
    c: Coincident(g1,g2)
    c: Coincident(g2,g0)
FEATURE [PartDesign::Pad] Pad037  label="PCB1mm"
  Length = 1
  Length2 = 100
  Placement = pos=(0,0,20) rot=(0,0,1;0rad)
  Sketch = -> Sketch
  Type = 0
FEATURE [App::DocumentObjectGroup] Groupe002  label="MainBoard"
  Group = -> [Groupe048,Pad037,Groupe038]
FEATURE [Sketcher::SketchObject] Sketch281
  sketch-geometry (239):
    g0: LineSegment StartX=-35 StartY=13.29 StartZ=0 EndX=-35 EndY=13.21 EndZ=0
    g1: ArcOfCircle CenterX=-34.645 CenterY=12.855 CenterZ=0 NormalX=0 NormalY=0 NormalZ=1 Radius=0.502046 StartAngle=2.35619 EndAngle=5.49779
    g2: LineSegment StartX=-34.29 StartY=12.5 StartZ=0 EndX=-32.21 EndY=12.5 EndZ=0
    g3: ArcOfCircle CenterX=-31.855 CenterY=12.855 CenterZ=0 NormalX=0 NormalY=0 NormalZ=1 Radius=0.502046 StartAngle=3.92699 EndAngle=7.06858
    g4: LineSegment StartX=-31.5 StartY=13.21 StartZ=0 EndX=-31.5 EndY=13.29 EndZ=0
    g5: ArcOfCircle CenterX=-31.855 CenterY=13.645 CenterZ=0 NormalX=0 NormalY=0 NormalZ=1 Radius=0.502046 StartAngle=5.49779 EndAngle=8.63938
    g6: LineSegment StartX=-32.21 StartY=14 StartZ=0 EndX=-34.29 EndY=14 EndZ=0
    g7: ArcOfCircle CenterX=-34.645 CenterY=13.645 CenterZ=0 NormalX=0 NormalY=0 NormalZ=1 Radius=0.502046 StartAngle=0.785398 EndAngle=3.92699
    g8: ArcOfCircle CenterX=29.355 CenterY=12.855 CenterZ=0 NormalX=0 NormalY=0 NormalZ=1 Radius=0.502046 StartAngle=2.35619 EndAngle=5.49779
    g9: LineSegment StartX=29.71 StartY=12.5 StartZ=0 EndX=31.79 EndY=12.5 EndZ=0
    g10: ArcOfCircle CenterX=32.145 CenterY=12.855 CenterZ=0 NormalX=0 NormalY=0 NormalZ=1 Radius=0.502046 StartAngle=3.92699 EndAngle=7.06858
    g11: LineSegment StartX=32.5 StartY=13.21 StartZ=0 EndX=32.5 EndY=13.29 EndZ=0
    g12: ArcOfCircle CenterX=32.145 CenterY=13.645 CenterZ=0 NormalX=0 NormalY=0 NormalZ=1 Radius=0.502046 StartAngle=5.49779 EndAngle=8.63938
    g13: LineSegment StartX=31.79 StartY=14 StartZ=0 EndX=29.71 EndY=14 EndZ=0
    g14: ArcOfCircle CenterX=29.355 CenterY=13.645 CenterZ=0 NormalX=0 NormalY=0 NormalZ=1 Radius=0.502046 StartAngle=0.785398 EndAngle=3.92699
    g15: LineSegment StartX=29 StartY=13.29 StartZ=0 EndX=29 EndY=13.21 EndZ=0
    g16: ArcOfCircle CenterX=0 CenterY=8.5 CenterZ=0 NormalX=0 NormalY=0 NormalZ=1 Radius=4.15 StartAngle=4.07813 EndAngle=5.34664
    g17: ArcOfCircle CenterX=2.96289 CenterY=4.47244 CenterZ=0 NormalX=0 NormalY=0 NormalZ=1 Radius=0.85 StartAngle=5.34733 EndAngle=8.48824
    g18: ArcOfCircle CenterX=0 CenterY=8.5 CenterZ=0 NormalX=0 NormalY=0 NormalZ=1 Radius=5.85 StartAngle=4.07803 EndAngle=5.34674
    g19: ArcOfCircle CenterX=-2.96289 CenterY=4.47244 CenterZ=0 NormalX=0 NormalY=0 NormalZ=1 Radius=0.85 StartAngle=0.936536 EndAngle=4.07745
    g20: ArcOfCircle CenterX=2.13675e-07 CenterY=8.5 CenterZ=0 NormalX=0 NormalY=0 NormalZ=1 Radius=4.15 StartAngle=6.17253 EndAngle=7.44104
    g21: ArcOfCircle CenterX=2.00653 CenterY=13.0797 CenterZ=0 NormalX=0 NormalY=0 NormalZ=1 Radius=0.85 StartAngle=1.15853 EndAngle=4.29945
    g22: ArcOfCircle CenterX=2.0114e-07 CenterY=8.5 CenterZ=0 NormalX=0 NormalY=0 NormalZ=1 Radius=5.85 StartAngle=6.17243 EndAngle=7.44114
    g23: ArcOfCircle CenterX=4.96942 CenterY=7.94784 CenterZ=0 NormalX=0 NormalY=0 NormalZ=1 Radius=0.85 StartAngle=3.03093 EndAngle=6.17185
    g24: ArcOfCircle CenterX=-2.13675e-07 CenterY=8.5 CenterZ=0 NormalX=0 NormalY=0 NormalZ=1 Radius=4.15 StartAngle=1.98374 EndAngle=3.25225
    g25: ArcOfCircle CenterX=-4.96942 CenterY=7.94784 CenterZ=0 NormalX=0 NormalY=0 NormalZ=1 Radius=0.85 StartAngle=3.25293 EndAngle=6.39385
    g26: ArcOfCircle CenterX=-2.0114e-07 CenterY=8.5 CenterZ=0 NormalX=0 NormalY=0 NormalZ=1 Radius=5.85 StartAngle=1.98364 EndAngle=3.25235
    g27: ArcOfCircle CenterX=-2.00653 CenterY=13.0797 CenterZ=0 NormalX=0 NormalY=0 NormalZ=1 Radius=0.85 StartAngle=5.12533 EndAngle=8.26624
    g28: ArcOfCircle CenterX=-0.999999 CenterY=18 CenterZ=0 NormalX=0 NormalY=0 NormalZ=1 Radius=1 StartAngle=1.5708 EndAngle=2.0944
    g29: ArcOfCircle CenterX=-1 CenterY=18 CenterZ=0 NormalX=0 NormalY=0 NormalZ=1 Radius=1 StartAngle=2.0944 EndAngle=4.18879
    g30: ArcOfCircle CenterX=-0.999999 CenterY=18 CenterZ=0 NormalX=0 NormalY=0 NormalZ=1 Radius=1 StartAngle=4.18879 EndAngle=4.71239
    g31: LineSegment StartX=-1 StartY=17 StartZ=0 EndX=1 EndY=17 EndZ=0
    g32: ArcOfCircle CenterX=1 CenterY=18 CenterZ=0 NormalX=0 NormalY=0 NormalZ=1 Radius=1 StartAngle=4.71239 EndAngle=6.28319
    g33: ArcOfCircle CenterX=1 CenterY=18 CenterZ=0 NormalX=0 NormalY=0 NormalZ=1 Radius=1 StartAngle=0 EndAngle=1.5708
    g34: LineSegment StartX=1 StartY=19 StartZ=0 EndX=-1 EndY=19 EndZ=0
    g35: LineSegment StartX=29.5 StartY=17.5 StartZ=0 EndX=29.5 EndY=16.5 EndZ=0
    g36: ArcOfCircle CenterX=30.75 CenterY=16.5 CenterZ=0 NormalX=0 NormalY=0 NormalZ=1 Radius=1.25 StartAngle=3.14159 EndAngle=4.71239
    g37: ArcOfCircle CenterX=30.75 CenterY=16.5 CenterZ=0 NormalX=0 NormalY=0 NormalZ=1 Radius=1.25 StartAngle=4.71239 EndAngle=6.28319
    g38: LineSegment StartX=32 StartY=16.5 StartZ=0 EndX=32 EndY=17.5 EndZ=0
    g39: ArcOfCircle CenterX=30.75 CenterY=17.5 CenterZ=0 NormalX=0 NormalY=0 NormalZ=1 Radius=1.25 StartAngle=6.28318 EndAngle=6.80678
    g40: ArcOfCircle CenterX=30.75 CenterY=17.5 CenterZ=0 NormalX=0 NormalY=0 NormalZ=1 Radius=1.25 StartAngle=0.523599 EndAngle=2.61799
    g41: ArcOfCircle CenterX=30.75 CenterY=17.5 CenterZ=0 NormalX=0 NormalY=0 NormalZ=1 Radius=1.25 StartAngle=2.61799 EndAngle=3.14159
    g42: LineSegment StartX=-19.1908 StartY=12.5 StartZ=0 EndX=-19.5 EndY=12.5 EndZ=0
    g43: LineSegment StartX=-19.5 StartY=12.5 StartZ=0 EndX=-27.5 EndY=12.5 EndZ=0
    g44: ArcOfCircle CenterX=-27.5 CenterY=8 CenterZ=0 NormalX=0 NormalY=0 NormalZ=1 Radius=4.5 StartAngle=1.5708 EndAngle=3.14159
    g45: LineSegment StartX=-32 StartY=8 StartZ=0 EndX=-32 EndY=7 EndZ=0
    g46: ArcOfCircle CenterX=-27.5 CenterY=7 CenterZ=0 NormalX=0 NormalY=0 NormalZ=1 Radius=4.5 StartAngle=3.14159 EndAngle=4.71239
    g47: LineSegment StartX=-27.5 StartY=2.5 StartZ=0 EndX=-25.5 EndY=2.5 EndZ=0
    g48: ArcOfCircle CenterX=-25.5 CenterY=5 CenterZ=0 NormalX=0 NormalY=0 NormalZ=1 Radius=2.5 StartAngle=4.71239 EndAngle=5.35589
    g49: LineSegment StartX=-24 StartY=3 StartZ=0 EndX=-16.5 EndY=10.5 EndZ=0
    g50: ArcOfCircle CenterX=-17.1106 CenterY=10.9281 CenterZ=0 NormalX=0 NormalY=0 NormalZ=1 Radius=0.745725 StartAngle=5.67176 EndAngle=6.89461
    g51: ArcOfCircle CenterX=-19.3454 CenterY=8.39955 CenterZ=0 NormalX=0 NormalY=0 NormalZ=1 Radius=4.10336 StartAngle=0.804564 EndAngle=1.53311
    g52: LineSegment StartX=-10.5801 StartY=8.85919 StartZ=0 EndX=-10.572 EndY=8.86614 EndZ=0
    g53: ArcOfCircle CenterX=-9.4 CenterY=7.5 CenterZ=0 NormalX=0 NormalY=0 NormalZ=1 Radius=1.8 StartAngle=1.0358 EndAngle=2.27987
    g54: ArcOfCircle CenterX=-9.4 CenterY=7.5 CenterZ=0 NormalX=0 NormalY=0 NormalZ=1 Radius=1.8 StartAngle=0.49253 EndAngle=1.0358
    g55: LineSegment StartX=-7.81395 StartY=8.35114 StartZ=0 EndX=-7.15588 EndY=6.25426 EndZ=0
    g56: ArcOfCircle CenterX=9.36416e-07 CenterY=8.5 CenterZ=0 NormalX=0 NormalY=0 NormalZ=1 Radius=7.5 StartAngle=3.44569 EndAngle=3.78509
    g57: ArcOfCircle CenterX=-6.96253 CenterY=3.55835 CenterZ=0 NormalX=0 NormalY=0 NormalZ=1 Radius=1.05902 StartAngle=4.74778 EndAngle=6.71336
    g58: ArcOfCircle CenterX=-6.96253 CenterY=3.55835 CenterZ=0 NormalX=0 NormalY=0 NormalZ=1 Radius=1.05901 StartAngle=4.677 EndAngle=4.74778
    g59: LineSegment StartX=-7 StartY=2.5 StartZ=0 EndX=-19 EndY=2.5 EndZ=0
    g60: LineSegment StartX=-19 StartY=2.5 StartZ=0 EndX=-19.0749 EndY=2.5 EndZ=0
    g61: ArcOfCircle CenterX=-19.0375 CenterY=3.55835 CenterZ=0 NormalX=0 NormalY=0 NormalZ=1 Radius=1.05902 StartAngle=2.71141 EndAngle=4.677
    g62: LineSegment StartX=-20 StartY=4 StartZ=0 EndX=-16 EndY=8 EndZ=0
    g63: ArcOfCircle CenterX=-15.0954 CenterY=6.49778 CenterZ=0 NormalX=0 NormalY=0 NormalZ=1 Radius=1.75357 StartAngle=1.02877 EndAngle=2.11282
    g64: ArcOfCircle CenterX=-12.915 CenterY=10.15 CenterZ=0 NormalX=0 NormalY=0 NormalZ=1 Radius=2.5 StartAngle=4.17686 EndAngle=5.42146
    g65: LineSegment StartX=-11.2872 StartY=8.25258 StartZ=0 EndX=-10.5801 EndY=8.85919 EndZ=0
    g66: LineSegment StartX=10.5801 StartY=8.85919 StartZ=0 EndX=10.572 EndY=8.86614 EndZ=0
    g67: ArcOfCircle CenterX=9.4 CenterY=7.5 CenterZ=0 NormalX=0 NormalY=0 NormalZ=1 Radius=1.8 StartAngle=0.861724 EndAngle=2.1058
    g68: ArcOfCircle CenterX=9.4 CenterY=7.5 CenterZ=0 NormalX=0 NormalY=0 NormalZ=1 Radius=1.8 StartAngle=2.1058 EndAngle=2.64906
    g69: LineSegment StartX=7.81395 StartY=8.35114 StartZ=0 EndX=7.15588 EndY=6.25426 EndZ=0
    g70: ArcOfCircle CenterX=-9.36416e-07 CenterY=8.5 CenterZ=0 NormalX=0 NormalY=0 NormalZ=1 Radius=7.5 StartAngle=5.63968 EndAngle=5.97909
    g71: ArcOfCircle CenterX=6.96253 CenterY=3.55835 CenterZ=0 NormalX=0 NormalY=0 NormalZ=1 Radius=1.05902 StartAngle=2.71141 EndAngle=4.677
    g72: ArcOfCircle CenterX=6.96253 CenterY=3.55835 CenterZ=0 NormalX=0 NormalY=0 NormalZ=1 Radius=1.05901 StartAngle=4.677 EndAngle=4.74778
    g73: LineSegment StartX=7 StartY=2.5 StartZ=0 EndX=19 EndY=2.5 EndZ=0
    g74: LineSegment StartX=19 StartY=2.5 StartZ=0 EndX=19.0749 EndY=2.5 EndZ=0
    g75: ArcOfCircle CenterX=19.0375 CenterY=3.55835 CenterZ=0 NormalX=0 NormalY=0 NormalZ=1 Radius=1.05902 StartAngle=4.74778 EndAngle=6.71336
    g76: LineSegment StartX=20 StartY=4 StartZ=0 EndX=16 EndY=8 EndZ=0
    g77: ArcOfCircle CenterX=15.0954 CenterY=6.49778 CenterZ=0 NormalX=0 NormalY=0 NormalZ=1 Radius=1.75357 StartAngle=1.02877 EndAngle=2.11282
    g78: ArcOfCircle CenterX=12.915 CenterY=10.15 CenterZ=0 NormalX=0 NormalY=0 NormalZ=1 Radius=2.5 StartAngle=4.00332 EndAngle=5.24792
    g79: LineSegment StartX=11.2872 StartY=8.25258 StartZ=0 EndX=10.5801 EndY=8.85919 EndZ=0
    g80: ArcOfCircle CenterX=35.3785 CenterY=3.67875 CenterZ=0 NormalX=0 NormalY=0 NormalZ=1 Radius=3.32347 StartAngle=1.60736 EndAngle=2.34401
    g81: LineSegment StartX=35.257 StartY=7 StartZ=0 EndX=35.5 EndY=7 EndZ=0
    g82: LineSegment StartX=35.5 StartY=7 StartZ=0 EndX=42.5 EndY=7 EndZ=0
    g83: LineSegment StartX=42.5 StartY=7 StartZ=0 EndX=43 EndY=6.5 EndZ=0
    g84: LineSegment StartX=43 StartY=6.5 StartZ=0 EndX=43 EndY=3.5 EndZ=0
    g85: LineSegment StartX=43 StartY=3.5 StartZ=0 EndX=42 EndY=2.5 EndZ=0
    g86: LineSegment StartX=42 StartY=2.5 StartZ=0 EndX=32 EndY=2.5 EndZ=0
    g87: LineSegment StartX=32 StartY=2.5 StartZ=0 EndX=31.9251 EndY=2.5 EndZ=0
    g88: ArcOfCircle CenterX=31.9625 CenterY=3.55835 CenterZ=0 NormalX=0 NormalY=0 NormalZ=1 Radius=1.05902 StartAngle=2.71141 EndAngle=4.677
    g89: LineSegment StartX=31 StartY=4 StartZ=0 EndX=33 EndY=6 EndZ=0
    g90: ArcOfCircle CenterX=35.3785 CenterY=3.67877 CenterZ=0 NormalX=0 NormalY=0 NormalZ=1 Radius=3.32345 StartAngle=2.34401 EndAngle=2.36838
    g91: LineSegment StartX=1 StartY=20.2 StartZ=0 EndX=1 EndY=20 EndZ=0
    g92: ArcOfCircle CenterX=1.5 CenterY=20 CenterZ=0 NormalX=0 NormalY=0 NormalZ=1 Radius=0.5 StartAngle=3.14159 EndAngle=6.28319
    g93: LineSegment StartX=2 StartY=20 StartZ=0 EndX=3 EndY=20 EndZ=0
    g94: LineSegment StartX=3 StartY=20 StartZ=0 EndX=3 EndY=18.5 EndZ=0
    g95: LineSegment StartX=3 StartY=18.5 StartZ=0 EndX=3 EndY=16.453 EndZ=0
    g96: ArcOfCircle CenterX=-4.40278e-07 CenterY=8.5 CenterZ=0 NormalX=0 NormalY=0 NormalZ=1 Radius=8.5 StartAngle=1.0472 EndAngle=1.21008
    g97: ArcOfCircle CenterX=-4.4748e-08 CenterY=8.5 CenterZ=0 NormalX=0 NormalY=0 NormalZ=1 Radius=8.5 StartAngle=0.703721 EndAngle=1.0472
    g98: LineSegment StartX=6.48074 StartY=14 StartZ=0 EndX=11 EndY=14 EndZ=0
    g99: LineSegment StartX=11 StartY=14 StartZ=0 EndX=11 EndY=13.21 EndZ=0
    g100: ArcOfCircle CenterX=11.355 CenterY=12.855 CenterZ=0 NormalX=0 NormalY=0 NormalZ=1 Radius=0.502046 StartAngle=2.35619 EndAngle=5.49779
    g101: LineSegment StartX=11.71 StartY=12.5 StartZ=0 EndX=14.29 EndY=12.5 EndZ=0
    g102: ArcOfCircle CenterX=14.645 CenterY=12.855 CenterZ=0 NormalX=0 NormalY=0 NormalZ=1 Radius=0.502046 StartAngle=3.92699 EndAngle=7.06858
    g103: LineSegment StartX=15 StartY=13.21 StartZ=0 EndX=15 EndY=14 EndZ=0
    g104: LineSegment StartX=15 StartY=14 StartZ=0 EndX=27.29 EndY=14 EndZ=0
    g105: ArcOfCircle CenterX=27.645 CenterY=14.355 CenterZ=0 NormalX=0 NormalY=0 NormalZ=1 Radius=0.502046 StartAngle=3.92699 EndAngle=7.06858
    g106: LineSegment StartX=28 StartY=14.71 StartZ=0 EndX=28 EndY=20 EndZ=0
    g107: LineSegment StartX=28 StartY=20 StartZ=0 EndX=28 EndY=21.5 EndZ=0
    g108: ArcOfCircle CenterX=28.5 CenterY=21.5 CenterZ=0 NormalX=0 NormalY=0 NormalZ=1 Radius=0.5 StartAngle=1.5708 EndAngle=3.14159
    g109: LineSegment StartX=28.5 StartY=22 StartZ=0 EndX=30.5 EndY=22 EndZ=0
    g110: ArcOfCircle CenterX=30.5 CenterY=21.5 CenterZ=0 NormalX=0 NormalY=0 NormalZ=1 Radius=0.5 StartAngle=0 EndAngle=1.5708
    g111: LineSegment StartX=31 StartY=21.5 StartZ=0 EndX=31 EndY=21.2 EndZ=0
    g112: LineSegment StartX=31 StartY=21.2 StartZ=0 EndX=30 EndY=21.2 EndZ=0
    g113: ArcOfCircle CenterX=30 CenterY=20.7 CenterZ=0 NormalX=0 NormalY=0 NormalZ=1 Radius=0.5 StartAngle=1.5708 EndAngle=4.71239
    g114: LineSegment StartX=30 StartY=20.2 StartZ=0 EndX=31 EndY=20.2 EndZ=0
    g115: LineSegment StartX=31 StartY=20.2 StartZ=0 EndX=31 EndY=20 EndZ=0
    g116: ArcOfCircle CenterX=31.5 CenterY=20 CenterZ=0 NormalX=0 NormalY=0 NormalZ=1 Radius=0.5 StartAngle=3.14159 EndAngle=6.28319
    g117: LineSegment StartX=32 StartY=20 StartZ=0 EndX=33.5 EndY=20 EndZ=0
    g118: LineSegment StartX=33.5 StartY=20 StartZ=0 EndX=33.5 EndY=14.5 EndZ=0
    g119: LineSegment StartX=33.5 StartY=14.5 StartZ=0 EndX=33.5 EndY=9 EndZ=0
    g120: ArcOfCircle CenterX=34 CenterY=9 CenterZ=0 NormalX=0 NormalY=0 NormalZ=1 Radius=0.5 StartAngle=3.14159 EndAngle=6.28319
    g121: LineSegment StartX=34.5 StartY=9 StartZ=0 EndX=46.5 EndY=9 EndZ=0
    g122: LineSegment StartX=46.5 StartY=9 StartZ=0 EndX=46.5 EndY=8 EndZ=0
    g123: LineSegment StartX=46.5 StartY=8 StartZ=0 EndX=45 EndY=6.5 EndZ=0
    g124: LineSegment StartX=45 StartY=6.5 StartZ=0 EndX=45 EndY=3.5 EndZ=0
    g125: LineSegment StartX=45 StartY=3.5 StartZ=0 EndX=46.5 EndY=2 EndZ=0
    g126: LineSegment StartX=46.5 StartY=2 StartZ=0 EndX=46.5 EndY=1 EndZ=0
    g127: LineSegment StartX=46.5 StartY=1 StartZ=0 EndX=45 EndY=1 EndZ=0
    g128: ArcOfCircle CenterX=44.5 CenterY=1 CenterZ=0 NormalX=0 NormalY=0 NormalZ=1 Radius=0.5 StartAngle=0 EndAngle=3.14159
    g129: LineSegment StartX=44 StartY=1 StartZ=0 EndX=44 EndY=0.8 EndZ=0
    g130: LineSegment StartX=44 StartY=0.8 StartZ=0 EndX=43 EndY=0.8 EndZ=0
    g131: ArcOfCircle CenterX=43 CenterY=0.3 CenterZ=0 NormalX=0 NormalY=0 NormalZ=1 Radius=0.5 StartAngle=1.5708 EndAngle=4.71239
    g132: LineSegment StartX=43 StartY=-0.2 StartZ=0 EndX=44 EndY=-0.2 EndZ=0
    g133: LineSegment StartX=44 StartY=-0.2 StartZ=0 EndX=44 EndY=-0.5 EndZ=0
    g134: ArcOfCircle CenterX=43.5 CenterY=-0.5 CenterZ=0 NormalX=0 NormalY=0 NormalZ=1 Radius=0.5 StartAngle=4.71239 EndAngle=6.28319
    g135: LineSegment StartX=43.5 StartY=-1 StartZ=0 EndX=41.5 EndY=-1 EndZ=0
    g136: ArcOfCircle CenterX=41.5 CenterY=-0.5 CenterZ=0 NormalX=0 NormalY=0 NormalZ=1 Radius=0.5 StartAngle=3.14159 EndAngle=4.71239
    g137: LineSegment StartX=41 StartY=-0.5 StartZ=0 EndX=41 EndY=0.29 EndZ=0
    g138: ArcOfCircle CenterX=40.645 CenterY=0.645 CenterZ=0 NormalX=0 NormalY=0 NormalZ=1 Radius=0.502046 StartAngle=5.49779 EndAngle=8.63938
    g139: LineSegment StartX=40.29 StartY=1 StartZ=0 EndX=10.21 EndY=1 EndZ=0
    g140: ArcOfCircle CenterX=9.855 CenterY=0.645 CenterZ=0 NormalX=0 NormalY=0 NormalZ=1 Radius=0.502046 StartAngle=0.785398 EndAngle=3.92699
    g141: LineSegment StartX=9.5 StartY=0.29 StartZ=0 EndX=9.5 EndY=-0.5 EndZ=0
    g142: ArcOfCircle CenterX=9 CenterY=-0.5 CenterZ=0 NormalX=0 NormalY=0 NormalZ=1 Radius=0.5 StartAngle=4.71239 EndAngle=6.28319
    g143: LineSegment StartX=9 StartY=-1 StartZ=0 EndX=7 EndY=-1 EndZ=0
    g144: ArcOfCircle CenterX=7 CenterY=-0.5 CenterZ=0 NormalX=0 NormalY=0 NormalZ=1 Radius=0.5 StartAngle=3.14159 EndAngle=4.71239
    g145: LineSegment StartX=6.5 StartY=-0.5 StartZ=0 EndX=6.5 EndY=-0.2 EndZ=0
    g146: LineSegment StartX=6.5 StartY=-0.2 StartZ=0 EndX=7.5 EndY=-0.2 EndZ=0
    g147: ArcOfCircle CenterX=7.5 CenterY=0.3 CenterZ=0 NormalX=0 NormalY=0 NormalZ=1 Radius=0.5 StartAngle=4.71239 EndAngle=7.85398
    g148: LineSegment StartX=7.5 StartY=0.8 StartZ=0 EndX=6.5 EndY=0.8 EndZ=0
    g149: LineSegment StartX=6.5 StartY=0.8 StartZ=0 EndX=6.5 EndY=1 EndZ=0
    g150: ArcOfCircle CenterX=6 CenterY=1 CenterZ=0 NormalX=0 NormalY=0 NormalZ=1 Radius=0.5 StartAngle=0 EndAngle=3.14159
    g151: LineSegment StartX=5.5 StartY=1 StartZ=0 EndX=0 EndY=1 EndZ=0
    g152: LineSegment StartX=0 StartY=1 StartZ=0 EndX=-5.5 EndY=1 EndZ=0
    g153: ArcOfCircle CenterX=-6 CenterY=1 CenterZ=0 NormalX=0 NormalY=0 NormalZ=1 Radius=0.5 StartAngle=0 EndAngle=3.14159
    g154: LineSegment StartX=-6.5 StartY=1 StartZ=0 EndX=-6.5 EndY=0.8 EndZ=0
    g155: LineSegment StartX=-6.5 StartY=0.8 StartZ=0 EndX=-7.5 EndY=0.8 EndZ=0
    g156: ArcOfCircle CenterX=-7.5 CenterY=0.3 CenterZ=0 NormalX=0 NormalY=0 NormalZ=1 Radius=0.5 StartAngle=1.5708 EndAngle=4.71239
    g157: LineSegment StartX=-7.5 StartY=-0.2 StartZ=0 EndX=-6.5 EndY=-0.2 EndZ=0
    g158: LineSegment StartX=-6.5 StartY=-0.2 StartZ=0 EndX=-6.5 EndY=-0.5 EndZ=0
    g159: ArcOfCircle CenterX=-7 CenterY=-0.5 CenterZ=0 NormalX=0 NormalY=0 NormalZ=1 Radius=0.5 StartAngle=4.71239 EndAngle=6.28319
    g160: LineSegment StartX=-7 StartY=-1 StartZ=0 EndX=-9 EndY=-1 EndZ=0
    g161: ArcOfCircle CenterX=-9 CenterY=-0.5 CenterZ=0 NormalX=0 NormalY=0 NormalZ=1 Radius=0.5 StartAngle=3.14159 EndAngle=4.71239
    g162: LineSegment StartX=-9.5 StartY=-0.5 StartZ=0 EndX=-9.5 EndY=0.29 EndZ=0
    g163: ArcOfCircle CenterX=-9.855 CenterY=0.645 CenterZ=0 NormalX=0 NormalY=0 NormalZ=1 Radius=0.502046 StartAngle=5.49779 EndAngle=8.63938
    g164: LineSegment StartX=-10.21 StartY=1 StartZ=0 EndX=-29.79 EndY=1 EndZ=0
    g165: ArcOfCircle CenterX=-30.145 CenterY=0.645 CenterZ=0 NormalX=0 NormalY=0 NormalZ=1 Radius=0.502046 StartAngle=0.785398 EndAngle=3.92699
    g166: LineSegment StartX=-30.5 StartY=0.29 StartZ=0 EndX=-30.5 EndY=-0.5 EndZ=0
    g167: ArcOfCircle CenterX=-31 CenterY=-0.5 CenterZ=0 NormalX=0 NormalY=0 NormalZ=1 Radius=0.5 StartAngle=4.71239 EndAngle=6.28319
    g168: LineSegment StartX=-31 StartY=-1 StartZ=0 EndX=-33 EndY=-1 EndZ=0
    g169: ArcOfCircle CenterX=-33 CenterY=-0.5 CenterZ=0 NormalX=0 NormalY=0 NormalZ=1 Radius=0.5 StartAngle=3.14159 EndAngle=4.71239
    g170: LineSegment StartX=-33.5 StartY=-0.5 StartZ=0 EndX=-33.5 EndY=-0.2 EndZ=0
    g171: LineSegment StartX=-33.5 StartY=-0.2 StartZ=0 EndX=-32.5 EndY=-0.2 EndZ=0
    g172: ArcOfCircle CenterX=-32.5 CenterY=0.3 CenterZ=0 NormalX=0 NormalY=0 NormalZ=1 Radius=0.5 StartAngle=4.71239 EndAngle=7.85398
    g173: LineSegment StartX=-32.5 StartY=0.8 StartZ=0 EndX=-33.5 EndY=0.8 EndZ=0
    g174: LineSegment StartX=-33.5 StartY=0.8 StartZ=0 EndX=-33.5 EndY=1 EndZ=0
    g175: ArcOfCircle CenterX=-34 CenterY=1 CenterZ=0 NormalX=0 NormalY=0 NormalZ=1 Radius=0.5 StartAngle=0 EndAngle=3.14159
    g176: LineSegment StartX=-34.5 StartY=1 StartZ=0 EndX=-36 EndY=1 EndZ=0
    g177: LineSegment StartX=-36 StartY=1 StartZ=0 EndX=-36 EndY=2 EndZ=0
    g178: LineSegment StartX=-36 StartY=2 StartZ=0 EndX=-34 EndY=4 EndZ=0
    g179: LineSegment StartX=-34 StartY=4 StartZ=0 EndX=-34 EndY=10 EndZ=0
    g180: LineSegment StartX=-34 StartY=10 StartZ=0 EndX=-36 EndY=12 EndZ=0
    g181: LineSegment StartX=-36 StartY=12 StartZ=0 EndX=-36 EndY=14.5 EndZ=0
    g182: LineSegment StartX=-36 StartY=14.5 StartZ=0 EndX=-36 EndY=20 EndZ=0
    g183: LineSegment StartX=-36 StartY=20 StartZ=0 EndX=-34.5 EndY=20 EndZ=0
    g184: ArcOfCircle CenterX=-34 CenterY=20 CenterZ=0 NormalX=0 NormalY=0 NormalZ=1 Radius=0.5 StartAngle=3.14159 EndAngle=6.28319
    g185: LineSegment StartX=-33.5 StartY=20 StartZ=0 EndX=-33.5 EndY=20.2 EndZ=0
    g186: LineSegment StartX=-33.5 StartY=20.2 StartZ=0 EndX=-32.5 EndY=20.2 EndZ=0
    g187: ArcOfCircle CenterX=-32.5 CenterY=20.7 CenterZ=0 NormalX=0 NormalY=0 NormalZ=1 Radius=0.5 StartAngle=4.71239 EndAngle=7.85398
    g188: LineSegment StartX=-32.5 StartY=21.2 StartZ=0 EndX=-33.5 EndY=21.2 EndZ=0
    g189: LineSegment StartX=-33.5 StartY=21.2 StartZ=0 EndX=-33.5 EndY=21.5 EndZ=0
    g190: ArcOfCircle CenterX=-33 CenterY=21.5 CenterZ=0 NormalX=0 NormalY=0 NormalZ=1 Radius=0.5 StartAngle=1.5708 EndAngle=3.14159
    g191: LineSegment StartX=-33 StartY=22 StartZ=0 EndX=-31 EndY=22 EndZ=0
    g192: ArcOfCircle CenterX=-31 CenterY=21.5 CenterZ=0 NormalX=0 NormalY=0 NormalZ=1 Radius=0.5 StartAngle=0 EndAngle=1.5708
    g193: LineSegment StartX=-30.5 StartY=21.5 StartZ=0 EndX=-30.5 EndY=14.71 EndZ=0
    g194: ArcOfCircle CenterX=-30.145 CenterY=14.355 CenterZ=0 NormalX=0 NormalY=0 NormalZ=1 Radius=0.502046 StartAngle=2.35619 EndAngle=5.49779
    g195: LineSegment StartX=-29.79 StartY=14 StartZ=0 EndX=-15 EndY=14 EndZ=0
    g196: LineSegment StartX=-15 StartY=14 StartZ=0 EndX=-15 EndY=13.21 EndZ=0
    g197: ArcOfCircle CenterX=-14.645 CenterY=12.855 CenterZ=0 NormalX=0 NormalY=0 NormalZ=1 Radius=0.502046 StartAngle=2.35619 EndAngle=5.49779
    g198: LineSegment StartX=-14.29 StartY=12.5 StartZ=0 EndX=-11.71 EndY=12.5 EndZ=0
    g199: ArcOfCircle CenterX=-11.355 CenterY=12.855 CenterZ=0 NormalX=0 NormalY=0 NormalZ=1 Radius=0.502046 StartAngle=3.92699 EndAngle=7.06858
    g200: LineSegment StartX=-11 StartY=13.21 StartZ=0 EndX=-11 EndY=14 EndZ=0
    g201: LineSegment StartX=-11 StartY=14 StartZ=0 EndX=-6.48074 EndY=14 EndZ=0
    g202: ArcOfCircle CenterX=4.4748e-08 CenterY=8.5 CenterZ=0 NormalX=0 NormalY=0 NormalZ=1 Radius=8.5 StartAngle=2.0944 EndAngle=2.43787
    g203: ArcOfCircle CenterX=4.40278e-07 CenterY=8.5 CenterZ=0 NormalX=0 NormalY=0 NormalZ=1 Radius=8.5 StartAngle=1.93151 EndAngle=2.0944
    g204: LineSegment StartX=-3 StartY=16.453 StartZ=0 EndX=-3 EndY=20 EndZ=0
    g205: LineSegment StartX=-3 StartY=20 StartZ=0 EndX=-2.21 EndY=20 EndZ=0
    g206: ArcOfCircle CenterX=-1.855 CenterY=20.355 CenterZ=0 NormalX=0 NormalY=0 NormalZ=1 Radius=0.502046 StartAngle=3.92699 EndAngle=7.06858
    g207: LineSegment StartX=-1.5 StartY=20.71 StartZ=0 EndX=-1.5 EndY=21.5 EndZ=0
    g208: ArcOfCircle CenterX=-1 CenterY=21.5 CenterZ=0 NormalX=0 NormalY=0 NormalZ=1 Radius=0.5 StartAngle=1.5708 EndAngle=3.14159
    g209: LineSegment StartX=-1 StartY=22 StartZ=0 EndX=1 EndY=22 EndZ=0
    g210: ArcOfCircle CenterX=1 CenterY=21.5 CenterZ=0 NormalX=0 NormalY=0 NormalZ=1 Radius=0.5 StartAngle=0 EndAngle=1.5708
    g211: LineSegment StartX=1.5 StartY=21.5 StartZ=0 EndX=1.5 EndY=21.2 EndZ=0
    g212: LineSegment StartX=1.5 StartY=21.2 StartZ=0 EndX=0.5 EndY=21.2 EndZ=0
    g213: ArcOfCircle CenterX=0.5 CenterY=20.7 CenterZ=0 NormalX=0 NormalY=0 NormalZ=1 Radius=0.5 StartAngle=1.5708 EndAngle=4.71239
    g214: LineSegment StartX=0.5 StartY=20.2 StartZ=0 EndX=1 EndY=20.2 EndZ=0
    g215: ArcOfCircle CenterX=25.6032 CenterY=9.13303 CenterZ=0 NormalX=0 NormalY=0 NormalZ=1 Radius=3.36855 StartAngle=0.791658 EndAngle=1.54015
    g216: LineSegment StartX=25.7064 StartY=12.5 StartZ=0 EndX=25.5 EndY=12.5 EndZ=0
    g217: LineSegment StartX=25.5 StartY=12.5 StartZ=0 EndX=19.5 EndY=12.5 EndZ=0
    g218: LineSegment StartX=19.5 StartY=12.5 StartZ=0 EndX=19.1908 EndY=12.5 EndZ=0
    g219: ArcOfCircle CenterX=19.3454 CenterY=8.39955 CenterZ=0 NormalX=0 NormalY=0 NormalZ=1 Radius=4.10336 StartAngle=1.60849 EndAngle=2.33703
    g220: ArcOfCircle CenterX=17.1106 CenterY=10.9281 CenterZ=0 NormalX=0 NormalY=0 NormalZ=1 Radius=0.745725 StartAngle=2.53017 EndAngle=3.75301
    g221: LineSegment StartX=16.5 StartY=10.5 StartZ=0 EndX=24 EndY=3 EndZ=0
    g222: ArcOfCircle CenterX=25.5 CenterY=5 CenterZ=0 NormalX=0 NormalY=0 NormalZ=1 Radius=2.5 StartAngle=4.06889 EndAngle=4.71239
    g223: ArcOfCircle CenterX=25.5 CenterY=5 CenterZ=0 NormalX=0 NormalY=0 NormalZ=1 Radius=2.5 StartAngle=4.71239 EndAngle=5.35589
    g224: LineSegment StartX=27 StartY=3 StartZ=0 EndX=30.5 EndY=6.5 EndZ=0
    g225: ArcOfCircle CenterX=28.9877 CenterY=7.75 CenterZ=0 NormalX=0 NormalY=0 NormalZ=1 Radius=1.96205 StartAngle=5.59247 EndAngle=6.9739
    g226: LineSegment StartX=30.5 StartY=9 StartZ=0 EndX=28 EndY=11.5 EndZ=0
    g227: ArcOfCircle CenterX=25.6032 CenterY=9.13305 CenterZ=0 NormalX=0 NormalY=0 NormalZ=1 Radius=3.36853 StartAngle=0.779138 EndAngle=0.791658
    g228: LineSegment StartX=-33.29 StartY=15.5 StartZ=0 EndX=-33.21 EndY=15.5 EndZ=0
    g229: ArcOfCircle CenterX=-32.855 CenterY=15.855 CenterZ=0 NormalX=0 NormalY=0 NormalZ=1 Radius=0.502046 StartAngle=3.92699 EndAngle=7.06858
    g230: LineSegment StartX=-32.5 StartY=16.21 StartZ=0 EndX=-32.5 EndY=17.79 EndZ=0
    g231: ArcOfCircle CenterX=-32.855 CenterY=18.145 CenterZ=0 NormalX=0 NormalY=0 NormalZ=1 Radius=0.502046 StartAngle=5.49779 EndAngle=8.63938
    g232: LineSegment StartX=-33.21 StartY=18.5 StartZ=0 EndX=-33.29 EndY=18.5 EndZ=0
    g233: ArcOfCircle CenterX=-33.645 CenterY=18.145 CenterZ=0 NormalX=0 NormalY=0 NormalZ=1 Radius=0.502046 StartAngle=0.785398 EndAngle=3.92699
    g234: LineSegment StartX=-34 StartY=17.79 StartZ=0 EndX=-34 EndY=16.21 EndZ=0
    g235: ArcOfCircle CenterX=-33.645 CenterY=15.855 CenterZ=0 NormalX=0 NormalY=0 NormalZ=1 Radius=0.502046 StartAngle=2.35619 EndAngle=5.49779
    g236: Circle CenterX=0 CenterY=8.5 CenterZ=0 NormalX=0 NormalY=0 NormalZ=1 Radius=3.5
    g237: Circle CenterX=12.915 CenterY=10.15 CenterZ=0 NormalX=0 NormalY=0 NormalZ=1 Radius=1
    g238: Circle CenterX=-12.915 CenterY=10.15 CenterZ=0 NormalX=0 NormalY=0 NormalZ=1 Radius=1
FEATURE [PartDesign::Pad] Pad028
  Length = 1.5
  Length2 = 100
  Sketch = -> Sketch281
  Type = 0
FEATURE [App::DocumentObjectGroup] entretoises_internes
  Group = -> [Pad028]
FEATURE [Part::FeaturePython] Clone132  label="Clone of Pad028"  # Draft clone (typed FeaturePython)
  Objects = -> [Pad028]
  Placement = pos=(19.5,0,0) rot=(0.57735,0.57735,0.57735;2.0944rad)
  Scale = (1,1,1)
FEATURE [Part::FeaturePython] Clone133  label="Clone of Pad032"  # Draft clone (typed FeaturePython)
  Objects = -> [Pad028]
  Placement = pos=(-21,0,0) rot=(0.57735,0.57735,0.57735;2.0944rad)
  Scale = (1,1,1)
FEATURE [Sketcher::SketchObject] Sketch282
  Placement = pos=(0,-32.5,14) rot=(1,0,0;1.5708rad)
  sketch-geometry (50):
    g0: ArcOfCircle CenterX=16.5 CenterY=3 CenterZ=0 NormalX=0 NormalY=0 NormalZ=1 Radius=1.5 StartAngle=4.71239 EndAngle=7.85398
    g1: LineSegment StartX=16.5 StartY=1.5 StartZ=0 EndX=8.5 EndY=1.5 EndZ=0
    g2: ArcOfCircle CenterX=8.5 CenterY=3 CenterZ=0 NormalX=0 NormalY=0 NormalZ=1 Radius=1.5 StartAngle=1.5708 EndAngle=4.71239
    g3: LineSegment StartX=8.5 StartY=4.5 StartZ=0 EndX=16.5 EndY=4.5 EndZ=0
    g4: ArcOfCircle CenterX=-16.5 CenterY=3 CenterZ=0 NormalX=0 NormalY=0 NormalZ=1 Radius=1.5 StartAngle=1.5708 EndAngle=4.71239
    g5: LineSegment StartX=-16.5 StartY=1.5 StartZ=0 EndX=-8.5 EndY=1.5 EndZ=0
    g6: ArcOfCircle CenterX=-8.5 CenterY=3 CenterZ=0 NormalX=0 NormalY=0 NormalZ=1 Radius=1.5 StartAngle=4.71239 EndAngle=7.85398
    g7: LineSegment StartX=-8.5 StartY=4.5 StartZ=0 EndX=-16.5 EndY=4.5 EndZ=0
    g8: ArcOfCircle CenterX=-4 CenterY=3 CenterZ=0 NormalX=0 NormalY=0 NormalZ=1 Radius=1.5 StartAngle=1.5708 EndAngle=4.71239
    g9: LineSegment StartX=-4 StartY=1.5 StartZ=0 EndX=4 EndY=1.5 EndZ=0
    g10: ArcOfCircle CenterX=4 CenterY=3 CenterZ=0 NormalX=0 NormalY=0 NormalZ=1 Radius=1.5 StartAngle=4.71239 EndAngle=7.85398
    g11: LineSegment StartX=4 StartY=4.5 StartZ=0 EndX=-4 EndY=4.5 EndZ=0
    g12: LineSegment StartX=-19.5 StartY=4.5 StartZ=0 EndX=-21 EndY=4.5 EndZ=0
    g13: LineSegment StartX=-21 StartY=4.5 StartZ=0 EndX=-21 EndY=1.5 EndZ=0
    g14: LineSegment StartX=-21 StartY=1.5 StartZ=0 EndX=-19.5 EndY=1.5 EndZ=0
    g15: ArcOfCircle CenterX=-19.5 CenterY=1 CenterZ=0 NormalX=0 NormalY=0 NormalZ=1 Radius=0.5 StartAngle=0 EndAngle=1.5708
    g16: ArcOfCircle CenterX=-19.5 CenterY=1 CenterZ=0 NormalX=0 NormalY=0 NormalZ=1 Radius=0.5 StartAngle=4.71239 EndAngle=6.28319
    g17: LineSegment StartX=-19.5 StartY=0.5 StartZ=0 EndX=-19.5 EndY=0 EndZ=0
    g18: LineSegment StartX=-19.5 StartY=0 StartZ=0 EndX=-17.5 EndY=0 EndZ=0
    g19: LineSegment StartX=-17.5 StartY=0 StartZ=0 EndX=-17 EndY=0.5 EndZ=0
    g20: LineSegment StartX=-17 StartY=0.5 StartZ=0 EndX=-1.5 EndY=0.5 EndZ=0
    g21: LineSegment StartX=-1.5 StartY=0.5 StartZ=0 EndX=-1 EndY=0 EndZ=0
    g22: LineSegment StartX=-1 StartY=0 StartZ=0 EndX=0 EndY=0 EndZ=0
    g23: LineSegment StartX=0 StartY=0 StartZ=0 EndX=1 EndY=0 EndZ=0
    g24: LineSegment StartX=1 StartY=0 StartZ=0 EndX=1.5 EndY=0.5 EndZ=0
    g25: LineSegment StartX=1.5 StartY=0.5 StartZ=0 EndX=17 EndY=0.5 EndZ=0
    g26: LineSegment StartX=17 StartY=0.5 StartZ=0 EndX=17.5 EndY=0 EndZ=0
    g27: LineSegment StartX=17.5 StartY=0 StartZ=0 EndX=19.5 EndY=0 EndZ=0
    g28: LineSegment StartX=19.5 StartY=0 StartZ=0 EndX=19.5 EndY=0.5 EndZ=0
    g29: ArcOfCircle CenterX=19.5 CenterY=1 CenterZ=0 NormalX=0 NormalY=0 NormalZ=1 Radius=0.5 StartAngle=3.14159 EndAngle=4.71239
    g30: ArcOfCircle CenterX=19.5 CenterY=1 CenterZ=0 NormalX=0 NormalY=0 NormalZ=1 Radius=0.5 StartAngle=1.5708 EndAngle=3.14159
    g31: LineSegment StartX=19.5 StartY=1.5 StartZ=0 EndX=21 EndY=1.5 EndZ=0
    g32: LineSegment StartX=21 StartY=1.5 StartZ=0 EndX=21 EndY=4.5 EndZ=0
    g33: LineSegment StartX=21 StartY=4.5 StartZ=0 EndX=19.5 EndY=4.5 EndZ=0
    g34: ArcOfCircle CenterX=19.5 CenterY=5 CenterZ=0 NormalX=0 NormalY=0 NormalZ=1 Radius=0.5 StartAngle=3.14159 EndAngle=4.71239
    g35: ArcOfCircle CenterX=19.5 CenterY=5 CenterZ=0 NormalX=0 NormalY=0 NormalZ=1 Radius=0.5 StartAngle=1.5708 EndAngle=3.14159
    g36: LineSegment StartX=19.5 StartY=5.5 StartZ=0 EndX=19.5 EndY=6 EndZ=0
    g37: LineSegment StartX=19.5 StartY=6 StartZ=0 EndX=17.5 EndY=6 EndZ=0
    g38: LineSegment StartX=17.5 StartY=6 StartZ=0 EndX=17 EndY=5.5 EndZ=0
    g39: LineSegment StartX=17 StartY=5.5 StartZ=0 EndX=1.5 EndY=5.5 EndZ=0
    g40: LineSegment StartX=1.5 StartY=5.5 StartZ=0 EndX=1 EndY=6 EndZ=0
    g41: LineSegment StartX=1 StartY=6 StartZ=0 EndX=0 EndY=6 EndZ=0
    g42: LineSegment StartX=0 StartY=6 StartZ=0 EndX=-1 EndY=6 EndZ=0
    g43: LineSegment StartX=-1 StartY=6 StartZ=0 EndX=-1.5 EndY=5.5 EndZ=0
    g44: LineSegment StartX=-1.5 StartY=5.5 StartZ=0 EndX=-17 EndY=5.5 EndZ=0
    g45: LineSegment StartX=-17 StartY=5.5 StartZ=0 EndX=-17.5 EndY=6 EndZ=0
    g46: LineSegment StartX=-17.5 StartY=6 StartZ=0 EndX=-19.5 EndY=6 EndZ=0
    g47: LineSegment StartX=-19.5 StartY=6 StartZ=0 EndX=-19.5 EndY=5.5 EndZ=0
    g48: ArcOfCircle CenterX=-19.5 CenterY=5 CenterZ=0 NormalX=0 NormalY=0 NormalZ=1 Radius=0.5 StartAngle=0 EndAngle=1.5708
    g49: ArcOfCircle CenterX=-19.5 CenterY=5 CenterZ=0 NormalX=0 NormalY=0 NormalZ=1 Radius=0.5 StartAngle=4.71239 EndAngle=6.28319
FEATURE [PartDesign::Pad] Pad047  label="Nervure"
  Length = 1.5
  Length2 = 100
  Placement = pos=(0,-32.5,14) rot=(1,0,0;1.5708rad)
  Sketch = -> Sketch282
  Type = 0
FEATURE [App::DocumentObjectGroup] Groupe043  label="SupportsMoteurs"
  Group = -> [entretoises_internes,entretoises_externes,Clone130,Clone131,Clone132,Clone133,Pad047]
FEATURE [App::DocumentObjectGroup] Groupe011  label="TrainRoulant"
  Group = -> [Groupe019,Groupe003,Groupe043]
FEATURE [Sketcher::SketchObject] Sketch283
  Placement = pos=(0,0,12.5) rot=(0,0,1;0rad)
  sketch-geometry (166):
    g0: ArcOfCircle CenterX=-5.5 CenterY=-28.5 CenterZ=0 NormalX=0 NormalY=0 NormalZ=1 Radius=1.5 StartAngle=5.23599 EndAngle=5.91962
    g1: ArcOfCircle CenterX=-5.5 CenterY=-28.5 CenterZ=0 NormalX=0 NormalY=0 NormalZ=1 Radius=1.5 StartAngle=4.71239 EndAngle=5.23599
    g2: LineSegment StartX=-5.5 StartY=-30 StartZ=0 EndX=-8.5 EndY=-30 EndZ=0
    g3: ArcOfCircle CenterX=-8.5 CenterY=-29 CenterZ=0 NormalX=0 NormalY=0 NormalZ=1 Radius=1 StartAngle=3.14159 EndAngle=4.71239
    g4: ArcOfCircle CenterX=-8.5 CenterY=-29 CenterZ=0 NormalX=0 NormalY=0 NormalZ=1 Radius=1 StartAngle=2.89288 EndAngle=3.14159
    g5: LineSegment StartX=-9.46923 StartY=-28.7538 StartZ=0 EndX=-8.48462 EndY=-24.8769 EndZ=0
    g6: ArcOfCircle CenterX=-8 CenterY=-25 CenterZ=0 NormalX=0 NormalY=0 NormalZ=1 Radius=0.5 StartAngle=2.09439 EndAngle=2.89288
    g7: ArcOfCircle CenterX=-8 CenterY=-25 CenterZ=0 NormalX=0 NormalY=0 NormalZ=1 Radius=0.5 StartAngle=0.854893 EndAngle=2.0944
    g8: LineSegment StartX=-7.67185 StartY=-24.6227 StartZ=0 EndX=-5.5621 EndY=-26.4579 EndZ=0
    g9: ArcOfCircle CenterX=-1.35223e-07 CenterY=-25 CenterZ=0 NormalX=0 NormalY=0 NormalZ=1 Radius=5.75 StartAngle=3.39794 EndAngle=3.91904
    g10: ArcOfCircle CenterX=5.5 CenterY=-28.5 CenterZ=0 NormalX=0 NormalY=0 NormalZ=1 Radius=1.5 StartAngle=3.50516 EndAngle=4.18879
    g11: ArcOfCircle CenterX=5.5 CenterY=-28.5 CenterZ=0 NormalX=0 NormalY=0 NormalZ=1 Radius=1.5 StartAngle=4.18879 EndAngle=4.71239
    g12: LineSegment StartX=5.5 StartY=-30 StartZ=0 EndX=8.5 EndY=-30 EndZ=0
    g13: ArcOfCircle CenterX=8.5 CenterY=-29 CenterZ=0 NormalX=0 NormalY=0 NormalZ=1 Radius=1 StartAngle=4.71239 EndAngle=6.28319
    g14: ArcOfCircle CenterX=8.5 CenterY=-29 CenterZ=0 NormalX=0 NormalY=0 NormalZ=1 Radius=1 StartAngle=6.28318 EndAngle=6.53189
    g15: LineSegment StartX=9.46923 StartY=-28.7538 StartZ=0 EndX=8.48462 EndY=-24.8769 EndZ=0
    g16: ArcOfCircle CenterX=8 CenterY=-25 CenterZ=0 NormalX=0 NormalY=0 NormalZ=1 Radius=0.5 StartAngle=0.248713 EndAngle=1.0472
    g17: ArcOfCircle CenterX=8 CenterY=-25 CenterZ=0 NormalX=0 NormalY=0 NormalZ=1 Radius=0.5 StartAngle=1.0472 EndAngle=2.2867
    g18: LineSegment StartX=7.67185 StartY=-24.6227 StartZ=0 EndX=5.5621 EndY=-26.4579 EndZ=0
    g19: ArcOfCircle CenterX=1.35223e-07 CenterY=-25 CenterZ=0 NormalX=0 NormalY=0 NormalZ=1 Radius=5.75 StartAngle=5.50574 EndAngle=6.02684
    g20: ArcOfCircle CenterX=-5.5 CenterY=28.5 CenterZ=0 NormalX=0 NormalY=0 NormalZ=1 Radius=1.5 StartAngle=0.36357 EndAngle=1.0472
    g21: ArcOfCircle CenterX=-5.5 CenterY=28.5 CenterZ=0 NormalX=0 NormalY=0 NormalZ=1 Radius=1.5 StartAngle=1.0472 EndAngle=1.5708
    g22: LineSegment StartX=-5.5 StartY=30 StartZ=0 EndX=-8.5 EndY=30 EndZ=0
    g23: ArcOfCircle CenterX=-8.5 CenterY=29 CenterZ=0 NormalX=0 NormalY=0 NormalZ=1 Radius=1 StartAngle=1.5708 EndAngle=3.14159
    g24: ArcOfCircle CenterX=-8.5 CenterY=29 CenterZ=0 NormalX=0 NormalY=0 NormalZ=1 Radius=1 StartAngle=3.14159 EndAngle=3.3903
    g25: LineSegment StartX=-9.46923 StartY=28.7538 StartZ=0 EndX=-8.48462 EndY=24.8769 EndZ=0
    g26: ArcOfCircle CenterX=-8 CenterY=25 CenterZ=0 NormalX=0 NormalY=0 NormalZ=1 Radius=0.5 StartAngle=3.39031 EndAngle=4.18879
    g27: ArcOfCircle CenterX=-8 CenterY=25 CenterZ=0 NormalX=0 NormalY=0 NormalZ=1 Radius=0.5 StartAngle=4.18879 EndAngle=5.42829
    g28: LineSegment StartX=-7.67185 StartY=24.6227 StartZ=0 EndX=-5.5621 EndY=26.4579 EndZ=0
    g29: ArcOfCircle CenterX=-1.35223e-07 CenterY=25 CenterZ=0 NormalX=0 NormalY=0 NormalZ=1 Radius=5.75 StartAngle=2.36414 EndAngle=2.88525
    g30: ArcOfCircle CenterX=5.5 CenterY=28.5 CenterZ=0 NormalX=0 NormalY=0 NormalZ=1 Radius=1.5 StartAngle=2.0944 EndAngle=2.77802
    g31: ArcOfCircle CenterX=5.5 CenterY=28.5 CenterZ=0 NormalX=0 NormalY=0 NormalZ=1 Radius=1.5 StartAngle=1.5708 EndAngle=2.0944
    g32: LineSegment StartX=5.5 StartY=30 StartZ=0 EndX=8.5 EndY=30 EndZ=0
    g33: ArcOfCircle CenterX=8.5 CenterY=29 CenterZ=0 NormalX=0 NormalY=0 NormalZ=1 Radius=1 StartAngle=0 EndAngle=1.5708
    g34: ArcOfCircle CenterX=8.5 CenterY=29 CenterZ=0 NormalX=0 NormalY=0 NormalZ=1 Radius=1 StartAngle=6.03448 EndAngle=6.28319
    g35: LineSegment StartX=9.46923 StartY=28.7538 StartZ=0 EndX=8.48462 EndY=24.8769 EndZ=0
    g36: ArcOfCircle CenterX=8 CenterY=25 CenterZ=0 NormalX=0 NormalY=0 NormalZ=1 Radius=0.5 StartAngle=5.23599 EndAngle=6.03447
    g37: ArcOfCircle CenterX=8 CenterY=25 CenterZ=0 NormalX=0 NormalY=0 NormalZ=1 Radius=0.5 StartAngle=3.99649 EndAngle=5.23599
    g38: LineSegment StartX=7.67185 StartY=24.6227 StartZ=0 EndX=5.5621 EndY=26.4579 EndZ=0
    g39: ArcOfCircle CenterX=1.35223e-07 CenterY=25 CenterZ=0 NormalX=0 NormalY=0 NormalZ=1 Radius=5.75 StartAngle=0.256347 EndAngle=0.77745
    g40: LineSegment StartX=14.8333 StartY=33 StartZ=0 EndX=3.9023 EndY=33 EndZ=0
    g41: ArcOfCircle CenterX=0 CenterY=41.011 CenterZ=0 NormalX=0 NormalY=0 NormalZ=1 Radius=8.91093 StartAngle=4.2591 EndAngle=5.16568
    g42: LineSegment StartX=-3.9023 StartY=33 StartZ=0 EndX=-14.8333 EndY=33 EndZ=0
    g43: LineSegment StartX=-14.8333 StartY=33 StartZ=0 EndX=-18 EndY=33 EndZ=0
    g44: LineSegment StartX=-18 StartY=33 StartZ=0 EndX=-19.5 EndY=32.5 EndZ=0
    g45: LineSegment StartX=-19.5 StartY=32.5 StartZ=0 EndX=-21 EndY=32.5 EndZ=0
    g46: LineSegment StartX=-21 StartY=32.5 StartZ=0 EndX=-21 EndY=29 EndZ=0
    g47: LineSegment StartX=-21 StartY=29 StartZ=0 EndX=-19.5 EndY=29 EndZ=0
    g48: ArcOfCircle CenterX=-19.5 CenterY=28.5 CenterZ=0 NormalX=0 NormalY=0 NormalZ=1 Radius=0.5 StartAngle=4.71239 EndAngle=7.85398
    g49: LineSegment StartX=-19.5 StartY=28 StartZ=0 EndX=-19.5 EndY=27.5 EndZ=0
    g50: LineSegment StartX=-19.5 StartY=27.5 StartZ=0 EndX=-15.5 EndY=27 EndZ=0
    g51: ArcOfCircle CenterX=-15.6106 CenterY=25.2965 CenterZ=0 NormalX=0 NormalY=0 NormalZ=1 Radius=1.70711 StartAngle=5.4207 EndAngle=7.78917
    g52: ArcOfCircle CenterX=0.892513 CenterY=10.8937 CenterZ=0 NormalX=0 NormalY=0 NormalZ=1 Radius=20.2164 StartAngle=2.43624 EndAngle=2.9114
    g53: ArcOfCircle CenterX=-19.5 CenterY=15.75 CenterZ=0 NormalX=0 NormalY=0 NormalZ=1 Radius=0.75 StartAngle=4.71239 EndAngle=5.95238
    g54: LineSegment StartX=-19.5 StartY=15 StartZ=0 EndX=-22.5 EndY=15 EndZ=0
    g55: LineSegment StartX=-22.5 StartY=15 StartZ=0 EndX=-22.5 EndY=11 EndZ=0
    g56: LineSegment StartX=-22.5 StartY=11 StartZ=0 EndX=-19.5 EndY=11 EndZ=0
    g57: ArcOfCircle CenterX=-19.5 CenterY=10.25 CenterZ=0 NormalX=0 NormalY=0 NormalZ=1 Radius=0.75 StartAngle=4.71239 EndAngle=7.85398
    g58: LineSegment StartX=-19.5 StartY=9.5 StartZ=0 EndX=-19.5 EndY=8.5 EndZ=0
    g59: LineSegment StartX=-19.5 StartY=8.5 StartZ=0 EndX=-19 EndY=8 EndZ=0
    g60: LineSegment StartX=-19 StartY=8 StartZ=0 EndX=-10.25 EndY=8 EndZ=0
    g61: LineSegment StartX=-10.25 StartY=8 StartZ=0 EndX=-10.25 EndY=19 EndZ=0
    g62: LineSegment StartX=-10.25 StartY=19 StartZ=0 EndX=-9.5 EndY=19 EndZ=0
    g63: ArcOfCircle CenterX=-3.62866 CenterY=13.3831 CenterZ=0 NormalX=0 NormalY=0 NormalZ=1 Radius=8.12543 StartAngle=1.68193 EndAngle=2.37833
    g64: ArcOfCircle CenterX=2.13286e-07 CenterY=25 CenterZ=0 NormalX=0 NormalY=0 NormalZ=1 Radius=5.75 StartAngle=3.80517 EndAngle=4.18879
    g65: ArcOfCircle CenterX=2.42103e-06 CenterY=25 CenterZ=0 NormalX=0 NormalY=0 NormalZ=1 Radius=5.75 StartAngle=4.18879 EndAngle=4.35714
    g66: LineSegment StartX=-2 StartY=19.609 StartZ=0 EndX=-2 EndY=19 EndZ=0
    g67: LineSegment StartX=-2 StartY=19 StartZ=0 EndX=2 EndY=19 EndZ=0
    g68: LineSegment StartX=2 StartY=19 StartZ=0 EndX=2 EndY=19.609 EndZ=0
    g69: ArcOfCircle CenterX=-2.42107e-06 CenterY=25 CenterZ=0 NormalX=0 NormalY=0 NormalZ=1 Radius=5.75 StartAngle=5.06764 EndAngle=5.23599
    g70: ArcOfCircle CenterX=-2.1325e-07 CenterY=25 CenterZ=0 NormalX=0 NormalY=0 NormalZ=1 Radius=5.75 StartAngle=5.23599 EndAngle=5.61961
    g71: ArcOfCircle CenterX=3.62866 CenterY=13.3831 CenterZ=0 NormalX=0 NormalY=0 NormalZ=1 Radius=8.12543 StartAngle=0.763258 EndAngle=1.45966
    g72: LineSegment StartX=9.5 StartY=19 StartZ=0 EndX=10.25 EndY=19 EndZ=0
    g73: LineSegment StartX=10.25 StartY=19 StartZ=0 EndX=10.25 EndY=8 EndZ=0
    g74: LineSegment StartX=10.25 StartY=8 StartZ=0 EndX=19 EndY=8 EndZ=0
    g75: LineSegment StartX=19 StartY=8 StartZ=0 EndX=19.5 EndY=8.5 EndZ=0
    g76: LineSegment StartX=19.5 StartY=8.5 StartZ=0 EndX=19.5 EndY=9.5 EndZ=0
    g77: ArcOfCircle CenterX=19.5 CenterY=10.25 CenterZ=0 NormalX=0 NormalY=0 NormalZ=1 Radius=0.75 StartAngle=1.5708 EndAngle=4.71239
    g78: LineSegment StartX=19.5 StartY=11 StartZ=0 EndX=22.5 EndY=11 EndZ=0
    g79: LineSegment StartX=22.5 StartY=11 StartZ=0 EndX=22.5 EndY=15 EndZ=0
    g80: LineSegment StartX=22.5 StartY=15 StartZ=0 EndX=19.5 EndY=15 EndZ=0
    g81: ArcOfCircle CenterX=19.5 CenterY=15.75 CenterZ=0 NormalX=0 NormalY=0 NormalZ=1 Radius=0.75 StartAngle=3.4724 EndAngle=4.71239
    g82: ArcOfCircle CenterX=-0.892513 CenterY=10.8937 CenterZ=0 NormalX=0 NormalY=0 NormalZ=1 Radius=20.2164 StartAngle=0.230193 EndAngle=0.705348
    g83: ArcOfCircle CenterX=15.6106 CenterY=25.2965 CenterZ=0 NormalX=0 NormalY=0 NormalZ=1 Radius=1.70711 StartAngle=1.63561 EndAngle=4.00407
    g84: LineSegment StartX=15.5 StartY=27 StartZ=0 EndX=19.5 EndY=27.5 EndZ=0
    g85: LineSegment StartX=19.5 StartY=27.5 StartZ=0 EndX=19.5 EndY=28 EndZ=0
    g86: ArcOfCircle CenterX=19.5 CenterY=28.5 CenterZ=0 NormalX=0 NormalY=0 NormalZ=1 Radius=0.5 StartAngle=1.5708 EndAngle=4.71239
    g87: LineSegment StartX=19.5 StartY=29 StartZ=0 EndX=21 EndY=29 EndZ=0
    g88: LineSegment StartX=21 StartY=29 StartZ=0 EndX=21 EndY=32.5 EndZ=0
    g89: LineSegment StartX=21 StartY=32.5 StartZ=0 EndX=19.5 EndY=32.5 EndZ=0
    g90: LineSegment StartX=19.5 StartY=32.5 StartZ=0 EndX=18 EndY=33 EndZ=0
    g91: LineSegment StartX=18 StartY=33 StartZ=0 EndX=14.8333 EndY=33 EndZ=0
    g92: ArcOfCircle CenterX=16.5978 CenterY=-36.9455 CenterZ=0 NormalX=0 NormalY=0 NormalZ=1 Radius=1.05902 StartAngle=4.61995 EndAngle=5.61087
    g93: LineSegment StartX=16.5 StartY=-38 StartZ=0 EndX=9.5 EndY=-37 EndZ=0
    g94: ArcOfCircle CenterX=6.197e-09 CenterY=-46.0066 CenterZ=0 NormalX=0 NormalY=0 NormalZ=1 Radius=13.0908 StartAngle=0.758742 EndAngle=1.16094
    g95: LineSegment StartX=5.21638 StartY=-34 StartZ=0 EndX=-5.21638 EndY=-34 EndZ=0
    g96: ArcOfCircle CenterX=-6.197e-09 CenterY=-46.0066 CenterZ=0 NormalX=0 NormalY=0 NormalZ=1 Radius=13.0908 StartAngle=1.98065 EndAngle=2.38285
    g97: LineSegment StartX=-9.5 StartY=-37 StartZ=0 EndX=-16.5 EndY=-38 EndZ=0
    g98: ArcOfCircle CenterX=-16.5978 CenterY=-36.9455 CenterZ=0 NormalX=0 NormalY=0 NormalZ=1 Radius=1.05902 StartAngle=3.81391 EndAngle=4.80483
    g99: LineSegment StartX=-17.4263 StartY=-37.6051 StartZ=0 EndX=-17.9079 EndY=-37 EndZ=0
    g100: LineSegment StartX=-17.9079 StartY=-37 StartZ=0 EndX=-19.5 EndY=-35 EndZ=0
    g101: LineSegment StartX=-19.5 StartY=-35 StartZ=0 EndX=-21 EndY=-35 EndZ=0
    g102: LineSegment StartX=-21 StartY=-35 StartZ=0 EndX=-21 EndY=-34 EndZ=0
    g103: LineSegment StartX=-21 StartY=-34 StartZ=0 EndX=-21 EndY=-31.5 EndZ=0
    g104: LineSegment StartX=-21 StartY=-31.5 StartZ=0 EndX=-19.5 EndY=-31.5 EndZ=0
    g105: ArcOfCircle CenterX=-19.5 CenterY=-31 CenterZ=0 NormalX=0 NormalY=0 NormalZ=1 Radius=0.5 StartAngle=4.71239 EndAngle=7.85398
    g106: LineSegment StartX=-19.5 StartY=-30.5 StartZ=0 EndX=-19.5 EndY=-30 EndZ=0
    g107: LineSegment StartX=-19.5 StartY=-30 StartZ=0 EndX=-16.5 EndY=-29 EndZ=0
    g108: ArcOfCircle CenterX=-17.2696 CenterY=-25.7922 CenterZ=0 NormalX=0 NormalY=0 NormalZ=1 Radius=3.29885 StartAngle=4.94785 EndAngle=6.85751
    g109: ArcOfCircle CenterX=0.892513 CenterY=-10.8937 CenterZ=0 NormalX=0 NormalY=0 NormalZ=1 Radius=20.2164 StartAngle=3.37179 EndAngle=3.84694
    g110: ArcOfCircle CenterX=-19.5 CenterY=-15.75 CenterZ=0 NormalX=0 NormalY=0 NormalZ=1 Radius=0.75 StartAngle=0.330809 EndAngle=1.5708
    g111: LineSegment StartX=-19.5 StartY=-15 StartZ=0 EndX=-22.5 EndY=-15 EndZ=0
    g112: LineSegment StartX=-22.5 StartY=-15 StartZ=0 EndX=-22.5 EndY=-11 EndZ=0
    g113: LineSegment StartX=-22.5 StartY=-11 StartZ=0 EndX=-19.5 EndY=-11 EndZ=0
    g114: ArcOfCircle CenterX=-19.5 CenterY=-10.25 CenterZ=0 NormalX=0 NormalY=0 NormalZ=1 Radius=0.75 StartAngle=4.71239 EndAngle=7.85398
    g115: LineSegment StartX=-19.5 StartY=-9.5 StartZ=0 EndX=-19.5 EndY=-8.5 EndZ=0
    g116: LineSegment StartX=-19.5 StartY=-8.5 StartZ=0 EndX=-19 EndY=-8 EndZ=0
    g117: LineSegment StartX=-19 StartY=-8 StartZ=0 EndX=-10.25 EndY=-8 EndZ=0
    g118: LineSegment StartX=-10.25 StartY=-8 StartZ=0 EndX=-10.25 EndY=-19 EndZ=0
    g119: LineSegment StartX=-10.25 StartY=-19 StartZ=0 EndX=-9.5 EndY=-19 EndZ=0
    g120: ArcOfCircle CenterX=-3.62866 CenterY=-13.3831 CenterZ=0 NormalX=0 NormalY=0 NormalZ=1 Radius=8.12543 StartAngle=3.90485 EndAngle=4.60125
    g121: ArcOfCircle CenterX=2.13286e-07 CenterY=-25 CenterZ=0 NormalX=0 NormalY=0 NormalZ=1 Radius=5.75 StartAngle=2.0944 EndAngle=2.47802
    g122: ArcOfCircle CenterX=2.42128e-06 CenterY=-25 CenterZ=0 NormalX=0 NormalY=0 NormalZ=1 Radius=5.75 StartAngle=1.92605 EndAngle=2.0944
    g123: LineSegment StartX=-2 StartY=-19.609 StartZ=0 EndX=-2 EndY=-19 EndZ=0
    g124: LineSegment StartX=-2 StartY=-19 StartZ=0 EndX=2 EndY=-19 EndZ=0
    g125: LineSegment StartX=2 StartY=-19 StartZ=0 EndX=2 EndY=-19.609 EndZ=0
    g126: ArcOfCircle CenterX=-2.42107e-06 CenterY=-25 CenterZ=0 NormalX=0 NormalY=0 NormalZ=1 Radius=5.75 StartAngle=1.0472 EndAngle=1.21554
    g127: ArcOfCircle CenterX=-2.13231e-07 CenterY=-25 CenterZ=0 NormalX=0 NormalY=0 NormalZ=1 Radius=5.75 StartAngle=0.663575 EndAngle=1.0472
    g128: ArcOfCircle CenterX=3.62866 CenterY=-13.3831 CenterZ=0 NormalX=0 NormalY=0 NormalZ=1 Radius=8.12543 StartAngle=4.82352 EndAngle=5.51993
    g129: LineSegment StartX=9.5 StartY=-19 StartZ=0 EndX=10.25 EndY=-19 EndZ=0
    g130: LineSegment StartX=10.25 StartY=-19 StartZ=0 EndX=10.25 EndY=-8 EndZ=0
    g131: LineSegment StartX=10.25 StartY=-8 StartZ=0 EndX=19 EndY=-8 EndZ=0
    g132: LineSegment StartX=19 StartY=-8 StartZ=0 EndX=19.5 EndY=-8.5 EndZ=0
    g133: LineSegment StartX=19.5 StartY=-8.5 StartZ=0 EndX=19.5 EndY=-9.5 EndZ=0
    g134: ArcOfCircle CenterX=19.5 CenterY=-10.25 CenterZ=0 NormalX=0 NormalY=0 NormalZ=1 Radius=0.75 StartAngle=1.5708 EndAngle=4.71239
    g135: LineSegment StartX=19.5 StartY=-11 StartZ=0 EndX=22.5 EndY=-11 EndZ=0
    g136: LineSegment StartX=22.5 StartY=-11 StartZ=0 EndX=22.5 EndY=-15 EndZ=0
    g137: LineSegment StartX=22.5 StartY=-15 StartZ=0 EndX=19.5 EndY=-15 EndZ=0
    g138: ArcOfCircle CenterX=19.5 CenterY=-15.75 CenterZ=0 NormalX=0 NormalY=0 NormalZ=1 Radius=0.75 StartAngle=1.5708 EndAngle=2.81078
    g139: ArcOfCircle CenterX=-0.892513 CenterY=-10.8937 CenterZ=0 NormalX=0 NormalY=0 NormalZ=1 Radius=20.2164 StartAngle=5.57784 EndAngle=6.05299
    g140: ArcOfCircle CenterX=17.2696 CenterY=-25.7922 CenterZ=0 NormalX=0 NormalY=0 NormalZ=1 Radius=3.29885 StartAngle=2.56727 EndAngle=4.47693
    g141: LineSegment StartX=16.5 StartY=-29 StartZ=0 EndX=19.5 EndY=-30 EndZ=0
    g142: LineSegment StartX=19.5 StartY=-30 StartZ=0 EndX=19.5 EndY=-30.5 EndZ=0
    g143: ArcOfCircle CenterX=19.5 CenterY=-31 CenterZ=0 NormalX=0 NormalY=0 NormalZ=1 Radius=0.5 StartAngle=1.5708 EndAngle=4.71239
    g144: LineSegment StartX=19.5 StartY=-31.5 StartZ=0 EndX=21 EndY=-31.5 EndZ=0
    g145: LineSegment StartX=21 StartY=-31.5 StartZ=0 EndX=21 EndY=-34 EndZ=0
    g146: LineSegment StartX=21 StartY=-34 StartZ=0 EndX=21 EndY=-35 EndZ=0
    g147: LineSegment StartX=21 StartY=-35 StartZ=0 EndX=19.5 EndY=-35 EndZ=0
    g148: LineSegment StartX=19.5 StartY=-35 StartZ=0 EndX=17.9079 EndY=-37 EndZ=0
    g149: LineSegment StartX=17.9079 StartY=-37 StartZ=0 EndX=17.4263 EndY=-37.6051 EndZ=0
    g150: Circle CenterX=0 CenterY=25 CenterZ=0 NormalX=0 NormalY=0 NormalZ=1 Radius=1.5
    g151: Circle CenterX=0 CenterY=29.25 CenterZ=0 NormalX=0 NormalY=0 NormalZ=1 Radius=0.8
    g152: Circle CenterX=3.5 CenterY=25 CenterZ=0 NormalX=0 NormalY=0 NormalZ=1 Radius=0.8
    g153: Circle CenterX=0 CenterY=20.75 CenterZ=0 NormalX=0 NormalY=0 NormalZ=1 Radius=0.8
    g154: Circle CenterX=-3.5 CenterY=25 CenterZ=0 NormalX=0 NormalY=0 NormalZ=1 Radius=0.8
    g155: Circle CenterX=0 CenterY=-25 CenterZ=0 NormalX=0 NormalY=0 NormalZ=1 Radius=1.5
    g156: Circle CenterX=0 CenterY=-29.25 CenterZ=0 NormalX=0 NormalY=0 NormalZ=1 Radius=0.8
    g157: Circle CenterX=0 CenterY=-20.75 CenterZ=0 NormalX=0 NormalY=0 NormalZ=1 Radius=0.8
    g158: Circle CenterX=-3.5 CenterY=-25 CenterZ=0 NormalX=0 NormalY=0 NormalZ=1 Radius=0.8
    g159: Circle CenterX=3.5 CenterY=-25 CenterZ=0 NormalX=0 NormalY=0 NormalZ=1 Radius=0.8
    g160: Circle CenterX=-16.54 CenterY=31.5 CenterZ=0 NormalX=0 NormalY=0 NormalZ=1 Radius=0.4
    g161: Circle CenterX=-14 CenterY=31.5 CenterZ=0 NormalX=0 NormalY=0 NormalZ=1 Radius=0.4
    g162: Circle CenterX=-11.46 CenterY=31.5 CenterZ=0 NormalX=0 NormalY=0 NormalZ=1 Radius=0.4
    g163: Circle CenterX=-16.54 CenterY=-35.5 CenterZ=0 NormalX=0 NormalY=0 NormalZ=1 Radius=0.4
    g164: Circle CenterX=-14 CenterY=-35.5 CenterZ=0 NormalX=0 NormalY=0 NormalZ=1 Radius=0.4
    g165: Circle CenterX=-11.46 CenterY=-35.5 CenterZ=0 NormalX=0 NormalY=0 NormalZ=1 Radius=0.4
FEATURE [PartDesign::Pad] Pad045  label="SupportTurbine002"
  Length = 1.5
  Length2 = 100
  Placement = pos=(0,0,12.5) rot=(0,0,1;0rad)
  Sketch = -> Sketch283
  Type = 0
FEATURE [App::DocumentObjectGroup] Groupe047  label="PCBTurbine"
  Group = -> [Pad045]
FEATURE [App::DocumentObjectGroup] SupportTurbine
  Group = -> [Groupe047,Groupe051]
FEATURE [App::DocumentObjectGroup] Groupe052  label="Turbines"
  Group = -> [Impeller_5,SupportTurbine,Groupe026]
FEATURE [Sketcher::SketchObject] Sketch287
  sketch-geometry (31):
    g0: LineSegment StartX=-6.70711 StartY=47.3787 StartZ=0 EndX=-4.58579 EndY=50.9142 EndZ=0
    g1: LineSegment StartX=-4.58579 StartY=50.9142 StartZ=0 EndX=-7.41421 EndY=48.0858 EndZ=0
    g2: LineSegment StartX=-7.41421 StartY=48.0858 StartZ=0 EndX=-6.70711 EndY=47.3787 EndZ=0
    g3: LineSegment StartX=3.87868 StartY=50.2071 StartZ=0 EndX=4.58579 EndY=50.9142 EndZ=0
    g4: LineSegment StartX=4.58579 StartY=50.9142 StartZ=0 EndX=7.41421 EndY=48.0858 EndZ=0
    g5: LineSegment StartX=7.41421 StartY=48.0858 StartZ=0 EndX=6.70711 EndY=47.3787 EndZ=0
    g6: LineSegment StartX=6.70711 StartY=47.3787 StartZ=0 EndX=3.87868 EndY=50.2071 EndZ=0
    g7: LineSegment StartX=12.6333 StartY=47.3837 StartZ=0 EndX=9.23104 EndY=50.4906 EndZ=0
    g8: ArcOfCircle CenterX=6.5 CenterY=47.5 CenterZ=0 NormalX=0 NormalY=0 NormalZ=1 Radius=4.05 StartAngle=0.830737 EndAngle=1.0472
    g9: ArcOfCircle CenterX=6.5 CenterY=47.5 CenterZ=0 NormalX=0 NormalY=0 NormalZ=1 Radius=4.05 StartAngle=1.0472 EndAngle=1.5708
    g10: LineSegment StartX=6.5 StartY=51.55 StartZ=0 EndX=0 EndY=51.55 EndZ=0
    g11: LineSegment StartX=0 StartY=51.55 StartZ=0 EndX=-6.5 EndY=51.55 EndZ=0
    g12: ArcOfCircle CenterX=-6.5 CenterY=47.5 CenterZ=0 NormalX=0 NormalY=0 NormalZ=1 Radius=4.05 StartAngle=1.5708 EndAngle=2.0944
    g13: ArcOfCircle CenterX=-6.5 CenterY=47.5 CenterZ=0 NormalX=0 NormalY=0 NormalZ=1 Radius=4.05 StartAngle=2.0944 EndAngle=2.31086
    g14: LineSegment StartX=-9.23104 StartY=50.4906 StartZ=0 EndX=-12.6333 EndY=47.3837 EndZ=0
    g15: ArcOfCircle CenterX=-10 CenterY=44.5 CenterZ=0 NormalX=0 NormalY=0 NormalZ=1 Radius=3.90512 StartAngle=2.31086 EndAngle=2.89937
    g16: ArcOfCircle CenterX=-10 CenterY=44.5 CenterZ=0 NormalX=0 NormalY=0 NormalZ=1 Radius=3.90512 StartAngle=2.89937 EndAngle=4.18879
    g17: ArcOfCircle CenterX=-10 CenterY=44.5 CenterZ=0 NormalX=0 NormalY=0 NormalZ=1 Radius=3.90512 StartAngle=4.18879 EndAngle=5.11254
    g18: LineSegment StartX=-8.47871 StartY=40.9034 StartZ=0 EndX=-6.99264 EndY=41.532 EndZ=0
    g19: ArcOfCircle CenterX=6.64943e-07 CenterY=25 CenterZ=0 NormalX=0 NormalY=0 NormalZ=1 Radius=17.95 StartAngle=1.5708 EndAngle=1.97095
    g20: ArcOfCircle CenterX=-6.64943e-07 CenterY=25 CenterZ=0 NormalX=0 NormalY=0 NormalZ=1 Radius=17.95 StartAngle=1.17064 EndAngle=1.5708
    g21: LineSegment StartX=6.99264 StartY=41.532 StartZ=0 EndX=8.47871 EndY=40.9034 EndZ=0
    g22: ArcOfCircle CenterX=10 CenterY=44.5 CenterZ=0 NormalX=0 NormalY=0 NormalZ=1 Radius=3.90512 StartAngle=4.31223 EndAngle=5.23599
    g23: ArcOfCircle CenterX=10 CenterY=44.5 CenterZ=0 NormalX=0 NormalY=0 NormalZ=1 Radius=3.90512 StartAngle=5.23599 EndAngle=6.52541
    g24: ArcOfCircle CenterX=10 CenterY=44.5 CenterZ=0 NormalX=0 NormalY=0 NormalZ=1 Radius=3.90512 StartAngle=0.242222 EndAngle=0.830737
    g25: Circle CenterX=-10 CenterY=44.5 CenterZ=0 NormalX=0 NormalY=0 NormalZ=1 Radius=3
    g26: Circle CenterX=-1.27 CenterY=47.77 CenterZ=0 NormalX=0 NormalY=0 NormalZ=1 Radius=0.55
    g27: Circle CenterX=-1.27 CenterY=45.23 CenterZ=0 NormalX=0 NormalY=0 NormalZ=1 Radius=0.55
    g28: Circle CenterX=10 CenterY=44.5 CenterZ=0 NormalX=0 NormalY=0 NormalZ=1 Radius=3
    g29: Circle CenterX=1.27 CenterY=47.77 CenterZ=0 NormalX=0 NormalY=0 NormalZ=1 Radius=0.55
    g30: Circle CenterX=1.27 CenterY=45.23 CenterZ=0 NormalX=0 NormalY=0 NormalZ=1 Radius=0.55
  constraints (3):
    c: Coincident(g0,g1)
    c: Coincident(g1,g2)
    c: Coincident(g2,g0)
FEATURE [PartDesign::Pad] Pad046  label="PriseMagnetique"
  Length = 1
  Length2 = 100
  Sketch = -> Sketch287
  Type = 0
FEATURE [Sketcher::SketchObject] Sketch290
  sketch-geometry (62):
    g0: ArcOfCircle CenterX=-9 CenterY=2.5 CenterZ=0 NormalX=0 NormalY=0 NormalZ=1 Radius=1 StartAngle=3.14159 EndAngle=4.71239
    g1: LineSegment StartX=-9 StartY=1.5 StartZ=0 EndX=-4 EndY=1.5 EndZ=0
    g2: ArcOfCircle CenterX=-4 CenterY=3.5 CenterZ=0 NormalX=0 NormalY=0 NormalZ=1 Radius=2 StartAngle=4.71239 EndAngle=6.28319
    g3: LineSegment StartX=-2 StartY=3.5 StartZ=0 EndX=-2 EndY=5 EndZ=0
    g4: ArcOfCircle CenterX=-3 CenterY=5 CenterZ=0 NormalX=0 NormalY=0 NormalZ=1 Radius=1 StartAngle=0 EndAngle=1.5708
    g5: LineSegment StartX=-3 StartY=6 StartZ=0 EndX=-8 EndY=6 EndZ=0
    g6: ArcOfCircle CenterX=-8 CenterY=4 CenterZ=0 NormalX=0 NormalY=0 NormalZ=1 Radius=2 StartAngle=1.5708 EndAngle=3.14159
    g7: LineSegment StartX=-10 StartY=4 StartZ=0 EndX=-10 EndY=2.5 EndZ=0
    g8: LineSegment StartX=-12 StartY=3.5 StartZ=0 EndX=-15 EndY=0.5 EndZ=0
    g9: LineSegment StartX=-15 StartY=0.5 StartZ=0 EndX=-15 EndY=0 EndZ=0
    g10: LineSegment StartX=-15 StartY=0 StartZ=0 EndX=-14 EndY=0 EndZ=0
    g11: LineSegment StartX=-14 StartY=0 StartZ=0 EndX=-12.7071 EndY=0 EndZ=0
    g12: ArcOfCircle CenterX=-12.3536 CenterY=-0.353554 CenterZ=0 NormalX=0 NormalY=0 NormalZ=1 Radius=0.5 StartAngle=5.49779 EndAngle=8.63938
    g13: LineSegment StartX=-12 StartY=-0.707107 StartZ=0 EndX=-12 EndY=-1.5 EndZ=0
    g14: LineSegment StartX=-12 StartY=-1.5 StartZ=0 EndX=-8 EndY=-1.5 EndZ=0
    g15: LineSegment StartX=-8 StartY=-1.5 StartZ=0 EndX=-8 EndY=-0.707107 EndZ=0
    g16: ArcOfCircle CenterX=-7.64645 CenterY=-0.353554 CenterZ=0 NormalX=0 NormalY=0 NormalZ=1 Radius=0.5 StartAngle=0.785398 EndAngle=3.92699
    g17: LineSegment StartX=-7.29289 StartY=0 StartZ=0 EndX=1 EndY=0 EndZ=0
    g18: LineSegment StartX=1 StartY=0 StartZ=0 EndX=1 EndY=0.5 EndZ=0
    g19: LineSegment StartX=1 StartY=0.5 StartZ=0 EndX=0 EndY=1.5 EndZ=0
    g20: LineSegment StartX=0 StartY=1.5 StartZ=0 EndX=0 EndY=4 EndZ=0
    g21: LineSegment StartX=0 StartY=4 StartZ=0 EndX=0 EndY=7 EndZ=0
    g22: LineSegment StartX=0 StartY=7 StartZ=0 EndX=1 EndY=8 EndZ=0
    g23: LineSegment StartX=1 StartY=8 StartZ=0 EndX=4 EndY=8 EndZ=0
    g24: LineSegment StartX=4 StartY=8 StartZ=0 EndX=10 EndY=8 EndZ=0
    g25: LineSegment StartX=10 StartY=8 StartZ=0 EndX=10 EndY=17 EndZ=0
    g26: LineSegment StartX=10 StartY=17 StartZ=0 EndX=11 EndY=18 EndZ=0
    g27: LineSegment StartX=11 StartY=18 StartZ=0 EndX=11 EndY=19 EndZ=0
    g28: LineSegment StartX=11 StartY=19 StartZ=0 EndX=10.7071 EndY=19 EndZ=0
    g29: ArcOfCircle CenterX=10.3536 CenterY=19.3536 CenterZ=0 NormalX=0 NormalY=0 NormalZ=1 Radius=0.5 StartAngle=3.92699 EndAngle=5.49779
    g30: ArcOfCircle CenterX=10.3536 CenterY=19.3536 CenterZ=0 NormalX=0 NormalY=0 NormalZ=1 Radius=0.5 StartAngle=2.35619 EndAngle=3.92699
    g31: LineSegment StartX=10 StartY=19.7071 StartZ=0 EndX=10 EndY=21 EndZ=0
    g32: LineSegment StartX=10 StartY=21 StartZ=0 EndX=2 EndY=21 EndZ=0
    g33: LineSegment StartX=2 StartY=21 StartZ=0 EndX=2 EndY=19.7071 EndZ=0
    g34: ArcOfCircle CenterX=1.64645 CenterY=19.3536 CenterZ=0 NormalX=0 NormalY=0 NormalZ=1 Radius=0.5 StartAngle=5.49779 EndAngle=7.06858
    g35: ArcOfCircle CenterX=1.64645 CenterY=19.3536 CenterZ=0 NormalX=0 NormalY=0 NormalZ=1 Radius=0.5 StartAngle=3.92699 EndAngle=5.49779
    g36: LineSegment StartX=1.29289 StartY=19 StartZ=0 EndX=-4.29289 EndY=19 EndZ=0
    g37: ArcOfCircle CenterX=-4.64645 CenterY=19.3536 CenterZ=0 NormalX=0 NormalY=0 NormalZ=1 Radius=0.5 StartAngle=3.92699 EndAngle=5.49779
    g38: ArcOfCircle CenterX=-4.64645 CenterY=19.3536 CenterZ=0 NormalX=0 NormalY=0 NormalZ=1 Radius=0.5 StartAngle=2.35619 EndAngle=3.92699
    g39: LineSegment StartX=-5 StartY=19.7071 StartZ=0 EndX=-5 EndY=21 EndZ=0
    g40: LineSegment StartX=-5 StartY=21 StartZ=0 EndX=-10 EndY=21 EndZ=0
    g41: LineSegment StartX=-10 StartY=21 StartZ=0 EndX=-10 EndY=19.7071 EndZ=0
    g42: ArcOfCircle CenterX=-10.3536 CenterY=19.3536 CenterZ=0 NormalX=0 NormalY=0 NormalZ=1 Radius=0.5 StartAngle=5.49779 EndAngle=7.06858
    g43: ArcOfCircle CenterX=-10.3536 CenterY=19.3536 CenterZ=0 NormalX=0 NormalY=0 NormalZ=1 Radius=0.5 StartAngle=3.92699 EndAngle=5.49779
    g44: LineSegment StartX=-10.7071 StartY=19 StartZ=0 EndX=-11 EndY=19 EndZ=0
    g45: LineSegment StartX=-11 StartY=19 StartZ=0 EndX=-11 EndY=18 EndZ=0
    g46: LineSegment StartX=-11 StartY=18 StartZ=0 EndX=-10 EndY=17 EndZ=0
    g47: LineSegment StartX=-10 StartY=17 StartZ=0 EndX=-10 EndY=8.70711 EndZ=0
    g48: ArcOfCircle CenterX=-10.3536 CenterY=8.35355 CenterZ=0 NormalX=0 NormalY=0 NormalZ=1 Radius=0.5 StartAngle=3.92699 EndAngle=7.06858
    g49: LineSegment StartX=-10.7071 StartY=8 StartZ=0 EndX=-13 EndY=8 EndZ=0
    g50: LineSegment StartX=-13 StartY=8 StartZ=0 EndX=-13 EndY=7.5 EndZ=0
    g51: LineSegment StartX=-13 StartY=7.5 StartZ=0 EndX=-12 EndY=6.5 EndZ=0
    g52: LineSegment StartX=-12 StartY=6.5 StartZ=0 EndX=-12 EndY=3.5 EndZ=0
    g53: Circle CenterX=6.89985 CenterY=10.11 CenterZ=0 NormalX=0 NormalY=0 NormalZ=1 Radius=0.3
    g54: Circle CenterX=6.89985 CenterY=12.65 CenterZ=0 NormalX=0 NormalY=0 NormalZ=1 Radius=0.3
    g55: Circle CenterX=-6.5352 CenterY=10.0895 CenterZ=0 NormalX=0 NormalY=0 NormalZ=1 Radius=0.3
    g56: Circle CenterX=-6.5352 CenterY=12.6295 CenterZ=0 NormalX=0 NormalY=0 NormalZ=1 Radius=0.3
    g57: Circle CenterX=8.16985 CenterY=11.38 CenterZ=0 NormalX=0 NormalY=0 NormalZ=1 Radius=0.3
    g58: Circle CenterX=-5.2652 CenterY=11.3595 CenterZ=0 NormalX=0 NormalY=0 NormalZ=1 Radius=0.3
    g59: Circle CenterX=-2 CenterY=10.11 CenterZ=0 NormalX=0 NormalY=0 NormalZ=1 Radius=0.3
    g60: Circle CenterX=-2 CenterY=12.65 CenterZ=0 NormalX=0 NormalY=0 NormalZ=1 Radius=0.3
    g61: Circle CenterX=-0.73 CenterY=11.38 CenterZ=0 NormalX=0 NormalY=0 NormalZ=1 Radius=0.3
FEATURE [PartDesign::Pad] Pad043
  Length = 1
  Length2 = 100
  Sketch = -> Sketch290
  Type = 0
FEATURE [Part::FeaturePython] Clone128  label="PCB45G"  # Draft clone (typed FeaturePython)
  Objects = -> [Pad043]
  Placement = pos=(-12.364,41.7218,1) rot=(-0.281085,0.678598,0.678598;3.68962rad)
  Scale = (1,1,1)
FEATURE [Part::Mirroring] Part__Mirroring011  label="PCB45G (Mirror #10)"
  Base = (0,0,0)
  Normal = (1,0,0)
  Source = -> Clone128
FEATURE [App::DocumentObjectGroup] Capteurs_PCB45  label="Capteurs-PCB45"
  Group = -> [Pad043,Sketch078,Clone128,Part__Mirroring011]
FEATURE [Sketcher::SketchObject] Sketch292
  sketch-geometry (144):
    g0: ArcOfCircle CenterX=1.87091e-07 CenterY=-25 CenterZ=0 NormalX=0 NormalY=0 NormalZ=1 Radius=10.75 StartAngle=0.00220409 EndAngle=2.0944
    g1: ArcOfCircle CenterX=3.9285e-08 CenterY=-25 CenterZ=0 NormalX=0 NormalY=0 NormalZ=1 Radius=10.75 StartAngle=2.0944 EndAngle=6.28319
    g2: ArcOfCircle CenterX=-0.000164998 CenterY=-24.9999 CenterZ=0 NormalX=0 NormalY=0 NormalZ=1 Radius=10.7502 StartAngle=6.28318 EndAngle=6.28538
    g3: ArcOfCircle CenterX=5.2257e-08 CenterY=25 CenterZ=0 NormalX=0 NormalY=0 NormalZ=1 Radius=10.75 StartAngle=0.00220411 EndAngle=2.0944
    g4: ArcOfCircle CenterX=3.9285e-08 CenterY=25 CenterZ=0 NormalX=0 NormalY=0 NormalZ=1 Radius=10.75 StartAngle=2.0944 EndAngle=6.28319
    g5: ArcOfCircle CenterX=4.71853e-05 CenterY=25.0001 CenterZ=0 NormalX=0 NormalY=0 NormalZ=1 Radius=10.75 StartAngle=6.28318 EndAngle=6.28538
    g6: LineSegment StartX=-23 StartY=20 StartZ=0 EndX=-23 EndY=-20 EndZ=0
    g7: ArcOfCircle CenterX=-27 CenterY=-20 CenterZ=0 NormalX=0 NormalY=0 NormalZ=1 Radius=4 StartAngle=5.04269 EndAngle=6.28319
    g8: ArcOfCircle CenterX=-24.6 CenterY=-27 CenterZ=0 NormalX=0 NormalY=0 NormalZ=1 Radius=3.4 StartAngle=1.90109 EndAngle=3.14159
    g9: LineSegment StartX=-28 StartY=-27 StartZ=0 EndX=-28 EndY=-28 EndZ=0
    g10: ArcOfCircle CenterX=-20 CenterY=-28 CenterZ=0 NormalX=0 NormalY=0 NormalZ=1 Radius=8 StartAngle=3.14159 EndAngle=4.24064
    g11: LineSegment StartX=-23.6355 StartY=-35.1262 StartZ=0 EndX=-9.2722 EndY=-42.4539 EndZ=0
    g12: ArcOfCircle CenterX=-7 CenterY=-38 CenterZ=0 NormalX=0 NormalY=0 NormalZ=1 Radius=5.00001 StartAngle=4.24065 EndAngle=4.71239
    g13: LineSegment StartX=-7 StartY=-43 StartZ=0 EndX=6.99998 EndY=-43 EndZ=0
    g14: ArcOfCircle CenterX=6.99997 CenterY=-38 CenterZ=0 NormalX=0 NormalY=0 NormalZ=1 Radius=5.00002 StartAngle=4.71239 EndAngle=5.18413
    g15: LineSegment StartX=9.27219 StartY=-42.4539 StartZ=0 EndX=23.6355 EndY=-35.1262 EndZ=0
    g16: ArcOfCircle CenterX=20 CenterY=-28 CenterZ=0 NormalX=0 NormalY=0 NormalZ=1 Radius=8 StartAngle=5.18414 EndAngle=6.28319
    g17: LineSegment StartX=28 StartY=-28 StartZ=0 EndX=28 EndY=-27 EndZ=0
    g18: ArcOfCircle CenterX=24.6 CenterY=-27 CenterZ=0 NormalX=0 NormalY=0 NormalZ=1 Radius=3.4 StartAngle=5.9605e-08 EndAngle=1.2405
    g19: ArcOfCircle CenterX=27 CenterY=-20 CenterZ=0 NormalX=0 NormalY=0 NormalZ=1 Radius=4 StartAngle=3.14159 EndAngle=4.38209
    g20: LineSegment StartX=23 StartY=-20 StartZ=0 EndX=23 EndY=20 EndZ=0
    g21: ArcOfCircle CenterX=26 CenterY=20 CenterZ=0 NormalX=0 NormalY=0 NormalZ=1 Radius=3 StartAngle=1.5708 EndAngle=3.14159
    g22: ArcOfCircle CenterX=26 CenterY=31.8284 CenterZ=0 NormalX=0 NormalY=0 NormalZ=1 Radius=8.82842 StartAngle=4.71239 EndAngle=5.49779
    g23: LineSegment StartX=32.2426 StartY=25.5858 StartZ=0 EndX=33.8284 EndY=27.1716 EndZ=0
    g24: ArcOfCircle CenterX=31 CenterY=30 CenterZ=0 NormalX=0 NormalY=0 NormalZ=1 Radius=4 StartAngle=5.49779 EndAngle=6.28319
    g25: LineSegment StartX=35 StartY=30 StartZ=0 EndX=35 EndY=31.5 EndZ=0
    g26: ArcOfCircle CenterX=31.0355 CenterY=31.5 CenterZ=0 NormalX=0 NormalY=0 NormalZ=1 Radius=3.96447 StartAngle=1.78814e-07 EndAngle=0.785398
    g27: LineSegment StartX=33.8388 StartY=34.3033 StartZ=0 EndX=17.0711 EndY=51.0711 EndZ=0
    g28: ArcOfCircle CenterX=10 CenterY=44 CenterZ=0 NormalX=0 NormalY=0 NormalZ=1 Radius=10 StartAngle=0.785398 EndAngle=1.5708
    g29: LineSegment StartX=10 StartY=54 StartZ=0 EndX=-10 EndY=54 EndZ=0
    g30: ArcOfCircle CenterX=-10 CenterY=44 CenterZ=0 NormalX=0 NormalY=0 NormalZ=1 Radius=10 StartAngle=1.5708 EndAngle=2.35619
    g31: LineSegment StartX=-17.0711 StartY=51.0711 StartZ=0 EndX=-33.8388 EndY=34.3033 EndZ=0
    g32: ArcOfCircle CenterX=-31.0355 CenterY=31.5 CenterZ=0 NormalX=0 NormalY=0 NormalZ=1 Radius=3.96447 StartAngle=2.35619 EndAngle=3.14159
    g33: LineSegment StartX=-35 StartY=31.5 StartZ=0 EndX=-35 EndY=30 EndZ=0
    g34: ArcOfCircle CenterX=-31 CenterY=30 CenterZ=0 NormalX=0 NormalY=0 NormalZ=1 Radius=4 StartAngle=3.14159 EndAngle=3.92699
    g35: LineSegment StartX=-33.8284 StartY=27.1716 StartZ=0 EndX=-32.2426 EndY=25.5858 EndZ=0
    g36: ArcOfCircle CenterX=-26 CenterY=31.8284 CenterZ=0 NormalX=0 NormalY=0 NormalZ=1 Radius=8.82842 StartAngle=3.92699 EndAngle=4.71239
    g37: ArcOfCircle CenterX=-26 CenterY=20 CenterZ=0 NormalX=0 NormalY=0 NormalZ=1 Radius=3 StartAngle=0 EndAngle=1.5708
    g38: ArcOfCircle CenterX=-19.855 CenterY=43.645 CenterZ=0 NormalX=0 NormalY=0 NormalZ=1 Radius=0.502046 StartAngle=5.49779 EndAngle=8.63938
    g39: LineSegment StartX=-20.21 StartY=44 StartZ=0 EndX=-20.29 EndY=44 EndZ=0
    g40: ArcOfCircle CenterX=-20.645 CenterY=43.645 CenterZ=0 NormalX=0 NormalY=0 NormalZ=1 Radius=0.502046 StartAngle=0.785398 EndAngle=3.92699
    g41: LineSegment StartX=-21 StartY=43.29 StartZ=0 EndX=-21 EndY=41.71 EndZ=0
    g42: ArcOfCircle CenterX=-20.645 CenterY=41.355 CenterZ=0 NormalX=0 NormalY=0 NormalZ=1 Radius=0.502046 StartAngle=2.35619 EndAngle=5.49779
    g43: LineSegment StartX=-20.29 StartY=41 StartZ=0 EndX=-20.21 EndY=41 EndZ=0
    g44: ArcOfCircle CenterX=-19.855 CenterY=41.355 CenterZ=0 NormalX=0 NormalY=0 NormalZ=1 Radius=0.502046 StartAngle=3.92699 EndAngle=7.06858
    g45: LineSegment StartX=-19.5 StartY=41.71 StartZ=0 EndX=-19.5 EndY=43.29 EndZ=0
    g46: ArcOfCircle CenterX=-19.855 CenterY=-6.855 CenterZ=0 NormalX=0 NormalY=0 NormalZ=1 Radius=0.502046 StartAngle=5.49779 EndAngle=8.63938
    g47: LineSegment StartX=-20.21 StartY=-6.5 StartZ=0 EndX=-20.29 EndY=-6.5 EndZ=0
    g48: ArcOfCircle CenterX=-20.645 CenterY=-6.855 CenterZ=0 NormalX=0 NormalY=0 NormalZ=1 Radius=0.502046 StartAngle=0.785398 EndAngle=3.92699
    g49: LineSegment StartX=-21 StartY=-7.21 StartZ=0 EndX=-21 EndY=-8.79 EndZ=0
    g50: ArcOfCircle CenterX=-20.645 CenterY=-9.145 CenterZ=0 NormalX=0 NormalY=0 NormalZ=1 Radius=0.502046 StartAngle=2.35619 EndAngle=5.49779
    g51: LineSegment StartX=-20.29 StartY=-9.5 StartZ=0 EndX=-20.21 EndY=-9.5 EndZ=0
    g52: ArcOfCircle CenterX=-19.855 CenterY=-9.145 CenterZ=0 NormalX=0 NormalY=0 NormalZ=1 Radius=0.502046 StartAngle=3.92699 EndAngle=7.06858
    g53: LineSegment StartX=-19.5 StartY=-8.79 StartZ=0 EndX=-19.5 EndY=-7.21 EndZ=0
    g54: ArcOfCircle CenterX=-19.855 CenterY=-30.855 CenterZ=0 NormalX=0 NormalY=0 NormalZ=1 Radius=0.502046 StartAngle=5.49779 EndAngle=8.63938
    g55: LineSegment StartX=-20.21 StartY=-30.5 StartZ=0 EndX=-20.29 EndY=-30.5 EndZ=0
    g56: ArcOfCircle CenterX=-20.645 CenterY=-30.855 CenterZ=0 NormalX=0 NormalY=0 NormalZ=1 Radius=0.502046 StartAngle=0.785398 EndAngle=3.92699
    g57: LineSegment StartX=-21 StartY=-31.21 StartZ=0 EndX=-21 EndY=-32.79 EndZ=0
    g58: ArcOfCircle CenterX=-20.645 CenterY=-33.145 CenterZ=0 NormalX=0 NormalY=0 NormalZ=1 Radius=0.502046 StartAngle=2.35619 EndAngle=5.49779
    g59: LineSegment StartX=-20.29 StartY=-33.5 StartZ=0 EndX=-20.21 EndY=-33.5 EndZ=0
    g60: ArcOfCircle CenterX=-19.855 CenterY=-33.145 CenterZ=0 NormalX=0 NormalY=0 NormalZ=1 Radius=0.502046 StartAngle=3.92699 EndAngle=7.06858
    g61: LineSegment StartX=-19.5 StartY=-32.79 StartZ=0 EndX=-19.5 EndY=-31.21 EndZ=0
    g62: ArcOfCircle CenterX=19.855 CenterY=43.645 CenterZ=0 NormalX=0 NormalY=0 NormalZ=1 Radius=0.502046 StartAngle=0.785398 EndAngle=3.92699
    g63: LineSegment StartX=20.21 StartY=44 StartZ=0 EndX=20.29 EndY=44 EndZ=0
    g64: ArcOfCircle CenterX=20.645 CenterY=43.645 CenterZ=0 NormalX=0 NormalY=0 NormalZ=1 Radius=0.502046 StartAngle=5.49779 EndAngle=8.63938
    g65: LineSegment StartX=21 StartY=43.29 StartZ=0 EndX=21 EndY=41.71 EndZ=0
    g66: ArcOfCircle CenterX=20.645 CenterY=41.355 CenterZ=0 NormalX=0 NormalY=0 NormalZ=1 Radius=0.502046 StartAngle=3.92699 EndAngle=7.06858
    g67: LineSegment StartX=20.29 StartY=41 StartZ=0 EndX=20.21 EndY=41 EndZ=0
    g68: ArcOfCircle CenterX=19.855 CenterY=41.355 CenterZ=0 NormalX=0 NormalY=0 NormalZ=1 Radius=0.502046 StartAngle=2.35619 EndAngle=5.49779
    g69: LineSegment StartX=19.5 StartY=41.71 StartZ=0 EndX=19.5 EndY=43.29 EndZ=0
    g70: ArcOfCircle CenterX=19.855 CenterY=-30.855 CenterZ=0 NormalX=0 NormalY=0 NormalZ=1 Radius=0.502046 StartAngle=0.785398 EndAngle=3.92699
    g71: LineSegment StartX=20.21 StartY=-30.5 StartZ=0 EndX=20.29 EndY=-30.5 EndZ=0
    g72: ArcOfCircle CenterX=20.645 CenterY=-30.855 CenterZ=0 NormalX=0 NormalY=0 NormalZ=1 Radius=0.502046 StartAngle=5.49779 EndAngle=8.63938
    g73: LineSegment StartX=21 StartY=-31.21 StartZ=0 EndX=21 EndY=-32.79 EndZ=0
    g74: ArcOfCircle CenterX=20.645 CenterY=-33.145 CenterZ=0 NormalX=0 NormalY=0 NormalZ=1 Radius=0.502046 StartAngle=3.92699 EndAngle=7.06858
    g75: LineSegment StartX=20.29 StartY=-33.5 StartZ=0 EndX=20.21 EndY=-33.5 EndZ=0
    g76: ArcOfCircle CenterX=19.855 CenterY=-33.145 CenterZ=0 NormalX=0 NormalY=0 NormalZ=1 Radius=0.502046 StartAngle=2.35619 EndAngle=5.49779
    g77: LineSegment StartX=19.5 StartY=-32.79 StartZ=0 EndX=19.5 EndY=-31.21 EndZ=0
    g78: ArcOfCircle CenterX=-19.855 CenterY=6.855 CenterZ=0 NormalX=0 NormalY=0 NormalZ=1 Radius=0.502046 StartAngle=3.92699 EndAngle=7.06858
    g79: LineSegment StartX=-20.21 StartY=6.5 StartZ=0 EndX=-20.29 EndY=6.5 EndZ=0
    g80: ArcOfCircle CenterX=-20.645 CenterY=6.855 CenterZ=0 NormalX=0 NormalY=0 NormalZ=1 Radius=0.502046 StartAngle=2.35619 EndAngle=5.49779
    g81: LineSegment StartX=-21 StartY=7.21 StartZ=0 EndX=-21 EndY=8.79 EndZ=0
    g82: ArcOfCircle CenterX=-20.645 CenterY=9.145 CenterZ=0 NormalX=0 NormalY=0 NormalZ=1 Radius=0.502046 StartAngle=0.785398 EndAngle=3.92699
    g83: LineSegment StartX=-20.29 StartY=9.5 StartZ=0 EndX=-20.21 EndY=9.5 EndZ=0
    g84: ArcOfCircle CenterX=-19.855 CenterY=9.145 CenterZ=0 NormalX=0 NormalY=0 NormalZ=1 Radius=0.502046 StartAngle=5.49779 EndAngle=8.63938
    g85: LineSegment StartX=-19.5 StartY=8.79 StartZ=0 EndX=-19.5 EndY=7.21 EndZ=0
    g86: ArcOfCircle CenterX=19.855 CenterY=-6.855 CenterZ=0 NormalX=0 NormalY=0 NormalZ=1 Radius=0.502046 StartAngle=0.785398 EndAngle=3.92699
    g87: LineSegment StartX=20.21 StartY=-6.5 StartZ=0 EndX=20.29 EndY=-6.5 EndZ=0
    g88: ArcOfCircle CenterX=20.645 CenterY=-6.855 CenterZ=0 NormalX=0 NormalY=0 NormalZ=1 Radius=0.502046 StartAngle=5.49779 EndAngle=8.63938
    g89: LineSegment StartX=21 StartY=-7.21 StartZ=0 EndX=21 EndY=-8.79 EndZ=0
    g90: ArcOfCircle CenterX=20.645 CenterY=-9.145 CenterZ=0 NormalX=0 NormalY=0 NormalZ=1 Radius=0.502046 StartAngle=3.92699 EndAngle=7.06858
    g91: LineSegment StartX=20.29 StartY=-9.5 StartZ=0 EndX=20.21 EndY=-9.5 EndZ=0
    g92: ArcOfCircle CenterX=19.855 CenterY=-9.145 CenterZ=0 NormalX=0 NormalY=0 NormalZ=1 Radius=0.502046 StartAngle=2.35619 EndAngle=5.49779
    g93: LineSegment StartX=19.5 StartY=-8.79 StartZ=0 EndX=19.5 EndY=-7.21 EndZ=0
    g94: ArcOfCircle CenterX=19.855 CenterY=6.855 CenterZ=0 NormalX=0 NormalY=0 NormalZ=1 Radius=0.502046 StartAngle=2.35619 EndAngle=5.49779
    g95: LineSegment StartX=20.21 StartY=6.5 StartZ=0 EndX=20.29 EndY=6.5 EndZ=0
    g96: ArcOfCircle CenterX=20.645 CenterY=6.855 CenterZ=0 NormalX=0 NormalY=0 NormalZ=1 Radius=0.502046 StartAngle=3.92699 EndAngle=7.06858
    g97: LineSegment StartX=21 StartY=7.21 StartZ=0 EndX=21 EndY=8.79 EndZ=0
    g98: ArcOfCircle CenterX=20.645 CenterY=9.145 CenterZ=0 NormalX=0 NormalY=0 NormalZ=1 Radius=0.502046 StartAngle=5.49779 EndAngle=8.63938
    g99: LineSegment StartX=20.29 StartY=9.5 StartZ=0 EndX=20.21 EndY=9.5 EndZ=0
    g100: ArcOfCircle CenterX=19.855 CenterY=9.145 CenterZ=0 NormalX=0 NormalY=0 NormalZ=1 Radius=0.502046 StartAngle=0.785398 EndAngle=3.92699
    g101: LineSegment StartX=19.5 StartY=8.79 StartZ=0 EndX=19.5 EndY=7.21 EndZ=0
    g102: LineSegment StartX=4.4 StartY=-2.7 StartZ=0 EndX=2.4 EndY=-2.7 EndZ=0
    g103: LineSegment StartX=2.4 StartY=-2.7 StartZ=0 EndX=2.4 EndY=2.7 EndZ=0
    g104: LineSegment StartX=2.4 StartY=2.7 StartZ=0 EndX=4.4 EndY=2.7 EndZ=0
    g105: LineSegment StartX=4.4 StartY=2.7 StartZ=0 EndX=4.9 EndY=4 EndZ=0
    g106: LineSegment StartX=4.9 StartY=4 StartZ=0 EndX=19.4 EndY=4 EndZ=0
    g107: LineSegment StartX=19.4 StartY=4 StartZ=0 EndX=19.4 EndY=-4 EndZ=0
    g108: LineSegment StartX=19.4 StartY=-4 StartZ=0 EndX=4.9 EndY=-4 EndZ=0
    g109: LineSegment StartX=4.9 StartY=-4 StartZ=0 EndX=4.4 EndY=-2.7 EndZ=0
    g110: LineSegment StartX=-4.4 StartY=-2.7 StartZ=0 EndX=-4.9 EndY=-4 EndZ=0
    g111: LineSegment StartX=-4.9 StartY=-4 StartZ=0 EndX=-19.4 EndY=-4 EndZ=0
    g112: LineSegment StartX=-19.4 StartY=-4 StartZ=0 EndX=-19.4 EndY=4 EndZ=0
    g113: LineSegment StartX=-19.4 StartY=4 StartZ=0 EndX=-4.9 EndY=4 EndZ=0
    g114: LineSegment StartX=-4.9 StartY=4 StartZ=0 EndX=-4.4 EndY=2.7 EndZ=0
    g115: LineSegment StartX=-4.4 StartY=2.7 StartZ=0 EndX=-2.4 EndY=2.7 EndZ=0
    g116: LineSegment StartX=-2.4 StartY=2.7 StartZ=0 EndX=-2.4 EndY=-2.7 EndZ=0
    g117: LineSegment StartX=-2.4 StartY=-2.7 StartZ=0 EndX=-4.4 EndY=-2.7 EndZ=0
    g118: LineSegment StartX=12.7008 StartY=47.4575 StartZ=0 EndX=9.29848 EndY=50.5645 EndZ=0
    g119: ArcOfCircle CenterX=6.5 CenterY=47.5 CenterZ=0 NormalX=0 NormalY=0 NormalZ=1 Radius=4.15 StartAngle=0.830737 EndAngle=1.0472
    g120: ArcOfCircle CenterX=6.5 CenterY=47.5 CenterZ=0 NormalX=0 NormalY=0 NormalZ=1 Radius=4.15 StartAngle=1.0472 EndAngle=1.5708
    g121: LineSegment StartX=6.5 StartY=51.65 StartZ=0 EndX=0 EndY=51.65 EndZ=0
    g122: LineSegment StartX=0 StartY=51.65 StartZ=0 EndX=-6.5 EndY=51.65 EndZ=0
    g123: ArcOfCircle CenterX=-6.5 CenterY=47.5 CenterZ=0 NormalX=0 NormalY=0 NormalZ=1 Radius=4.15 StartAngle=1.5708 EndAngle=2.0944
    g124: ArcOfCircle CenterX=-6.5 CenterY=47.5 CenterZ=0 NormalX=0 NormalY=0 NormalZ=1 Radius=4.15 StartAngle=2.09439 EndAngle=2.31086
    g125: LineSegment StartX=-9.29848 StartY=50.5645 StartZ=0 EndX=-12.7008 EndY=47.4575 EndZ=0
    g126: ArcOfCircle CenterX=-10 CenterY=44.5 CenterZ=0 NormalX=0 NormalY=0 NormalZ=1 Radius=4.00513 StartAngle=2.31086 EndAngle=2.89937
    g127: ArcOfCircle CenterX=-10 CenterY=44.5 CenterZ=0 NormalX=0 NormalY=0 NormalZ=1 Radius=4.00513 StartAngle=2.89937 EndAngle=4.18879
    g128: ArcOfCircle CenterX=-10 CenterY=44.5 CenterZ=0 NormalX=0 NormalY=0 NormalZ=1 Radius=4.00512 StartAngle=4.18879 EndAngle=5.11255
    g129: LineSegment StartX=-8.43975 StartY=40.8113 StartZ=0 EndX=-6.95368 EndY=41.4399 EndZ=0
    g130: ArcOfCircle CenterX=5.06016e-07 CenterY=25 CenterZ=0 NormalX=0 NormalY=0 NormalZ=1 Radius=17.85 StartAngle=1.5708 EndAngle=1.97095
    g131: ArcOfCircle CenterX=-5.06016e-07 CenterY=25 CenterZ=0 NormalX=0 NormalY=0 NormalZ=1 Radius=17.85 StartAngle=1.17064 EndAngle=1.5708
    g132: LineSegment StartX=6.95368 StartY=41.4399 StartZ=0 EndX=8.43975 EndY=40.8113 EndZ=0
    g133: ArcOfCircle CenterX=10 CenterY=44.5 CenterZ=0 NormalX=0 NormalY=0 NormalZ=1 Radius=4.00512 StartAngle=4.31223 EndAngle=5.23599
    g134: ArcOfCircle CenterX=10 CenterY=44.5 CenterZ=0 NormalX=0 NormalY=0 NormalZ=1 Radius=4.00513 StartAngle=5.23599 EndAngle=6.52541
    g135: ArcOfCircle CenterX=10 CenterY=44.5 CenterZ=0 NormalX=0 NormalY=0 NormalZ=1 Radius=4.00512 StartAngle=0.242222 EndAngle=0.830737
    g136: ArcOfCircle CenterX=-31.4066 CenterY=28.7188 CenterZ=0 NormalX=0 NormalY=0 NormalZ=1 Radius=0.5 StartAngle=1.67552 EndAngle=4.81711
    g137: LineSegment StartX=-31.3544 StartY=28.2215 StartZ=0 EndX=-28.3708 EndY=28.5351 EndZ=0
    g138: ArcOfCircle CenterX=-28.4231 CenterY=29.0324 CenterZ=0 NormalX=0 NormalY=0 NormalZ=1 Radius=0.5 StartAngle=4.81711 EndAngle=7.9587
    g139: LineSegment StartX=-28.4753 StartY=29.5296 StartZ=0 EndX=-31.4589 EndY=29.216 EndZ=0
    g140: ArcOfCircle CenterX=31.4066 CenterY=28.7188 CenterZ=0 NormalX=0 NormalY=0 NormalZ=1 Radius=0.5 StartAngle=4.60767 EndAngle=7.74926
    g141: LineSegment StartX=31.3544 StartY=28.2215 StartZ=0 EndX=28.3708 EndY=28.5351 EndZ=0
    g142: ArcOfCircle CenterX=28.4231 CenterY=29.0324 CenterZ=0 NormalX=0 NormalY=0 NormalZ=1 Radius=0.5 StartAngle=1.46608 EndAngle=4.60767
    g143: LineSegment StartX=28.4753 StartY=29.5296 StartZ=0 EndX=31.4589 EndY=29.216 EndZ=0
FEATURE [PartDesign::Pad] Pad035  label="Base1mm"
  Length = 1
  Length2 = 100
  Sketch = -> Sketch292
  Type = 0
FEATURE [Sketcher::SketchObject] Sketch293
  sketch-geometry (37):
    g0: LineSegment StartX=-4.5 StartY=2.5 StartZ=0 EndX=-4.5 EndY=6.5 EndZ=0
    g1: ArcOfCircle CenterX=-5.5 CenterY=6.5 CenterZ=0 NormalX=0 NormalY=0 NormalZ=1 Radius=1 StartAngle=0 EndAngle=3.14159
    g2: LineSegment StartX=-6.5 StartY=6.5 StartZ=0 EndX=-6.5 EndY=2.5 EndZ=0
    g3: ArcOfCircle CenterX=-5.5 CenterY=2.5 CenterZ=0 NormalX=0 NormalY=0 NormalZ=1 Radius=1 StartAngle=3.14159 EndAngle=6.28319
    g4: LineSegment StartX=-12.2071 StartY=19 StartZ=0 EndX=-12.5 EndY=19 EndZ=0
    g5: LineSegment StartX=-12.5 StartY=19 StartZ=0 EndX=-12.5 EndY=18 EndZ=0
    g6: LineSegment StartX=-12.5 StartY=18 StartZ=0 EndX=-11.5 EndY=17 EndZ=0
    g7: LineSegment StartX=-11.5 StartY=17 StartZ=0 EndX=-11.5 EndY=8 EndZ=0
    g8: LineSegment StartX=-11.5 StartY=8 StartZ=0 EndX=-9 EndY=8 EndZ=0
    g9: LineSegment StartX=-9 StartY=8 StartZ=0 EndX=-8 EndY=7 EndZ=0
    g10: LineSegment StartX=-8 StartY=7 StartZ=0 EndX=-8 EndY=1.5 EndZ=0
    g11: LineSegment StartX=-8 StartY=1.5 StartZ=0 EndX=-9 EndY=0.5 EndZ=0
    g12: LineSegment StartX=-9 StartY=0.5 StartZ=0 EndX=-9 EndY=0 EndZ=0
    g13: LineSegment StartX=-9 StartY=0 StartZ=0 EndX=-8.20711 EndY=0 EndZ=0
    g14: ArcOfCircle CenterX=-7.85355 CenterY=-0.353554 CenterZ=0 NormalX=0 NormalY=0 NormalZ=1 Radius=0.5 StartAngle=5.49779 EndAngle=8.63938
    g15: LineSegment StartX=-7.5 StartY=-0.707107 StartZ=0 EndX=-7.5 EndY=-1.5 EndZ=0
    g16: LineSegment StartX=-7.5 StartY=-1.5 StartZ=0 EndX=-4.5 EndY=-1.5 EndZ=0
    g17: LineSegment StartX=-4.5 StartY=-1.5 StartZ=0 EndX=-4.5 EndY=-0.707107 EndZ=0
    g18: ArcOfCircle CenterX=-4.14645 CenterY=-0.353554 CenterZ=0 NormalX=0 NormalY=0 NormalZ=1 Radius=0.5 StartAngle=0.785398 EndAngle=3.92699
    g19: LineSegment StartX=-3.79289 StartY=0 StartZ=0 EndX=-1.5 EndY=0 EndZ=0
    g20: LineSegment StartX=-1.5 StartY=0 StartZ=0 EndX=-1.5 EndY=0.5 EndZ=0
    g21: LineSegment StartX=-1.5 StartY=0.5 StartZ=0 EndX=-3 EndY=2 EndZ=0
    g22: LineSegment StartX=-3 StartY=2 StartZ=0 EndX=-3 EndY=6.5 EndZ=0
    g23: LineSegment StartX=-3 StartY=6.5 StartZ=0 EndX=-2.5 EndY=7 EndZ=0
    g24: LineSegment StartX=-2.5 StartY=7 StartZ=0 EndX=-1.5 EndY=8 EndZ=0
    g25: LineSegment StartX=-1.5 StartY=8 StartZ=0 EndX=-1.5 EndY=19 EndZ=0
    g26: LineSegment StartX=-1.5 StartY=19 StartZ=0 EndX=-2.79289 EndY=19 EndZ=0
    g27: ArcOfCircle CenterX=-3.14645 CenterY=19.3536 CenterZ=0 NormalX=0 NormalY=0 NormalZ=1 Radius=0.5 StartAngle=3.92699 EndAngle=5.49779
    g28: ArcOfCircle CenterX=-3.14645 CenterY=19.3536 CenterZ=0 NormalX=0 NormalY=0 NormalZ=1 Radius=0.5 StartAngle=2.35619 EndAngle=3.92699
    g29: LineSegment StartX=-3.5 StartY=19.7071 StartZ=0 EndX=-3.5 EndY=21 EndZ=0
    g30: LineSegment StartX=-3.5 StartY=21 StartZ=0 EndX=-11.5 EndY=21 EndZ=0
    g31: LineSegment StartX=-11.5 StartY=21 StartZ=0 EndX=-11.5 EndY=19.7071 EndZ=0
    g32: ArcOfCircle CenterX=-11.8536 CenterY=19.3536 CenterZ=0 NormalX=0 NormalY=0 NormalZ=1 Radius=0.5 StartAngle=5.49779 EndAngle=7.06858
    g33: ArcOfCircle CenterX=-11.8536 CenterY=19.3536 CenterZ=0 NormalX=0 NormalY=0 NormalZ=1 Radius=0.5 StartAngle=3.92699 EndAngle=5.49779
    g34: Circle CenterX=-6.30253 CenterY=10.0895 CenterZ=0 NormalX=0 NormalY=0 NormalZ=1 Radius=0.3
    g35: Circle CenterX=-6.30253 CenterY=12.6295 CenterZ=0 NormalX=0 NormalY=0 NormalZ=1 Radius=0.3
    g36: Circle CenterX=-5.03253 CenterY=11.3595 CenterZ=0 NormalX=0 NormalY=0 NormalZ=1 Radius=0.3
FEATURE [PartDesign::Pad] Pad044
  Length = 1
  Length2 = 100
  Sketch = -> Sketch293
  Type = 0
FEATURE [Part::FeaturePython] Clone129  label="PCB6G"  # Draft clone (typed FeaturePython)
  Objects = -> [Pad044]
  Placement = pos=(-35.8297,27.7511,1) rot=(-0.037032,0.706622,0.706622;3.21562rad)
  Scale = (1,1,1)
FEATURE [Part::Mirroring] Part__Mirroring012  label="PCB6G (Mirror #11)"
  Base = (0,0,0)
  Normal = (1,0,0)
  Source = -> Clone129
FEATURE [App::DocumentObjectGroup] Capteurs_PCB6  label="Capteurs-PCB6"
  Group = -> [Pad044,Sketch082,Clone129,Part__Mirroring012]
FEATURE [App::DocumentObjectGroup] Groupe040  label="SupportsCapteurs"
  Group = -> [Capteurs_PCB45,Capteurs_PCB6]
FEATURE [App::DocumentObjectGroup] Groupe053  label="Capteurs"
  Group = -> [Groupe040,Groupe039,Groupe054]
FEATURE [Sketcher::SketchObject] Sketch294
  sketch-geometry (231):
    g0: ArcOfCircle CenterX=-27 CenterY=-20 CenterZ=0 NormalX=0 NormalY=0 NormalZ=1 Radius=4 StartAngle=5.04269 EndAngle=6.28319
    g1: ArcOfCircle CenterX=-24.6 CenterY=-27 CenterZ=0 NormalX=0 NormalY=0 NormalZ=1 Radius=3.4 StartAngle=1.90109 EndAngle=3.14159
    g2: LineSegment StartX=-28 StartY=-27 StartZ=0 EndX=-28 EndY=-28 EndZ=0
    g3: ArcOfCircle CenterX=-20 CenterY=-28 CenterZ=0 NormalX=0 NormalY=0 NormalZ=1 Radius=8 StartAngle=3.14159 EndAngle=4.24064
    g4: LineSegment StartX=-23.6355 StartY=-35.1262 StartZ=0 EndX=-9.2722 EndY=-42.4539 EndZ=0
    g5: ArcOfCircle CenterX=-7 CenterY=-38 CenterZ=0 NormalX=0 NormalY=0 NormalZ=1 Radius=5.00001 StartAngle=4.24065 EndAngle=4.71239
    g6: LineSegment StartX=-7 StartY=-43 StartZ=0 EndX=6.99998 EndY=-43 EndZ=0
    g7: ArcOfCircle CenterX=7 CenterY=-38 CenterZ=0 NormalX=0 NormalY=0 NormalZ=1 Radius=5.00003 StartAngle=4.71238 EndAngle=5.18189
    g8: ArcOfCircle CenterX=6.99479 CenterY=-38.0027 CenterZ=0 NormalX=0 NormalY=0 NormalZ=1 Radius=4.99996 StartAngle=5.18307 EndAngle=5.18531
    g9: LineSegment StartX=9.27219 StartY=-42.4539 StartZ=0 EndX=23.6355 EndY=-35.1262 EndZ=0
    g10: ArcOfCircle CenterX=20 CenterY=-28 CenterZ=0 NormalX=0 NormalY=0 NormalZ=1 Radius=8 StartAngle=5.18414 EndAngle=6.28319
    g11: LineSegment StartX=28 StartY=-28 StartZ=0 EndX=28 EndY=-27 EndZ=0
    g12: ArcOfCircle CenterX=24.6 CenterY=-27 CenterZ=0 NormalX=0 NormalY=0 NormalZ=1 Radius=3.4 StartAngle=6.28319 EndAngle=7.52368
    g13: ArcOfCircle CenterX=27 CenterY=-20 CenterZ=0 NormalX=0 NormalY=0 NormalZ=1 Radius=4 StartAngle=3.14159 EndAngle=4.38209
    g14: LineSegment StartX=23 StartY=-20 StartZ=0 EndX=23 EndY=20 EndZ=0
    g15: ArcOfCircle CenterX=26 CenterY=20 CenterZ=0 NormalX=0 NormalY=0 NormalZ=1 Radius=3 StartAngle=1.5708 EndAngle=3.14159
    g16: ArcOfCircle CenterX=26 CenterY=31.8284 CenterZ=0 NormalX=0 NormalY=0 NormalZ=1 Radius=8.82842 StartAngle=4.71239 EndAngle=5.49779
    g17: LineSegment StartX=32.2426 StartY=25.5858 StartZ=0 EndX=33.0356 EndY=26.3787 EndZ=0
    g18: LineSegment StartX=33.0356 StartY=26.3787 StartZ=0 EndX=33.8284 EndY=27.1716 EndZ=0
    g19: ArcOfCircle CenterX=31 CenterY=30 CenterZ=0 NormalX=0 NormalY=0 NormalZ=1 Radius=4 StartAngle=5.49779 EndAngle=6.28319
    g20: LineSegment StartX=35 StartY=30 StartZ=0 EndX=35 EndY=31.5 EndZ=0
    g21: ArcOfCircle CenterX=31.0355 CenterY=31.5 CenterZ=0 NormalX=0 NormalY=0 NormalZ=1 Radius=3.96447 StartAngle=1.78814e-07 EndAngle=0.785398
    g22: LineSegment StartX=33.8388 StartY=34.3033 StartZ=0 EndX=17.0711 EndY=51.0711 EndZ=0
    g23: ArcOfCircle CenterX=10 CenterY=44 CenterZ=0 NormalX=0 NormalY=0 NormalZ=1 Radius=10 StartAngle=0.785398 EndAngle=1.26737
    g24: ArcOfCircle CenterX=10 CenterY=44 CenterZ=0 NormalX=0 NormalY=0 NormalZ=1 Radius=10 StartAngle=1.26737 EndAngle=1.5708
    g25: LineSegment StartX=10 StartY=54 StartZ=0 EndX=-10 EndY=54 EndZ=0
    g26: ArcOfCircle CenterX=-10 CenterY=44 CenterZ=0 NormalX=0 NormalY=0 NormalZ=1 Radius=10 StartAngle=1.5708 EndAngle=2.35619
    g27: LineSegment StartX=-17.0711 StartY=51.0711 StartZ=0 EndX=-33.8388 EndY=34.3033 EndZ=0
    g28: ArcOfCircle CenterX=-31.0355 CenterY=31.5 CenterZ=0 NormalX=0 NormalY=0 NormalZ=1 Radius=3.96447 StartAngle=2.35619 EndAngle=3.14159
    g29: LineSegment StartX=-35 StartY=31.5 StartZ=0 EndX=-35 EndY=30 EndZ=0
    g30: ArcOfCircle CenterX=-31 CenterY=30 CenterZ=0 NormalX=0 NormalY=0 NormalZ=1 Radius=4 StartAngle=3.14159 EndAngle=3.92699
    g31: LineSegment StartX=-33.8284 StartY=27.1716 StartZ=0 EndX=-32.2426 EndY=25.5858 EndZ=0
    g32: ArcOfCircle CenterX=-26 CenterY=31.8284 CenterZ=0 NormalX=0 NormalY=0 NormalZ=1 Radius=8.82842 StartAngle=3.92699 EndAngle=4.71239
    g33: ArcOfCircle CenterX=-26 CenterY=20 CenterZ=0 NormalX=0 NormalY=0 NormalZ=1 Radius=3 StartAngle=0 EndAngle=1.5708
    g34: LineSegment StartX=-23 StartY=20 StartZ=0 EndX=-23 EndY=-20 EndZ=0
    g35: LineSegment StartX=-4.4 StartY=-2.7 StartZ=0 EndX=-4.9 EndY=-4 EndZ=0
    g36: LineSegment StartX=-4.9 StartY=-4 StartZ=0 EndX=-17.5 EndY=-4 EndZ=0
    g37: LineSegment StartX=-17.5 StartY=-4 StartZ=0 EndX=-17.5 EndY=4 EndZ=0
    g38: LineSegment StartX=-17.5 StartY=4 StartZ=0 EndX=-4.9 EndY=4 EndZ=0
    g39: LineSegment StartX=-4.9 StartY=4 StartZ=0 EndX=-4.4 EndY=2.7 EndZ=0
    g40: LineSegment StartX=-4.4 StartY=2.7 StartZ=0 EndX=-2.4 EndY=2.7 EndZ=0
    g41: LineSegment StartX=-2.4 StartY=2.7 StartZ=0 EndX=-2.4 EndY=-2.7 EndZ=0
    g42: LineSegment StartX=-2.4 StartY=-2.7 StartZ=0 EndX=-4.4 EndY=-2.7 EndZ=0
    g43: LineSegment StartX=4.4 StartY=2.7 StartZ=0 EndX=4.9 EndY=4 EndZ=0
    g44: LineSegment StartX=4.9 StartY=4 StartZ=0 EndX=17.5 EndY=4 EndZ=0
    g45: LineSegment StartX=17.5 StartY=4 StartZ=0 EndX=17.5 EndY=-4 EndZ=0
    g46: LineSegment StartX=17.5 StartY=-4 StartZ=0 EndX=4.9 EndY=-4 EndZ=0
    g47: LineSegment StartX=4.9 StartY=-4 StartZ=0 EndX=4.4 EndY=-2.7 EndZ=0
    g48: LineSegment StartX=4.4 StartY=-2.7 StartZ=0 EndX=2.4 EndY=-2.7 EndZ=0
    g49: LineSegment StartX=2.4 StartY=-2.7 StartZ=0 EndX=2.4 EndY=2.7 EndZ=0
    g50: LineSegment StartX=2.4 StartY=2.7 StartZ=0 EndX=4.4 EndY=2.7 EndZ=0
    g51: ArcOfCircle CenterX=-9 CenterY=-40.5 CenterZ=0 NormalX=0 NormalY=0 NormalZ=1 Radius=0.75 StartAngle=3.332e-08 EndAngle=2.0944
    g52: ArcOfCircle CenterX=-9 CenterY=-40.5 CenterZ=0 NormalX=0 NormalY=0 NormalZ=1 Radius=0.75 StartAngle=2.0944 EndAngle=4.18879
    g53: ArcOfCircle CenterX=-9 CenterY=-40.5 CenterZ=0 NormalX=0 NormalY=0 NormalZ=1 Radius=0.75 StartAngle=4.18879 EndAngle=6.28319
    g54: ArcOfCircle CenterX=9 CenterY=-40.5 CenterZ=0 NormalX=0 NormalY=0 NormalZ=1 Radius=0.75 StartAngle=3.332e-08 EndAngle=2.0944
    g55: ArcOfCircle CenterX=9 CenterY=-40.5 CenterZ=0 NormalX=0 NormalY=0 NormalZ=1 Radius=0.75 StartAngle=2.0944 EndAngle=4.18879
    g56: ArcOfCircle CenterX=9 CenterY=-40.5 CenterZ=0 NormalX=0 NormalY=0 NormalZ=1 Radius=0.75 StartAngle=4.18879 EndAngle=6.28319
    g57: ArcOfCircle CenterX=-31.0355 CenterY=31.5 CenterZ=0 NormalX=0 NormalY=0 NormalZ=1 Radius=2.46447 StartAngle=2.35619 EndAngle=3.14159
    g58: LineSegment StartX=-32.7782 StartY=33.2426 StartZ=0 EndX=-28.5104 EndY=37.5104 EndZ=0
    g59: LineSegment StartX=-28.5104 StartY=37.5104 StartZ=0 EndX=-17.5688 EndY=26.5688 EndZ=0
    g60: LineSegment StartX=-17.5688 StartY=26.5688 StartZ=0 EndX=-19 EndY=20 EndZ=0
    g61: LineSegment StartX=-19 StartY=20 StartZ=0 EndX=-19 EndY=16 EndZ=0
    g62: LineSegment StartX=-19 StartY=16 StartZ=0 EndX=-21.5 EndY=16 EndZ=0
    g63: LineSegment StartX=-21.5 StartY=16 StartZ=0 EndX=-21.5 EndY=20 EndZ=0
    g64: ArcOfCircle CenterX=-26 CenterY=20 CenterZ=0 NormalX=0 NormalY=0 NormalZ=1 Radius=4.50001 StartAngle=2.26036e-06 EndAngle=1.57079
    g65: ArcOfCircle CenterX=-26 CenterY=31.8284 CenterZ=0 NormalX=0 NormalY=0 NormalZ=1 Radius=7.32842 StartAngle=3.92699 EndAngle=4.71239
    g66: LineSegment StartX=-31.182 StartY=26.6464 StartZ=0 EndX=-32.7678 EndY=28.2322 EndZ=0
    g67: ArcOfCircle CenterX=-31 CenterY=30 CenterZ=0 NormalX=0 NormalY=0 NormalZ=1 Radius=2.5 StartAngle=3.14159 EndAngle=3.92699
    g68: LineSegment StartX=-33.5 StartY=30 StartZ=0 EndX=-33.5 EndY=31.5 EndZ=0
    g69: ArcOfCircle CenterX=13 CenterY=-38 CenterZ=0 NormalX=0 NormalY=0 NormalZ=1 Radius=1.11803 StartAngle=2.0944 EndAngle=4.18879
    g70: ArcOfCircle CenterX=13 CenterY=-38 CenterZ=0 NormalX=0 NormalY=0 NormalZ=1 Radius=1.11803 StartAngle=4.18879 EndAngle=6.28319
    g71: ArcOfCircle CenterX=13 CenterY=-38 CenterZ=0 NormalX=0 NormalY=0 NormalZ=1 Radius=1.11803 StartAngle=6.28319 EndAngle=8.37758
    g72: ArcOfCircle CenterX=-13 CenterY=-38 CenterZ=0 NormalX=0 NormalY=0 NormalZ=1 Radius=1.11803 StartAngle=2.0944 EndAngle=4.18879
    g73: ArcOfCircle CenterX=-13 CenterY=-38 CenterZ=0 NormalX=0 NormalY=0 NormalZ=1 Radius=1.11803 StartAngle=4.18879 EndAngle=6.28319
    g74: ArcOfCircle CenterX=-13 CenterY=-38 CenterZ=0 NormalX=0 NormalY=0 NormalZ=1 Radius=1.11803 StartAngle=6.28319 EndAngle=8.37758
    g75: LineSegment StartX=3.3698 StartY=-4.2 StartZ=0 EndX=3.49998 EndY=-4.53847 EndZ=0
    g76: ArcOfCircle CenterX=4.9 CenterY=-4 CenterZ=0 NormalX=0 NormalY=0 NormalZ=1 Radius=1.5 StartAngle=3.50877 EndAngle=4.71239
    g77: LineSegment StartX=4.9 StartY=-5.5 StartZ=0 EndX=17.5 EndY=-5.5 EndZ=0
    g78: LineSegment StartX=17.5 StartY=-5.5 StartZ=0 EndX=17.5 EndY=-20 EndZ=0
    g79: LineSegment StartX=17.5 StartY=-20 StartZ=0 EndX=15.6195 EndY=-28.4684 EndZ=0
    g80: ArcOfCircle CenterX=-7.2343e-08 CenterY=-25 CenterZ=0 NormalX=0 NormalY=0 NormalZ=1 Radius=16 StartAngle=4.18879 EndAngle=6.06468
    g81: ArcOfCircle CenterX=-1.3365e-07 CenterY=-25 CenterZ=0 NormalX=0 NormalY=0 NormalZ=1 Radius=16 StartAngle=3.3601 EndAngle=4.18879
    g82: LineSegment StartX=-15.6195 StartY=-28.4684 StartZ=0 EndX=-17.5 EndY=-20 EndZ=0
    g83: LineSegment StartX=-17.5 StartY=-20 StartZ=0 EndX=-17.5 EndY=-5.5 EndZ=0
    g84: LineSegment StartX=-17.5 StartY=-5.5 StartZ=0 EndX=-4.9 EndY=-5.5 EndZ=0
    g85: ArcOfCircle CenterX=-4.9 CenterY=-4 CenterZ=0 NormalX=0 NormalY=0 NormalZ=1 Radius=1.5 StartAngle=4.71239 EndAngle=5.91601
    g86: LineSegment StartX=-3.49998 StartY=-4.53847 StartZ=0 EndX=-3.3698 EndY=-4.2 EndZ=0
    g87: LineSegment StartX=-3.3698 StartY=-4.2 StartZ=0 EndX=-2.4 EndY=-4.2 EndZ=0
    g88: ArcOfCircle CenterX=-2.4 CenterY=-2.7 CenterZ=0 NormalX=0 NormalY=0 NormalZ=1 Radius=1.5 StartAngle=4.71239 EndAngle=6.28319
    g89: LineSegment StartX=-0.9 StartY=-2.7 StartZ=0 EndX=-0.9 EndY=2.7 EndZ=0
    g90: ArcOfCircle CenterX=-2.4 CenterY=2.7 CenterZ=0 NormalX=0 NormalY=0 NormalZ=1 Radius=1.5 StartAngle=0 EndAngle=1.5708
    g91: LineSegment StartX=-2.4 StartY=4.2 StartZ=0 EndX=-3.3698 EndY=4.2 EndZ=0
    g92: LineSegment StartX=-3.3698 StartY=4.2 StartZ=0 EndX=-3.49998 EndY=4.53847 EndZ=0
    g93: ArcOfCircle CenterX=-4.9 CenterY=4 CenterZ=0 NormalX=0 NormalY=0 NormalZ=1 Radius=1.5 StartAngle=0.367174 EndAngle=1.5708
    g94: LineSegment StartX=-4.9 StartY=5.5 StartZ=0 EndX=-17.5 EndY=5.5 EndZ=0
    g95: LineSegment StartX=-17.5 StartY=5.5 StartZ=0 EndX=-17.5 EndY=20 EndZ=0
    g96: LineSegment StartX=-17.5 StartY=20 StartZ=0 EndX=-15.6195 EndY=28.4684 EndZ=0
    g97: ArcOfCircle CenterX=-1.3365e-07 CenterY=25 CenterZ=0 NormalX=0 NormalY=0 NormalZ=1 Radius=16 StartAngle=2.0944 EndAngle=2.92308
    g98: ArcOfCircle CenterX=-7.2343e-08 CenterY=25 CenterZ=0 NormalX=0 NormalY=0 NormalZ=1 Radius=16 StartAngle=0.21851 EndAngle=2.0944
    g99: LineSegment StartX=15.6195 StartY=28.4684 StartZ=0 EndX=17.5 EndY=20 EndZ=0
    g100: LineSegment StartX=17.5 StartY=20 StartZ=0 EndX=17.5 EndY=5.5 EndZ=0
    g101: LineSegment StartX=17.5 StartY=5.5 StartZ=0 EndX=4.9 EndY=5.5 EndZ=0
    g102: ArcOfCircle CenterX=4.9 CenterY=4 CenterZ=0 NormalX=0 NormalY=0 NormalZ=1 Radius=1.5 StartAngle=1.5708 EndAngle=2.77442
    g103: LineSegment StartX=3.49998 StartY=4.53847 StartZ=0 EndX=3.3698 EndY=4.2 EndZ=0
    g104: LineSegment StartX=3.3698 StartY=4.2 StartZ=0 EndX=2.4 EndY=4.2 EndZ=0
    g105: ArcOfCircle CenterX=2.4 CenterY=2.7 CenterZ=0 NormalX=0 NormalY=0 NormalZ=1 Radius=1.5 StartAngle=1.5708 EndAngle=3.14159
    g106: LineSegment StartX=0.9 StartY=2.7 StartZ=0 EndX=0.9 EndY=-2.7 EndZ=0
    g107: ArcOfCircle CenterX=2.4 CenterY=-2.7 CenterZ=0 NormalX=0 NormalY=0 NormalZ=1 Radius=1.5 StartAngle=3.14159 EndAngle=4.71239
    g108: LineSegment StartX=2.4 StartY=-4.2 StartZ=0 EndX=3.3698 EndY=-4.2 EndZ=0
    g109: LineSegment StartX=-19 StartY=11.5 StartZ=0 EndX=-18.5 EndY=11.5 EndZ=0
    g110: LineSegment StartX=-18.5 StartY=11.5 StartZ=0 EndX=-18.5 EndY=4.5 EndZ=0
    g111: LineSegment StartX=-18.5 StartY=4.5 StartZ=0 EndX=-19 EndY=4.5 EndZ=0
    g112: LineSegment StartX=-19 StartY=4.5 StartZ=0 EndX=-19 EndY=-4.5 EndZ=0
    g113: LineSegment StartX=-19 StartY=-4.5 StartZ=0 EndX=-18.5 EndY=-4.5 EndZ=0
    g114: LineSegment StartX=-18.5 StartY=-4.5 StartZ=0 EndX=-18.5 EndY=-11.5 EndZ=0
    g115: LineSegment StartX=-18.5 StartY=-11.5 StartZ=0 EndX=-19 EndY=-11.5 EndZ=0
    g116: LineSegment StartX=-19 StartY=-11.5 StartZ=0 EndX=-19 EndY=-14.5 EndZ=0
    g117: LineSegment StartX=-19 StartY=-14.5 StartZ=0 EndX=-21.5 EndY=-14.5 EndZ=0
    g118: LineSegment StartX=-21.5 StartY=-14.5 StartZ=0 EndX=-21.5 EndY=-11.5 EndZ=0
    g119: LineSegment StartX=-21.5 StartY=-11.5 StartZ=0 EndX=-22 EndY=-11.5 EndZ=0
    g120: LineSegment StartX=-22 StartY=-11.5 StartZ=0 EndX=-22 EndY=-4.5 EndZ=0
    g121: LineSegment StartX=-22 StartY=-4.5 StartZ=0 EndX=-21.5 EndY=-4.5 EndZ=0
    g122: LineSegment StartX=-21.5 StartY=-4.5 StartZ=0 EndX=-21.5 EndY=4.5 EndZ=0
    g123: LineSegment StartX=-21.5 StartY=4.5 StartZ=0 EndX=-22 EndY=4.5 EndZ=0
    g124: LineSegment StartX=-22 StartY=4.5 StartZ=0 EndX=-22 EndY=11.5 EndZ=0
    g125: LineSegment StartX=-22 StartY=11.5 StartZ=0 EndX=-21.5 EndY=11.5 EndZ=0
    g126: LineSegment StartX=-21.5 StartY=11.5 StartZ=0 EndX=-21.5 EndY=14.5 EndZ=0
    g127: LineSegment StartX=-21.5 StartY=14.5 StartZ=0 EndX=-19 EndY=14.5 EndZ=0
    g128: LineSegment StartX=-19 StartY=14.5 StartZ=0 EndX=-19 EndY=11.5 EndZ=0
    g129: LineSegment StartX=19 StartY=11.5 StartZ=0 EndX=18.5 EndY=11.5 EndZ=0
    g130: LineSegment StartX=18.5 StartY=11.5 StartZ=0 EndX=18.5 EndY=4.5 EndZ=0
    g131: LineSegment StartX=18.5 StartY=4.5 StartZ=0 EndX=19 EndY=4.5 EndZ=0
    g132: LineSegment StartX=19 StartY=4.5 StartZ=0 EndX=19 EndY=-4.5 EndZ=0
    g133: LineSegment StartX=19 StartY=-4.5 StartZ=0 EndX=18.5 EndY=-4.5 EndZ=0
    g134: LineSegment StartX=18.5 StartY=-4.5 StartZ=0 EndX=18.5 EndY=-11.5 EndZ=0
    g135: LineSegment StartX=18.5 StartY=-11.5 StartZ=0 EndX=19 EndY=-11.5 EndZ=0
    g136: LineSegment StartX=19 StartY=-11.5 StartZ=0 EndX=19 EndY=-14.5 EndZ=0
    g137: LineSegment StartX=19 StartY=-14.5 StartZ=0 EndX=21.5 EndY=-14.5 EndZ=0
    g138: LineSegment StartX=21.5 StartY=-14.5 StartZ=0 EndX=21.5 EndY=-11.5 EndZ=0
    g139: LineSegment StartX=21.5 StartY=-11.5 StartZ=0 EndX=22 EndY=-11.5 EndZ=0
    g140: LineSegment StartX=22 StartY=-11.5 StartZ=0 EndX=22 EndY=-4.5 EndZ=0
    g141: LineSegment StartX=22 StartY=-4.5 StartZ=0 EndX=21.5 EndY=-4.5 EndZ=0
    g142: LineSegment StartX=21.5 StartY=-4.5 StartZ=0 EndX=21.5 EndY=4.5 EndZ=0
    g143: LineSegment StartX=21.5 StartY=4.5 StartZ=0 EndX=22 EndY=4.5 EndZ=0
    g144: LineSegment StartX=22 StartY=4.5 StartZ=0 EndX=22 EndY=11.5 EndZ=0
    g145: LineSegment StartX=22 StartY=11.5 StartZ=0 EndX=21.5 EndY=11.5 EndZ=0
    g146: LineSegment StartX=21.5 StartY=11.5 StartZ=0 EndX=21.5 EndY=14.5 EndZ=0
    g147: LineSegment StartX=21.5 StartY=14.5 StartZ=0 EndX=19 EndY=14.5 EndZ=0
    g148: LineSegment StartX=19 StartY=14.5 StartZ=0 EndX=19 EndY=11.5 EndZ=0
    g149: ArcOfCircle CenterX=-21.5 CenterY=45.5 CenterZ=0 NormalX=0 NormalY=0 NormalZ=1 Radius=0.5 StartAngle=2.0944 EndAngle=3.14159
    g150: LineSegment StartX=-22 StartY=45.5 StartZ=0 EndX=-22 EndY=44.0208 EndZ=0
    g151: LineSegment StartX=-22 StartY=44.0208 StartZ=0 EndX=-27.4497 EndY=38.5711 EndZ=0
    g152: LineSegment StartX=-27.4497 StartY=38.5711 StartZ=0 EndX=-17.1893 EndY=28.3106 EndZ=0
    g153: LineSegment StartX=-17.1893 StartY=28.3106 StartZ=0 EndX=-17.0988 EndY=28.7256 EndZ=0
    g154: ArcOfCircle CenterX=1.79263e-06 CenterY=25 CenterZ=0 NormalX=0 NormalY=0 NormalZ=1 Radius=17.5 StartAngle=2.53419 EndAngle=2.92706
    g155: LineSegment StartX=-14.3698 StartY=34.9879 StartZ=0 EndX=-17.8911 EndY=48.1297 EndZ=0
    g156: LineSegment StartX=-17.8911 StartY=48.1297 StartZ=0 EndX=-20.0208 EndY=46 EndZ=0
    g157: LineSegment StartX=-20.0208 StartY=46 StartZ=0 EndX=-21.5 EndY=46 EndZ=0
    g158: ArcOfCircle CenterX=-21.5 CenterY=45.5 CenterZ=0 NormalX=0 NormalY=0 NormalZ=1 Radius=0.5 StartAngle=1.5708 EndAngle=2.09439
    g159: ArcOfCircle CenterX=21.5 CenterY=45.5 CenterZ=0 NormalX=0 NormalY=0 NormalZ=1 Radius=0.5 StartAngle=6.28319 EndAngle=7.33038
    g160: LineSegment StartX=22 StartY=45.5 StartZ=0 EndX=22 EndY=44.0208 EndZ=0
    g161: LineSegment StartX=22 StartY=44.0208 StartZ=0 EndX=27.4497 EndY=38.5711 EndZ=0
    g162: LineSegment StartX=27.4497 StartY=38.5711 StartZ=0 EndX=17.1893 EndY=28.3106 EndZ=0
    g163: LineSegment StartX=17.1893 StartY=28.3106 StartZ=0 EndX=17.0988 EndY=28.7256 EndZ=0
    g164: ArcOfCircle CenterX=-1.79263e-06 CenterY=25 CenterZ=0 NormalX=0 NormalY=0 NormalZ=1 Radius=17.5 StartAngle=0.214532 EndAngle=0.607403
    g165: LineSegment StartX=14.3698 StartY=34.9879 StartZ=0 EndX=17.8911 EndY=48.1297 EndZ=0
    g166: LineSegment StartX=17.8911 StartY=48.1297 StartZ=0 EndX=20.0208 EndY=46 EndZ=0
    g167: LineSegment StartX=20.0208 StartY=46 StartZ=0 EndX=21.5 EndY=46 EndZ=0
    g168: ArcOfCircle CenterX=21.5 CenterY=45.5 CenterZ=0 NormalX=0 NormalY=0 NormalZ=1 Radius=0.5 StartAngle=1.0472 EndAngle=1.5708
    g169: ArcOfCircle CenterX=-21.5 CenterY=-34.5 CenterZ=0 NormalX=0 NormalY=0 NormalZ=1 Radius=0.5 StartAngle=3.14159 EndAngle=4.18879
    g170: ArcOfCircle CenterX=-21.5 CenterY=-34.5 CenterZ=0 NormalX=0 NormalY=0 NormalZ=1 Radius=0.5 StartAngle=4.18879 EndAngle=4.71239
    g171: LineSegment StartX=-21.5 StartY=-35 StartZ=0 EndX=-20.5822 EndY=-35 EndZ=0
    g172: LineSegment StartX=-20.5822 StartY=-35 StartZ=0 EndX=-16.9284 EndY=-36.8641 EndZ=0
    g173: LineSegment StartX=-16.9284 StartY=-36.8641 StartZ=0 EndX=-16.5594 EndY=-37.0523 EndZ=0
    g174: ArcOfCircle CenterX=-16 CenterY=-35.5 CenterZ=0 NormalX=0 NormalY=0 NormalZ=1 Radius=1.65 StartAngle=4.36648 EndAngle=6.28319
    g175: ArcOfCircle CenterX=-16 CenterY=-35.5 CenterZ=0 NormalX=0 NormalY=0 NormalZ=1 Radius=1.65 StartAngle=6.82694e-07 EndAngle=0.463756
    g176: ArcOfCircle CenterX=2.61038e-05 CenterY=-25 CenterZ=0 NormalX=0 NormalY=0 NormalZ=1 Radius=17.5 StartAngle=3.71134 EndAngle=3.73335
    g177: ArcOfCircle CenterX=-1.44222e-07 CenterY=-25 CenterZ=0 NormalX=0 NormalY=0 NormalZ=1 Radius=17.5 StartAngle=3.35612 EndAngle=3.71134
    g178: LineSegment StartX=-17.0988 StartY=-28.7256 StartZ=0 EndX=-19 EndY=-20 EndZ=0
    g179: LineSegment StartX=-19 StartY=-20 StartZ=0 EndX=-19 EndY=-16 EndZ=0
    g180: LineSegment StartX=-19 StartY=-16 StartZ=0 EndX=-21.5 EndY=-16 EndZ=0
    g181: LineSegment StartX=-21.5 StartY=-16 StartZ=0 EndX=-21.5 EndY=-20 EndZ=0
    g182: ArcOfCircle CenterX=-27 CenterY=-20 CenterZ=0 NormalX=0 NormalY=0 NormalZ=1 Radius=5.5 StartAngle=5.04269 EndAngle=6.28319
    g183: ArcOfCircle CenterX=-24.6 CenterY=-27 CenterZ=0 NormalX=0 NormalY=0 NormalZ=1 Radius=1.9 StartAngle=1.90109 EndAngle=3.14159
    g184: LineSegment StartX=-26.5 StartY=-27 StartZ=0 EndX=-26.5 EndY=-28 EndZ=0
    g185: ArcOfCircle CenterX=-20 CenterY=-28 CenterZ=0 NormalX=0 NormalY=0 NormalZ=1 Radius=6.5 StartAngle=3.14159 EndAngle=4.24064
    g186: LineSegment StartX=-22.9539 StartY=-33.79 StartZ=0 EndX=-22 EndY=-34.2767 EndZ=0
    g187: LineSegment StartX=-22 StartY=-34.2767 StartZ=0 EndX=-22 EndY=-34.5 EndZ=0
    g188: ArcOfCircle CenterX=21.5 CenterY=-34.5 CenterZ=0 NormalX=0 NormalY=0 NormalZ=1 Radius=0.5 StartAngle=5.23599 EndAngle=6.28319
    g189: ArcOfCircle CenterX=21.5 CenterY=-34.5 CenterZ=0 NormalX=0 NormalY=0 NormalZ=1 Radius=0.5 StartAngle=4.71239 EndAngle=5.23599
    g190: LineSegment StartX=21.5 StartY=-35 StartZ=0 EndX=20.5822 EndY=-35 EndZ=0
    g191: LineSegment StartX=20.5822 StartY=-35 StartZ=0 EndX=16.9284 EndY=-36.8641 EndZ=0
    g192: LineSegment StartX=16.9284 StartY=-36.8641 StartZ=0 EndX=16.5594 EndY=-37.0523 EndZ=0
    g193: ArcOfCircle CenterX=16 CenterY=-35.5 CenterZ=0 NormalX=0 NormalY=0 NormalZ=1 Radius=1.65 StartAngle=3.14159 EndAngle=5.0583
    g194: ArcOfCircle CenterX=16 CenterY=-35.5 CenterZ=0 NormalX=0 NormalY=0 NormalZ=1 Radius=1.65 StartAngle=2.67784 EndAngle=3.14159
    g195: ArcOfCircle CenterX=-2.61038e-05 CenterY=-25 CenterZ=0 NormalX=0 NormalY=0 NormalZ=1 Radius=17.5 StartAngle=5.69142 EndAngle=5.71344
    g196: ArcOfCircle CenterX=1.44222e-07 CenterY=-25 CenterZ=0 NormalX=0 NormalY=0 NormalZ=1 Radius=17.5 StartAngle=5.71344 EndAngle=6.06865
    g197: LineSegment StartX=17.0988 StartY=-28.7256 StartZ=0 EndX=19 EndY=-20 EndZ=0
    g198: LineSegment StartX=19 StartY=-20 StartZ=0 EndX=19 EndY=-16 EndZ=0
    g199: LineSegment StartX=19 StartY=-16 StartZ=0 EndX=21.5 EndY=-16 EndZ=0
    g200: LineSegment StartX=21.5 StartY=-16 StartZ=0 EndX=21.5 EndY=-20 EndZ=0
    g201: ArcOfCircle CenterX=27 CenterY=-20 CenterZ=0 NormalX=0 NormalY=0 NormalZ=1 Radius=5.5 StartAngle=3.14159 EndAngle=4.38209
    g202: ArcOfCircle CenterX=24.6 CenterY=-27 CenterZ=0 NormalX=0 NormalY=0 NormalZ=1 Radius=1.9 StartAngle=1.65932e-07 EndAngle=1.2405
    g203: LineSegment StartX=26.5 StartY=-27 StartZ=0 EndX=26.5 EndY=-28 EndZ=0
    g204: ArcOfCircle CenterX=20 CenterY=-28 CenterZ=0 NormalX=0 NormalY=0 NormalZ=1 Radius=6.5 StartAngle=5.18414 EndAngle=6.28319
    g205: LineSegment StartX=22.9539 StartY=-33.79 StartZ=0 EndX=22 EndY=-34.2767 EndZ=0
    g206: LineSegment StartX=22 StartY=-34.2767 StartZ=0 EndX=22 EndY=-34.5 EndZ=0
    g207: ArcOfCircle CenterX=31.0355 CenterY=31.5 CenterZ=0 NormalX=0 NormalY=0 NormalZ=1 Radius=2.46447 StartAngle=1.56285e-07 EndAngle=0.785398
    g208: LineSegment StartX=32.7782 StartY=33.2426 StartZ=0 EndX=28.5104 EndY=37.5104 EndZ=0
    g209: LineSegment StartX=28.5104 StartY=37.5104 StartZ=0 EndX=17.5688 EndY=26.5688 EndZ=0
    g210: LineSegment StartX=17.5688 StartY=26.5688 StartZ=0 EndX=19 EndY=20 EndZ=0
    g211: LineSegment StartX=19 StartY=20 StartZ=0 EndX=19 EndY=16 EndZ=0
    g212: LineSegment StartX=19 StartY=16 StartZ=0 EndX=21.5 EndY=16 EndZ=0
    g213: LineSegment StartX=21.5 StartY=16 StartZ=0 EndX=21.5 EndY=20 EndZ=0
    g214: ArcOfCircle CenterX=26 CenterY=20 CenterZ=0 NormalX=0 NormalY=0 NormalZ=1 Radius=4.50001 StartAngle=1.5708 EndAngle=3.14159
    g215: ArcOfCircle CenterX=26 CenterY=31.8284 CenterZ=0 NormalX=0 NormalY=0 NormalZ=1 Radius=7.32842 StartAngle=4.71239 EndAngle=5.49779
    g216: LineSegment StartX=31.182 StartY=26.6464 StartZ=0 EndX=32.7678 EndY=28.2322 EndZ=0
    g217: ArcOfCircle CenterX=31 CenterY=30 CenterZ=0 NormalX=0 NormalY=0 NormalZ=1 Radius=2.5 StartAngle=5.49779 EndAngle=6.28318
    g218: LineSegment StartX=33.5 StartY=30 StartZ=0 EndX=33.5 EndY=31.5 EndZ=0
    g219: LineSegment StartX=-16.0104 StartY=50.0104 StartZ=0 EndX=-16.6664 EndY=49.3544 EndZ=0
    g220: LineSegment StartX=-16.6664 StartY=49.3544 StartZ=0 EndX=-13.2147 EndY=36.4726 EndZ=0
    g221: ArcOfCircle CenterX=8.52181e-07 CenterY=25 CenterZ=0 NormalX=0 NormalY=0 NormalZ=1 Radius=17.5 StartAngle=2.0944 EndAngle=2.42665
    g222: ArcOfCircle CenterX=-8.0943e-07 CenterY=25 CenterZ=0 NormalX=0 NormalY=0 NormalZ=1 Radius=17.5 StartAngle=1.5708 EndAngle=2.0944
    g223: ArcOfCircle CenterX=8.0943e-07 CenterY=25 CenterZ=0 NormalX=0 NormalY=0 NormalZ=1 Radius=17.5 StartAngle=1.0472 EndAngle=1.5708
    g224: ArcOfCircle CenterX=-8.52181e-07 CenterY=25 CenterZ=0 NormalX=0 NormalY=0 NormalZ=1 Radius=17.5 StartAngle=0.714947 EndAngle=1.0472
    g225: LineSegment StartX=13.2147 StartY=36.4726 StartZ=0 EndX=16.6664 EndY=49.3544 EndZ=0
    g226: LineSegment StartX=16.6664 StartY=49.3544 StartZ=0 EndX=16.0104 EndY=50.0104 EndZ=0
    g227: ArcOfCircle CenterX=10 CenterY=44 CenterZ=0 NormalX=0 NormalY=0 NormalZ=1 Radius=8.5 StartAngle=0.785398 EndAngle=1.5708
    g228: LineSegment StartX=10 StartY=52.5 StartZ=0 EndX=0 EndY=52.5 EndZ=0
    g229: LineSegment StartX=0 StartY=52.5 StartZ=0 EndX=-10 EndY=52.5 EndZ=0
    g230: ArcOfCircle CenterX=-10 CenterY=44 CenterZ=0 NormalX=0 NormalY=0 NormalZ=1 Radius=8.5 StartAngle=1.5708 EndAngle=2.35619
FEATURE [PartDesign::Pad] Pad034  label="Jupe"
  Length = 1.5
  Length2 = 100
  Reversed = true
  Sketch = -> Sketch294
  Type = 0
FEATURE [App::DocumentObjectGroup] Groupe001  label="Base"
  Group = -> [Pad035,Pad034,Pad046]
